FCSTD DOCUMENT  (FreeCAD 1.0R39109 (Git))
Label: internalDesign
License: All rights reserved
LicenseURL: http://en.wikipedia.org/wiki/All_rights_reserved
objects: Part::Feature×502, App::Part×92, Part::Cylinder×73, Part::Box×71, Part::MultiFuse×57, Part::Cut×51, Sketcher::SketchObject×38, Part::Extrusion×37, Part::Fillet×31, Part::Compound×8, Part::Sphere×4, Part::FeaturePython×2, Part::Torus×1
note: 913 computed .brp shape members not serialized (recipe doc carries the construction recipe); baked Part::Feature solids carry a one-line shape summary decoded from their .brp

FEATURE [Part::Feature] Part__Feature016  label="Z_-16147B_ZH-16147B-01"
  shape: bbox 438.9 x 219.4 x 405.1 mm, 3210 faces (baked)
FEATURE [Part::Feature] Part__Feature017  label="INSERTS-4"
  Placement = pos=(-180.975,-168.256,-155.575) rot=(0,0,1;0rad)
  shape: bbox 7.519 x 8.463 x 7.519 mm, 71 faces (baked)
FEATURE [Part::Feature] Part__Feature018  label="INSERTS-005"
  Placement = pos=(-170.872,-174.835,-145.472) rot=(0,0,1;3.14159rad)
  shape: bbox 7.519 x 8.463 x 7.519 mm, 71 faces (baked)
FEATURE [Part::Feature] Part__Feature019  label="INSERTS-006"
  Placement = pos=(-205.994,-3.7592,-180.594) rot=(0,0,1;3.14159rad)
  shape: bbox 7.519 x 8.463 x 7.519 mm, 71 faces (baked)
FEATURE [Part::Feature] Part__Feature020  label="INSERTS-007"
  Placement = pos=(-180.975,-168.083,155.575) rot=(1,0,0;3.14159rad)
  shape: bbox 7.519 x 8.463 x 7.519 mm, 71 faces (baked)
FEATURE [Part::Feature] Part__Feature021  label="INSERTS-008"
  Placement = pos=(-170.872,-175.008,145.472) rot=(0,1,0;3.14159rad)
  shape: bbox 7.519 x 8.463 x 7.519 mm, 71 faces (baked)
FEATURE [Part::Feature] Part__Feature022  label="INSERTS-009"
  Placement = pos=(-205.994,-3.93217,180.594) rot=(0,1,0;3.14159rad)
  shape: bbox 7.519 x 8.463 x 7.519 mm, 71 faces (baked)
FEATURE [Part::Feature] Part__Feature023  label="INSERTS-010"
  Placement = pos=(180.975,-168.083,-155.575) rot=(0,0,1;3.14159rad)
  shape: bbox 7.519 x 8.463 x 7.519 mm, 71 faces (baked)
FEATURE [Part::Feature] Part__Feature024  label="INSERTS-011"
  Placement = pos=(170.872,-175.008,-145.472) rot=(0,0,1;0rad)
  shape: bbox 7.519 x 8.463 x 7.519 mm, 71 faces (baked)
FEATURE [Part::Feature] Part__Feature025  label="INSERTS-012"
  Placement = pos=(205.994,-3.93217,-180.594) rot=(0,0,1;0rad)
  shape: bbox 7.519 x 8.463 x 7.519 mm, 71 faces (baked)
FEATURE [Part::Feature] Part__Feature026  label="INSERTS-013"
  Placement = pos=(180.975,-168.256,155.575) rot=(0,1,0;3.14159rad)
  shape: bbox 7.519 x 8.463 x 7.519 mm, 71 faces (baked)
FEATURE [Part::Feature] Part__Feature027  label="INSERTS-014"
  Placement = pos=(170.872,-174.835,145.472) rot=(1,0,0;3.14159rad)
  shape: bbox 7.519 x 8.463 x 7.519 mm, 71 faces (baked)
FEATURE [Part::Feature] Part__Feature028  label="INSERTS-015"
  Placement = pos=(205.994,-3.7592,180.594) rot=(1,0,0;3.14159rad)
  shape: bbox 7.519 x 8.463 x 7.519 mm, 71 faces (baked)
FEATURE [Part::Feature] Part__Feature029  label="LABEL-104"
  Placement = pos=(-1.221e-12,-20.3197,-180.67) rot=(1,0,0;1.56207rad)
  shape: bbox 63.5 x 38.1 x 0.3833 mm, 10 faces (baked)
FEATURE [Part::Feature] Part__Feature030  label="Z_-16141C_ZH-16141C-01"
  shape: bbox 448.9 x 49.63 x 409 mm, 1738 faces (baked)
FEATURE [Part::Feature] Part__Feature031  label="ZH-1614G"
  Placement = pos=(0,0.635,6.9e-15) rot=(0,0,1;0rad)
  shape: bbox 434.5 x 6.35 x 383.7 mm, 136 faces (baked)
FEATURE [Part::Feature] Part__Feature032  label="ZH-01F_ZH-01F-01"
  Placement = pos=(-158.172,-191.294,-145.472) rot=(0,0,1;0rad)
  shape: bbox 75.05 x 15.88 x 54.71 mm, 393 faces (baked)
FEATURE [Part::Feature] Part__Feature033  label="pan cross head_ai_SCREWS-046"
  Placement = pos=(-170.872,-191.294,-145.472) rot=(-0.002139,-0.002139,0.999995;1.5708rad)
  shape: bbox 10.25 x 22.43 x 10.25 mm, 92 faces (baked)
FEATURE [Part::Feature] Part__Feature034  label="pan cross head_ai_SCREWS-047"
  Placement = pos=(-170.872,-191.294,145.472) rot=(0.002139,0.002139,0.999995;1.5708rad)
  shape: bbox 10.25 x 22.43 x 10.25 mm, 92 faces (baked)
FEATURE [Part::Feature] Part__Feature035  label="ZH-01F_ZH-01F-002"
  Placement = pos=(-158.172,-191.294,145.472) rot=(0,0,1;0rad)
  shape: bbox 75.05 x 15.88 x 54.71 mm, 393 faces (baked)
FEATURE [Part::Feature] Part__Feature036  label="pan cross head_ai_SCREWS-048"
  Placement = pos=(170.872,-191.294,-145.472) rot=(0.707106,0.707106,-0.001512;3.14462rad)
  shape: bbox 10.25 x 22.43 x 10.25 mm, 92 faces (baked)
FEATURE [Part::Feature] Part__Feature037  label="pan cross head_ai_SCREWS-049"
  Placement = pos=(170.872,-191.294,145.472) rot=(0.707106,0.707106,0.001512;3.13857rad)
  shape: bbox 10.25 x 22.43 x 10.25 mm, 92 faces (baked)
FEATURE [Part::Feature] Part__Feature038  label="ZH-01F_ZH-01F-003"
  Placement = pos=(158.172,-191.294,-145.472) rot=(0,1,0;3.14159rad)
  shape: bbox 75.05 x 15.88 x 54.71 mm, 393 faces (baked)
FEATURE [Part::Feature] Part__Feature039  label="ZH-01F_ZH-01F-004"
  Placement = pos=(158.172,-191.294,145.472) rot=(0,1,0;3.14159rad)
  shape: bbox 75.05 x 15.88 x 54.71 mm, 393 faces (baked)
FEATURE [Part::Feature] Part__Feature040  label="SCREWS-047_default"
  Placement = pos=(-205.994,12.0142,-180.594) rot=(-1,0,0;1.5708rad)
  shape: bbox 9.234 x 22.51 x 9.177 mm, 32 faces (baked)
FEATURE [Part::Feature] Part__Feature041  label="SCREWS-047_default001"
  Placement = pos=(205.994,12.0142,-180.594) rot=(-1,0,0;1.5708rad)
  shape: bbox 9.234 x 22.51 x 9.177 mm, 32 faces (baked)
FEATURE [Part::Feature] Part__Feature042  label="SCREWS-047_default002"
  Placement = pos=(-205.994,12.0142,180.594) rot=(-1,0,0;1.5708rad)
  shape: bbox 9.234 x 22.51 x 9.177 mm, 32 faces (baked)
FEATURE [Part::Feature] Part__Feature043  label="SCREWS-047_default003"
  Placement = pos=(205.994,12.0142,180.594) rot=(-1,0,0;1.5708rad)
  shape: bbox 9.234 x 22.51 x 9.177 mm, 32 faces (baked)
FEATURE [App::Part] Z__16141CG_ZH_16141CG_01  label="Z_-16141CG_ZH-16141CG-01"
  Group = -> [Part__Feature030,Part__Feature031]
  Origin = -> Origin005
FEATURE [App::Part] Z__16147BI_ZH_16147BI_01  label="Z_-16147BI_ZH-16147BI-01"
  Group = -> [Part__Feature016,Part__Feature017,Part__Feature018,Part__Feature019,Part__Feature020,Part__Feature021,Part__Feature022,Part__Feature023,Part__Feature024,Part__Feature025,Part__Feature026,Part__Feature027,Part__Feature028,Part__Feature029]
  Origin = -> Origin004
FEATURE [App::Part] ZH_161407_33  label="ZH-161407-33"
  Group = -> [Z__16147BI_ZH_16147BI_01,Z__16141CG_ZH_16141CG_01,Part__Feature032,Part__Feature033,Part__Feature034,Part__Feature035,Part__Feature036,Part__Feature037,Part__Feature038,Part__Feature039,Part__Feature040,Part__Feature041,Part__Feature042,Part__Feature043]
  Origin = -> Origin006
  Placement = pos=(0,0,0) rot=(0.707107,0,0.707107;3.14159rad)
FEATURE [Sketcher::SketchObject] Sketch
  ArcFitTolerance = 0
  FullyConstrained = true
  MakeInternals = false
  Placement = pos=(0,164,0) rot=(1,0,0;1.5708rad)
  sketch-geometry (12):
    g0: ArcOfCircle CenterX=-140.58 CenterY=-165.98 CenterZ=0 NormalX=0 NormalY=0 NormalZ=1 AngleXU=0 Radius=30 StartAngle=3.14159 EndAngle=4.71239
    g1: ArcOfCircle CenterX=-140.58 CenterY=165.98 CenterZ=0 NormalX=0 NormalY=0 NormalZ=1 AngleXU=0 Radius=30 StartAngle=1.5708 EndAngle=3.14159
    g2: ArcOfCircle CenterX=140.58 CenterY=165.98 CenterZ=0 NormalX=0 NormalY=0 NormalZ=1 AngleXU=0 Radius=30 StartAngle=0 EndAngle=1.5708
    g3: ArcOfCircle CenterX=140.58 CenterY=-165.98 CenterZ=0 NormalX=0 NormalY=0 NormalZ=1 AngleXU=0 Radius=30 StartAngle=4.71239 EndAngle=6.28319
    g4: LineSegment StartX=-140.58 StartY=195.98 StartZ=0 EndX=140.58 EndY=195.98 EndZ=0
    g5: LineSegment StartX=-170.58 StartY=165.98 StartZ=0 EndX=-170.58 EndY=-165.98 EndZ=0
    g6: LineSegment StartX=-140.58 StartY=-195.98 StartZ=0 EndX=140.58 EndY=-195.98 EndZ=0
    g7: LineSegment StartX=170.58 StartY=-165.98 StartZ=0 EndX=170.58 EndY=165.98 EndZ=0
    g8: Circle CenterX=-155.58 CenterY=180.98 CenterZ=0 NormalX=0 NormalY=0 NormalZ=1 AngleXU=0 Radius=2.5
    g9: Circle CenterX=-155.58 CenterY=-180.98 CenterZ=0 NormalX=0 NormalY=0 NormalZ=1 AngleXU=0 Radius=2.5
    g10: Circle CenterX=155.58 CenterY=180.98 CenterZ=0 NormalX=0 NormalY=0 NormalZ=1 AngleXU=0 Radius=2.5
    g11: Circle CenterX=155.58 CenterY=-180.98 CenterZ=0 NormalX=0 NormalY=0 NormalZ=1 AngleXU=0 Radius=2.5
  constraints (40):
    c: Coincident(g4,g1)
    c: Coincident(g4,g2)
    c: Horizontal(g4)
    c: Coincident(g5,g1)
    c: Coincident(g5,g0)
    c: Vertical(g5)
    c: Coincident(g6,g0)
    c: Coincident(g6,g3)
    c: Horizontal(g6)
    c: Coincident(g7,g3)
    c: Coincident(g7,g2)
    c: Vertical(g7)
    c: Horizontal(g2,g2)
    c: Vertical(g2,g2)
    c: Vertical(g1,g1)
    c: Vertical(g0,g0)
    c: Vertical(g3,g3)
    c: Horizontal(g3,g3)
    c: DistanceX(g2,g2) = 30
    c: Horizontal(g3,g0)
    c: Vertical(g0,g1)
    c: DistanceX(g1,g8) = 15
    c: DistanceY(g8,g1) = 15
    c: DistanceX(g8) = -155.58
    c: DistanceX(g9) = -155.58
    c: DistanceY(g9) = -180.98
    c: DistanceY(g8) = 180.98
    c: DistanceY(g0,g9) = 15
    c: Horizontal(g1,g1)
    c: DistanceX(g1,g1) = 30
    c: Horizontal(g10,g8)
    c: DistanceX(g10,g2) = 15
    c: DistanceX(g10) = 155.58
    c: Horizontal(g11,g9)
    c: Vertical(g11,g10)
    c: DistanceY(g9,g0) = 15
    c: Equal(g8,g10)
    c: Equal(g8,g11)
    c: Equal(g8,g9)
    c: Diameter(g8) = 5
FEATURE [Part::Extrusion] Extrude  label="base"
  Base = -> Sketch
  Dir = (0,-1,2e-16)
  DirMode = 2
  FaceMakerClass = Part::FaceMakerBullseye
  FaceMakerMode = 3
  LengthFwd = 6
  LengthRev = 0
  Solid = true
  Symmetric = false
FEATURE [Part::Box] Box  label="Base_Board"
  AttacherType = Attacher::AttachEngine3D
  Height = 2
  Length = 208
  Width = 89.3
FEATURE [Part::Box] Box001  label="Ozone_monitor"
  AttacherType = Attacher::AttachEngine3D
  Height = 70
  Length = 189.5
  Placement = pos=(9.5,62.5,2) rot=(0,0,1;0rad)
  Width = 26.75
FEATURE [Part::Cylinder] Cylinder
  Angle = 360
  AttacherType = Attacher::AttachEngine3D
  FirstAngle = 0
  Height = 10
  Placement = pos=(5.4,6.4,0) rot=(0,0,1;0rad)
  Radius = 1.75
  SecondAngle = 0
FEATURE [Part::Cylinder] Cylinder001
  Angle = 360
  AttacherType = Attacher::AttachEngine3D
  FirstAngle = 0
  Height = 10
  Placement = pos=(5.4,82.6,0) rot=(0,0,1;0rad)
  Radius = 1.75
  SecondAngle = 0
FEATURE [Part::Cylinder] Cylinder002
  Angle = 360
  AttacherType = Attacher::AttachEngine3D
  FirstAngle = 0
  Height = 10
  Placement = pos=(203,82.6,0) rot=(0,0,1;0rad)
  Radius = 1.75
  SecondAngle = 0
FEATURE [Part::Cylinder] Cylinder003
  Angle = 360
  AttacherType = Attacher::AttachEngine3D
  FirstAngle = 0
  Height = 10
  Placement = pos=(203,6.4,0) rot=(0,0,1;0rad)
  Radius = 1.75
  SecondAngle = 0
FEATURE [Part::Fillet] Fillet  label="Base"
  Base = -> Box
  EdgeLinks = -> Box [Edge1,Edge3,Edge5,Edge7]
  Edges = 4 edges r=2.5: [Edge1,Edge3,Edge5,Edge7]
FEATURE [Part::MultiFuse] Fusion  label="Base_hole"
  Placement = pos=(0,0,-4) rot=(0,0,1;0rad)
  Shapes = -> [Cylinder,Cylinder001,Cylinder002,Cylinder003]
FEATURE [Part::MultiFuse] Fusion001  label="Ozone"
  Shapes = -> [Fillet,Box001]
FEATURE [Part::Cut] Cut  label="Ozone Module"
  Base = -> Fusion001
  Placement = pos=(-135,157,89.2) rot=(1,0,0;1.5708rad)
  Tool = -> Fusion
FEATURE [Part::Feature] Part__Feature165  label="CUI_VGS-35C-052"
  shape: bbox 82 x 30 x 99 mm, 244 faces (baked)
FEATURE [Part::Feature] Part__Feature166  label="CUI_VGS-35C-053"
  shape: bbox 49.5 x 17 x 16 mm, 923 faces (baked)
FEATURE [Part::Feature] Part__Feature167  label="CUI_VGS-35C-054"
  shape: bbox 4.624 x 1.433 x 4.618 mm, 8 faces (baked)
FEATURE [Part::Feature] Part__Feature168  label="CUI_VGS-35C-055"
  shape: bbox 5.413 x 8.147 x 5.413 mm, 53 faces (baked)
FEATURE [Part::Feature] Part__Feature169  label="CUI_VGS-35C-056"
  shape: bbox 5.8 x 4.834 x 5.8 mm, 40 faces (baked)
FEATURE [Part::Feature] Part__Feature170  label="CUI_VGS-35C-057"
  shape: bbox 3 x 7.6 x 3.04 mm, 12 faces (baked)
FEATURE [Part::Feature] Part__Feature171  label="CUI_VGS-35C-058"
  shape: bbox 81 x 29 x 76 mm, 406 faces (baked)
FEATURE [Part::Feature] Part__Feature172  label="CUI_VGS-35C-059"
  shape: bbox 7 x 0.55 x 7 mm, 6 faces (baked)
FEATURE [Part::Feature] Part__Feature173  label="CUI_VGS-35C-060"
  shape: bbox 6.811 x 11.02 x 8.111 mm, 138 faces (baked)
FEATURE [Part::Feature] Part__Feature174  label="CUI_VGS-35C-061"
  shape: bbox 78.62 x 1.622 x 92.02 mm, 385 faces (baked)
FEATURE [App::Part] CUI_VGS_35C_016  label="CUI_VGS-35C-022:12V-01"
  Group = -> [Part__Feature165,Part__Feature166,Part__Feature167,Part__Feature168,Part__Feature169,Part__Feature170,Part__Feature171,Part__Feature172,Part__Feature173,Part__Feature174]
  Origin = -> Origin017
  Placement = pos=(-130,141,-106.5) rot=(1,0,0;3.14159rad)
FEATURE [Part::Feature] Part__Feature175  label="CUI_VGS-35C-062"
  shape: bbox 82 x 30 x 99 mm, 244 faces (baked)
FEATURE [Part::Feature] Part__Feature176  label="CUI_VGS-35C-063"
  shape: bbox 49.5 x 17 x 16 mm, 923 faces (baked)
FEATURE [Part::Feature] Part__Feature177  label="CUI_VGS-35C-064"
  shape: bbox 4.624 x 1.433 x 4.618 mm, 8 faces (baked)
FEATURE [Part::Feature] Part__Feature178  label="CUI_VGS-35C-065"
  shape: bbox 5.413 x 8.147 x 5.413 mm, 53 faces (baked)
FEATURE [Part::Feature] Part__Feature179  label="CUI_VGS-35C-066"
  shape: bbox 5.8 x 4.834 x 5.8 mm, 40 faces (baked)
FEATURE [Part::Feature] Part__Feature180  label="CUI_VGS-35C-067"
  shape: bbox 3 x 7.6 x 3.04 mm, 12 faces (baked)
FEATURE [Part::Feature] Part__Feature181  label="CUI_VGS-35C-068"
  shape: bbox 81 x 29 x 76 mm, 406 faces (baked)
FEATURE [Part::Feature] Part__Feature182  label="CUI_VGS-35C-069"
  shape: bbox 7 x 0.55 x 7 mm, 6 faces (baked)
FEATURE [Part::Feature] Part__Feature183  label="CUI_VGS-35C-070"
  shape: bbox 6.811 x 11.02 x 8.111 mm, 138 faces (baked)
FEATURE [Part::Feature] Part__Feature184  label="CUI_VGS-35C-071"
  shape: bbox 78.62 x 1.622 x 92.02 mm, 385 faces (baked)
FEATURE [App::Part] CUI_VGS_35C_017  label="CUI_VGS-35C-022:12V-02"
  Group = -> [Part__Feature175,Part__Feature176,Part__Feature177,Part__Feature178,Part__Feature179,Part__Feature180,Part__Feature181,Part__Feature182,Part__Feature183,Part__Feature184]
  Origin = -> Origin018
  Placement = pos=(-45,141,-106.5) rot=(1,0,0;3.14159rad)
FEATURE [Part::Feature] Part__Feature185  label="CUI_VGS-35C-072"
  shape: bbox 82 x 30 x 99 mm, 244 faces (baked)
FEATURE [Part::Feature] Part__Feature186  label="CUI_VGS-35C-073"
  shape: bbox 49.5 x 17 x 16 mm, 923 faces (baked)
FEATURE [Part::Feature] Part__Feature187  label="CUI_VGS-35C-074"
  shape: bbox 4.624 x 1.433 x 4.618 mm, 8 faces (baked)
FEATURE [Part::Feature] Part__Feature188  label="CUI_VGS-35C-075"
  shape: bbox 5.413 x 8.147 x 5.413 mm, 53 faces (baked)
FEATURE [Part::Feature] Part__Feature189  label="CUI_VGS-35C-076"
  shape: bbox 5.8 x 4.834 x 5.8 mm, 40 faces (baked)
FEATURE [Part::Feature] Part__Feature190  label="CUI_VGS-35C-077"
  shape: bbox 3 x 7.6 x 3.04 mm, 12 faces (baked)
FEATURE [Part::Feature] Part__Feature191  label="CUI_VGS-35C-078"
  shape: bbox 81 x 29 x 76 mm, 406 faces (baked)
FEATURE [Part::Feature] Part__Feature192  label="CUI_VGS-35C-079"
  shape: bbox 7 x 0.55 x 7 mm, 6 faces (baked)
FEATURE [Part::Feature] Part__Feature193  label="CUI_VGS-35C-080"
  shape: bbox 6.811 x 11.02 x 8.111 mm, 138 faces (baked)
FEATURE [Part::Feature] Part__Feature194  label="CUI_VGS-35C-081"
  shape: bbox 78.62 x 1.622 x 92.02 mm, 385 faces (baked)
FEATURE [App::Part] CUI_VGS_35C_018  label="CUI_VGS-35C-022:12V-03"
  Group = -> [Part__Feature185,Part__Feature186,Part__Feature187,Part__Feature188,Part__Feature189,Part__Feature190,Part__Feature191,Part__Feature192,Part__Feature193,Part__Feature194]
  Origin = -> Origin019
  Placement = pos=(40,141,-106.5) rot=(1,0,0;3.14159rad)
FEATURE [Part::Box] Box003  label="Cube003"
  AttacherType = Attacher::AttachEngine3D
  Height = 57
  Length = 14.7
  Placement = pos=(-29,-7,-28) rot=(0,0,1;0rad)
  Width = 38
FEATURE [Part::Box] Box004  label="Cube004"
  AttacherType = Attacher::AttachEngine3D
  Height = 57
  Length = 14.7
  Placement = pos=(14.3,-7,-31) rot=(0,0,1;0rad)
  Width = 38
FEATURE [Part::Box] Box005  label="Cube009"
  AttacherType = Attacher::AttachEngine3D
  Height = 25
  Length = 31
  Placement = pos=(37.5,83.5,6) rot=(0,0,1;0rad)
  Width = 27
FEATURE [Part::Box] Box006  label="lan_cube"
  AttacherType = Attacher::AttachEngine3D
  Height = 13.25
  Length = 16.5
  Placement = pos=(11.25,101,14.8) rot=(0,0,1;0rad)
  Width = 10
FEATURE [Part::Box] Box007  label="Cube010"
  AttacherType = Attacher::AttachEngine3D
  Height = 10
  Length = 21
  Placement = pos=(5.5,15,0) rot=(0,0,1;0rad)
  Width = 13.5
FEATURE [Part::Box] Box013  label="Cube"
  AttacherType = Attacher::AttachEngine3D
  Height = 37
  Length = 78.5
  Width = 108.5
FEATURE [Part::Box] Box014  label="Cube001"
  AttacherType = Attacher::AttachEngine3D
  Height = 27.5
  Length = 27
  Placement = pos=(26.5,0,4.75) rot=(0,0,1;0rad)
  Width = 20
FEATURE [Part::Box] Box015  label="Cube002"
  AttacherType = Attacher::AttachEngine3D
  Height = 57
  Length = 62
  Placement = pos=(-29,-44,-31) rot=(0,0,1;0rad)
  Width = 38
FEATURE [Part::Box] Box016  label="Cube011"
  AttacherType = Attacher::AttachEngine3D
  Height = 10
  Length = 20.8
  Placement = pos=(5.6,15.1,0) rot=(0,0,1;0rad)
  Width = 13.3
FEATURE [Part::Box] Box017  label="Cube012"
  AttacherType = Attacher::AttachEngine3D
  Height = 5
  Length = 21
  Placement = pos=(5.5,13.5,0) rot=(0,0,1;0rad)
  Width = 13.5
FEATURE [Part::Box] Box018  label="Cube013"
  AttacherType = Attacher::AttachEngine3D
  Height = 5
  Length = 20.8
  Placement = pos=(5.5,13.5,0) rot=(0,0,1;0rad)
  Width = 13.3
FEATURE [Part::Box] Box019  label="Cube014"
  AttacherType = Attacher::AttachEngine3D
  Height = 29.5
  Length = 120
  Width = 120
FEATURE [Part::Box] Box020  label="Cube015"
  AttacherType = Attacher::AttachEngine3D
  Height = 3.17
  Length = 9
  Placement = pos=(21.5,-6,5.92) rot=(0,0,1;0rad)
  Width = 10
FEATURE [Part::Box] Box021  label="Cube016"
  AttacherType = Attacher::AttachEngine3D
  Height = 13.25
  Length = 16.5
  Placement = pos=(40.25,0,6) rot=(0,0,1;0rad)
  Width = 10
FEATURE [Part::Box] Box022  label="Cube017"
  AttacherType = Attacher::AttachEngine3D
  Height = 6.5
  Length = 14.5
  Width = 10
FEATURE [Part::Box] Box023  label="Cube018"
  AttacherType = Attacher::AttachEngine3D
  Height = 1.75
  Length = 10
  Placement = pos=(110,76.5,5.5) rot=(0,0,1;0rad)
  Width = 17
FEATURE [Part::Box] Box024  label="Bottom_left"
  AttacherType = Attacher::AttachEngine3D
  Height = 27
  Length = 10
  Placement = pos=(-65,148,-38.5) rot=(0,0,1;0rad)
  Width = 10
FEATURE [Part::Box] Box025  label="Bottom_right"
  AttacherType = Attacher::AttachEngine3D
  Height = 27
  Length = 10
  Placement = pos=(55,148,-38.5) rot=(0,0,1;0rad)
  Width = 10
FEATURE [Part::Box] Box026  label="Top_left"
  AttacherType = Attacher::AttachEngine3D
  Height = 36.5
  Length = 10
  Placement = pos=(-45.68,71,-48) rot=(0,0,1;0rad)
  Width = 7
FEATURE [Part::Box] Box027  label="Top_right"
  AttacherType = Attacher::AttachEngine3D
  Height = 36.5
  Length = 10
  Placement = pos=(35.68,71,-48) rot=(0,0,1;0rad)
  Width = 7
FEATURE [Part::Box] Box028  label="Top_middle"
  AttacherType = Attacher::AttachEngine3D
  Height = 36.5
  Length = 16
  Placement = pos=(-8,71,-48) rot=(0,0,1;0rad)
  Width = 7
FEATURE [Part::Box] Box029  label="Bottom_left001"
  AttacherType = Attacher::AttachEngine3D
  Height = 27
  Length = 10
  Placement = pos=(-70.5,140,-38.5) rot=(0,0,1;0rad)
  Width = 18
FEATURE [Part::Box] Box030  label="Bottom_right001"
  AttacherType = Attacher::AttachEngine3D
  Height = 27
  Length = 10
  Placement = pos=(60.5,140,-38.5) rot=(0,0,1;0rad)
  Width = 18
FEATURE [Part::Box] Box031  label="Top_left001"
  AttacherType = Attacher::AttachEngine3D
  Height = 36.5
  Length = 15
  Placement = pos=(-50,28,-48) rot=(0,0,1;0rad)
  Width = 7
FEATURE [Part::Box] Box032  label="Top_right001"
  AttacherType = Attacher::AttachEngine3D
  Height = 36.5
  Length = 15
  Placement = pos=(35,28,-48) rot=(0,0,1;0rad)
  Width = 7
FEATURE [Part::Box] Box033  label="Top_middle001"
  AttacherType = Attacher::AttachEngine3D
  Height = 36.5
  Length = 16
  Placement = pos=(-8,28,-48) rot=(0,0,1;0rad)
  Width = 7
FEATURE [Part::Cut] Cut001  label="Power_out_cut"
  Base = -> Box013
  Tool = -> Box014
FEATURE [Part::Cylinder] Cylinder004
  Angle = 360
  AttacherType = Attacher::AttachEngine3D
  FirstAngle = 0
  Height = 10
  Placement = pos=(61,31,27) rot=(0,0,1;0rad)
  Radius = 6.5
  SecondAngle = 0
FEATURE [Part::Cut] Cut002  label="Power_button_cut"
  Base = -> Cut001
  Tool = -> Cylinder004
FEATURE [Part::Cut] Cut006  label="Power_in_cut"
  Base = -> Cut002
  Tool = -> Box005
FEATURE [Part::Cut] Cut007  label="LAN_cut"
  Base = -> Cut006
  Tool = -> Box006
FEATURE [Part::Cylinder] Cylinder005  label="power_butt"
  Angle = 360
  AttacherType = Attacher::AttachEngine3D
  FirstAngle = 0
  Height = 10
  Placement = pos=(61,31,27) rot=(0,0,1;0rad)
  Radius = 6.25
  SecondAngle = 0
FEATURE [Part::Cylinder] Cylinder006
  Angle = 360
  AttacherType = Attacher::AttachEngine3D
  FirstAngle = 0
  Height = 3.25
  Placement = pos=(61,31.5,37) rot=(-1,0,0;1.5708rad)
  Radius = 0.25
  SecondAngle = 0
FEATURE [Part::Cylinder] Cylinder007
  Angle = 360
  AttacherType = Attacher::AttachEngine3D
  FirstAngle = 0
  Height = 10
  Placement = pos=(27,112,14.75) rot=(-1,0,0;1.5708rad)
  Radius = 6.35
  SecondAngle = 0
FEATURE [Part::Cylinder] Cylinder008
  Angle = 360
  AttacherType = Attacher::AttachEngine3D
  FirstAngle = 0
  Height = 10
  Placement = pos=(93,112,14.75) rot=(-1,0,0;1.5708rad)
  Radius = 6.35
  SecondAngle = 0
FEATURE [Part::Cylinder] Cylinder009
  Angle = 360
  AttacherType = Attacher::AttachEngine3D
  FirstAngle = 0
  Height = 3
  Placement = pos=(93,119,14.75) rot=(-1,0,0;1.5708rad)
  Radius = 5.85
  SecondAngle = 0
FEATURE [Part::Cut] Cut011  label="4g"
  Base = -> Cylinder008
  Tool = -> Cylinder009
FEATURE [Part::Cylinder] Cylinder010
  Angle = 360
  AttacherType = Attacher::AttachEngine3D
  FirstAngle = 0
  Height = 10
  Placement = pos=(92,10,10) rot=(1,0,0;1.5708rad)
  Radius = 1
  SecondAngle = 0
FEATURE [Part::Cylinder] Cylinder011
  Angle = 360
  AttacherType = Attacher::AttachEngine3D
  FirstAngle = 0
  Height = 10
  Placement = pos=(14.5,14.5,-2) rot=(0,0,1;0rad)
  Radius = 5.5
  SecondAngle = 0
FEATURE [Part::Cylinder] Cylinder012
  Angle = 360
  AttacherType = Attacher::AttachEngine3D
  FirstAngle = 0
  Height = 10
  Placement = pos=(14.5,14.5,-2.5) rot=(0,0,1;0rad)
  Radius = 4.5
  SecondAngle = 0
FEATURE [Part::Cylinder] Cylinder013
  Angle = 360
  AttacherType = Attacher::AttachEngine3D
  FirstAngle = 0
  Height = 10
  Placement = pos=(14.5,14.5,-2) rot=(0,0,1;0rad)
  Radius = 5.5
  SecondAngle = 0
FEATURE [Part::Cylinder] Cylinder014
  Angle = 360
  AttacherType = Attacher::AttachEngine3D
  FirstAngle = 0
  Height = 10
  Placement = pos=(14.5,14.5,-2.5) rot=(0,0,1;0rad)
  Radius = 4.5
  SecondAngle = 0
FEATURE [Part::Cylinder] Cylinder015
  Angle = 360
  AttacherType = Attacher::AttachEngine3D
  FirstAngle = 0
  Height = 10
  Placement = pos=(14.5,14.5,-2) rot=(0,0,1;0rad)
  Radius = 5.5
  SecondAngle = 0
FEATURE [Part::Cylinder] Cylinder016
  Angle = 360
  AttacherType = Attacher::AttachEngine3D
  FirstAngle = 0
  Height = 10
  Placement = pos=(14.5,14.5,-2.5) rot=(0,0,1;0rad)
  Radius = 4.5
  SecondAngle = 0
FEATURE [Part::Cylinder] Cylinder017
  Angle = 360
  AttacherType = Attacher::AttachEngine3D
  FirstAngle = 0
  Height = 10
  Placement = pos=(14.5,14.5,-2) rot=(0,0,1;0rad)
  Radius = 5.5
  SecondAngle = 0
FEATURE [Part::Cylinder] Cylinder018
  Angle = 360
  AttacherType = Attacher::AttachEngine3D
  FirstAngle = 0
  Height = 10
  Placement = pos=(14.5,14.5,-2.5) rot=(0,0,1;0rad)
  Radius = 4.5
  SecondAngle = 0
FEATURE [Part::Cylinder] Cylinder019  label="m3_l"
  Angle = 360
  AttacherType = Attacher::AttachEngine3D
  FirstAngle = 0
  Height = 15
  Placement = pos=(-59,160,-7) rot=(1,0,0;1.5708rad)
  Radius = 1.6
  SecondAngle = 0
FEATURE [Part::Cylinder] Cylinder020  label="m3_r"
  Angle = 360
  AttacherType = Attacher::AttachEngine3D
  FirstAngle = 0
  Height = 15
  Placement = pos=(59,160,-7) rot=(1,0,0;1.5708rad)
  Radius = 1.6
  SecondAngle = 0
FEATURE [Part::Cylinder] Cylinder021  label="m3_lm"
  Angle = 360
  AttacherType = Attacher::AttachEngine3D
  FirstAngle = 0
  Height = 15
  Placement = pos=(-22,160,-7) rot=(1,0,0;1.5708rad)
  Radius = 1.6
  SecondAngle = 0
FEATURE [Part::Cylinder] Cylinder022  label="m3_rm"
  Angle = 360
  AttacherType = Attacher::AttachEngine3D
  FirstAngle = 0
  Height = 15
  Placement = pos=(22,160,-7) rot=(1,0,0;1.5708rad)
  Radius = 1.6
  SecondAngle = 0
FEATURE [Part::Cylinder] Cylinder023  label="m3_l001"
  Angle = 360
  AttacherType = Attacher::AttachEngine3D
  FirstAngle = 0
  Height = 15
  Placement = pos=(-59,160,-7) rot=(1,0,0;1.5708rad)
  Radius = 1.6
  SecondAngle = 0
FEATURE [Part::Cylinder] Cylinder024  label="m3_r001"
  Angle = 360
  AttacherType = Attacher::AttachEngine3D
  FirstAngle = 0
  Height = 15
  Placement = pos=(59,160,-7) rot=(1,0,0;1.5708rad)
  Radius = 1.6
  SecondAngle = 0
FEATURE [Part::Cylinder] Cylinder025  label="m3_lm001"
  Angle = 360
  AttacherType = Attacher::AttachEngine3D
  FirstAngle = 0
  Height = 15
  Placement = pos=(-22,160,-7) rot=(1,0,0;1.5708rad)
  Radius = 1.6
  SecondAngle = 0
FEATURE [Part::Cylinder] Cylinder026  label="m3_rm001"
  Angle = 360
  AttacherType = Attacher::AttachEngine3D
  FirstAngle = 0
  Height = 15
  Placement = pos=(22,160,-7) rot=(1,0,0;1.5708rad)
  Radius = 1.6
  SecondAngle = 0
FEATURE [Part::Fillet] Fillet003  label="main_box"
  Base = -> Cut007
  EdgeLinks = -> Cut007 [Edge1,Edge2,Edge3,Edge4,Edge5,Edge6,Edge7,Edge12,Edge13,Edge15,Edge16,Edge25]
  Edges = 12 edges r=3: [Edge1,Edge2,Edge3,Edge4,Edge5,Edge6,Edge7,Edge12,Edge13,Edge15,Edge16,Edge25]
FEATURE [Part::Fillet] Fillet004  label="Key_hole"
  Base = -> Box007
  EdgeLinks = -> Box007 [Edge1,Edge3,Edge5,Edge7]
  Edges = 4 edges r=1: [Edge1,Edge3,Edge5,Edge7]
FEATURE [Part::Cut] Cut008  label="first_hole"
  Base = -> Fillet003
  Tool = -> Fillet004
FEATURE [Part::Fillet] Fillet005  label="Key_hole_mount"
  Base = -> Box016
  EdgeLinks = -> Box016 [Edge1,Edge3,Edge5,Edge7]
  Edges = 4 edges r=1: [Edge1,Edge3,Edge5,Edge7]
FEATURE [Part::Fillet] Fillet006  label="Key_hole001"
  Base = -> Box017
  EdgeLinks = -> Box017 [Edge1,Edge3,Edge5,Edge7]
  Edges = 4 edges r=1: [Edge1,Edge3,Edge5,Edge7]
  Placement = pos=(45,57.75,0) rot=(0,0,1;0rad)
FEATURE [Part::Cut] Cut009  label="Hole2"
  Base = -> Cut008
  Tool = -> Fillet006
FEATURE [Part::Fillet] Fillet007  label="Key_hole002"
  Base = -> Box018
  EdgeLinks = -> Box018 [Edge1,Edge3,Edge5,Edge7]
  Edges = 4 edges r=1: [Edge1,Edge3,Edge5,Edge7]
  Placement = pos=(45.1,57.85,0) rot=(0,0,1;0rad)
FEATURE [Part::Fillet] Fillet008
  Base = -> Box020
  EdgeLinks = -> Box020 [Edge2,Edge4,Edge6,Edge8]
  Edges = 4 edges r=1.2: [Edge2,Edge4,Edge6,Edge8]
  Placement = pos=(0,6,0) rot=(0,0,1;0rad)
FEATURE [Part::Cut] Cut012  label="USB-C_cut"
  Base = -> Box019
  Tool = -> Fillet008
FEATURE [Part::Cut] Cut013  label="RJ45_Cut"
  Base = -> Cut012
  Tool = -> Box021
FEATURE [Part::Fillet] Fillet009  label="USB_Hole"
  Base = -> Box022
  EdgeLinks = -> Box022 [Edge2,Edge4,Edge6,Edge8]
  Edges = 4 edges r=0.5: [Edge2,Edge4,Edge6,Edge8]
  Placement = pos=(64.5,0,6.5) rot=(0,0,1;0rad)
FEATURE [Part::Cut] Cut014  label="USB_Hole_Cut"
  Base = -> Cut013
  Tool = -> Fillet009
FEATURE [Part::Cut] Cut015  label="LED_Cut"
  Base = -> Cut014
  Tool = -> Cylinder010
FEATURE [Part::Cut] Cut016  label="sim_cut"
  Base = -> Cut015
  Tool = -> Box023
FEATURE [Part::Fillet] Fillet010  label="Box"
  Base = -> Cut016
  EdgeLinks = -> Cut016 [Edge1,Edge3,Edge6,Edge32]
  Edges = 4 edges r=9: [Edge1,Edge3,Edge6,Edge32]
FEATURE [Part::MultiFuse] Fusion002  label="base_pad003"
  Placement = pos=(89.5,0,0) rot=(0,0,1;0rad)
  Shapes = -> [Cylinder015,Cylinder016]
FEATURE [Part::MultiFuse] Fusion007
  Shapes = -> [Fillet005,Cut009,Fillet007]
FEATURE [Part::MultiFuse] Fusion008  label="base_pad001"
  Shapes = -> [Cylinder011,Cylinder012]
FEATURE [Part::MultiFuse] Fusion009  label="base_pad002"
  Placement = pos=(0,89.5,0) rot=(0,0,1;0rad)
  Shapes = -> [Cylinder013,Cylinder014]
FEATURE [Part::MultiFuse] Fusion010  label="base_pad004"
  Placement = pos=(89.5,89.5,0) rot=(0,0,1;0rad)
  Shapes = -> [Cylinder017,Cylinder018]
FEATURE [Part::MultiFuse] Fusion004  label="Gateway_box"
  Shapes = -> [Fillet010,Fusion008,Fusion009,Fusion002,Fusion010]
FEATURE [Part::Fillet] Fillet011  label="GateWay_Box"
  Base = -> Fusion004
  EdgeLinks = -> Fusion004 [Edge1,Edge3,Edge5,Edge6,Edge7,Edge8,Edge9,Edge10,Edge11,Edge12,Edge14,Edge15,Edge16,Edge17,Edge18,Edge19]
  Edges = 16 edges r=1: [Edge1,Edge3,Edge5,Edge6,Edge7,Edge8,Edge9,Edge10,Edge11,Edge12,Edge14,Edge15,Edge16,Edge17,Edge18,Edge19]
FEATURE [Part::MultiFuse] Fusion012  label="m3"
  Shapes = -> [Cylinder019,Cylinder020,Cylinder021,Cylinder022]
FEATURE [Part::MultiFuse] Fusion014  label="m3_screws"
  Shapes = -> [Cylinder023,Cylinder024,Cylinder025,Cylinder026]
FEATURE [Part::Feature] Part__Feature  label="Body"
  shape: bbox 30 x 26.75 x 29.35 mm, 109 faces (baked)
FEATURE [Part::Feature] Part__Feature001  label="Body001"
  Placement = pos=(9e-16,-2.285,-17.7) rot=(0,0,1;0rad)
  shape: bbox 9 x 0.5 x 14.6 mm, 20 faces (baked)
FEATURE [Part::Feature] Part__Feature002  label="Body002"
  Placement = pos=(4.25,5.59,0) rot=(0,0,1;1.5708rad)
  shape: bbox 0.5 x 9 x 14.6 mm, 20 faces (baked)
FEATURE [Part::Feature] Part__Feature003  label="Body003"
  Placement = pos=(-4.25,5.59,0) rot=(0,0,1;1.5708rad)
  shape: bbox 0.5 x 9 x 14.6 mm, 20 faces (baked)
FEATURE [Part::Feature] Part__Feature004  label="Solid1"
  shape: bbox 48.94 x 58.74 x 22.24 mm, 535 faces (baked)
FEATURE [Part::Cut] Cut003
  Base = -> Part__Feature004
  Tool = -> Box015
FEATURE [Part::Cut] Cut004
  Base = -> Cut003
  Tool = -> Box003
FEATURE [Part::Cut] Cut005
  Base = -> Cut004
  Tool = -> Box004
FEATURE [Part::Feature] Part__Feature005  label="Solid3"
  shape: bbox 2 x 4 x 20.28 mm, 13 faces (baked)
FEATURE [Part::Feature] Part__Feature006  label="Solid004"
  shape: bbox 2 x 4 x 17.28 mm, 13 faces (baked)
FEATURE [Part::Feature] Part__Feature007  label="Solid005"
  shape: bbox 2 x 4 x 17.28 mm, 13 faces (baked)
FEATURE [Part::Feature] Part__Feature008  label="Solid4"
  shape: bbox 5.5 x 5.5 x 8.5 mm, 23 faces (baked)
FEATURE [Part::Feature] Part__Feature009  label="Solid007"
  shape: bbox 5.5 x 5.5 x 8.5 mm, 23 faces (baked)
FEATURE [Part::Feature] Part__Feature010  label="Solid008"
  shape: bbox 5.5 x 5.5 x 8.5 mm, 23 faces (baked)
FEATURE [Part::Feature] Part__Feature011  label="Solid009"
  shape: bbox 5.769 x 18 x 0.5 mm, 12 faces (baked)
FEATURE [Part::Feature] Part__Feature012  label="FUSE"
  Placement = pos=(2.76516,20.0677,-12.471) rot=(1,0,0;1.5708rad)
  shape: bbox 5 x 7 x 11.27 mm, 51 faces (baked)
FEATURE [Part::Feature] Part__Feature013  label="FUSE001"
  Placement = pos=(2.76516,20.0677,-12.471) rot=(1,0,0;1.5708rad)
  shape: bbox 2 x 2 x 2.691 mm, 4 faces (baked)
FEATURE [Part::Feature] Part__Feature014  label="FUSE002"
  Placement = pos=(2.76516,20.0677,-12.471) rot=(1,0,0;1.5708rad)
  shape: bbox 5 x 7 x 13.96 mm, 54 faces (baked)
FEATURE [App::Part] FUSE  label="FUSE003"
  Group = -> [Part__Feature012,Part__Feature013,Part__Feature014]
  Origin = -> Origin024
FEATURE [Part::Feature] Part__Feature015  label="COMPOUND011"
  Placement = pos=(0,-0.0056,0.0002) rot=(0,0,1;0rad)
  shape: bbox 0.4 x 11.61 x 3.651 mm, 6 faces (baked)
FEATURE [Part::Feature] Part__Feature247  label="COMPOUND012"
  Placement = pos=(0,-0.0056,0.0002) rot=(0,0,1;0rad)
  shape: bbox 0.4 x 11.61 x 3.651 mm, 6 faces (baked)
FEATURE [Part::Feature] Part__Feature248  label="COMPOUND013"
  Placement = pos=(0,-0.0056,0.0002) rot=(0,0,1;0rad)
  shape: bbox 0.4 x 11.61 x 3.651 mm, 6 faces (baked)
FEATURE [Part::Feature] Part__Feature249  label="COMPOUND014"
  Placement = pos=(0,-0.0056,0.0002) rot=(0,0,1;0rad)
  shape: bbox 0.4 x 11.61 x 3.651 mm, 6 faces (baked)
FEATURE [Part::Feature] Part__Feature250  label="COMPOUND015"
  Placement = pos=(0,-0.0056,0.0002) rot=(0,0,1;0rad)
  shape: bbox 0.4 x 11.61 x 3.651 mm, 6 faces (baked)
FEATURE [Part::Feature] Part__Feature251  label="COMPOUND016"
  Placement = pos=(0,-0.0056,0.0002) rot=(0,0,1;0rad)
  shape: bbox 0.4 x 11.61 x 3.651 mm, 6 faces (baked)
FEATURE [Part::Feature] Part__Feature252  label="COMPOUND017"
  Placement = pos=(0,-0.0056,0.0002) rot=(0,0,1;0rad)
  shape: bbox 0.4 x 11.61 x 3.651 mm, 6 faces (baked)
FEATURE [Part::Feature] Part__Feature253  label="Solid2"
  shape: bbox 23.81 x 12.73 x 19.05 mm, 337 faces (baked)
FEATURE [Part::Feature] Part__Feature254  label="FUSE (1)"
  Placement = pos=(2.90467,-3.14305,-31.7578) rot=(0,0,1;0rad)
  shape: bbox 5 x 5.737 x 5.737 mm, 4 faces (baked)
FEATURE [Part::Feature] Part__Feature255  label="FUSE (1)001"
  Placement = pos=(2.90467,-3.14305,-31.7578) rot=(0,0,1;0rad)
  shape: bbox 5 x 5.737 x 5.737 mm, 4 faces (baked)
FEATURE [Part::Feature] Part__Feature256  label="FUSE (1)002"
  Placement = pos=(2.90467,-3.14305,-31.7578) rot=(0,0,1;0rad)
  shape: bbox 10 x 4.6 x 4.6 mm, 3 faces (baked)
FEATURE [Part::Feature] Part__Feature257  label="FUSE (1)003"
  Placement = pos=(2.90467,-3.14305,-31.7578) rot=(0,0,1;0rad)
  shape: bbox 10 x 0.5 x 0.5 mm, 3 faces (baked)
FEATURE [App::Part] FUSE__1_  label="FUSE (1)004"
  Group = -> [Part__Feature254,Part__Feature255,Part__Feature256,Part__Feature257]
  Origin = -> Origin025
FEATURE [Part::Feature] Part__Feature258  label="COMPOUND003"
  Placement = pos=(0,-0.0056,0.0002) rot=(0,0,1;0rad)
  shape: bbox 0.4 x 3.65 x 1.05 mm, 24 faces (baked)
FEATURE [Part::Feature] Part__Feature259  label="COMPOUND"
  Placement = pos=(0,-0.0056,0.0002) rot=(0,0,1;0rad)
  shape: bbox 18.9 x 15.9 x 13.25 mm, 232 faces (baked)
FEATURE [Part::Feature] Part__Feature260  label="COMPOUND001"
  Placement = pos=(0,-0.0056,0.0002) rot=(0,0,1;0rad)
  shape: bbox 0.4 x 3.65 x 1.05 mm, 24 faces (baked)
FEATURE [Part::Feature] Part__Feature261  label="COMPOUND002"
  Placement = pos=(0,-0.0056,0.0002) rot=(0,0,1;0rad)
  shape: bbox 0.4 x 3.65 x 1.05 mm, 24 faces (baked)
FEATURE [Part::Feature] Part__Feature262  label="COMPOUND004"
  Placement = pos=(0,-0.0056,0.0002) rot=(0,0,1;0rad)
  shape: bbox 0.4 x 3.65 x 1.05 mm, 24 faces (baked)
FEATURE [Part::Feature] Part__Feature263  label="COMPOUND005"
  Placement = pos=(0,-0.0056,0.0002) rot=(0,0,1;0rad)
  shape: bbox 0.4 x 3.65 x 1.05 mm, 24 faces (baked)
FEATURE [Part::Feature] Part__Feature264  label="COMPOUND006"
  Placement = pos=(0,-0.0056,0.0002) rot=(0,0,1;0rad)
  shape: bbox 0.4 x 3.65 x 1.05 mm, 24 faces (baked)
FEATURE [Part::Feature] Part__Feature265  label="COMPOUND007"
  Placement = pos=(0,-0.0056,0.0002) rot=(0,0,1;0rad)
  shape: bbox 0.4 x 3.65 x 1.05 mm, 24 faces (baked)
FEATURE [Part::Feature] Part__Feature266  label="COMPOUND008"
  Placement = pos=(0,-0.0056,0.0002) rot=(0,0,1;0rad)
  shape: bbox 0.4 x 3.65 x 1.05 mm, 24 faces (baked)
FEATURE [Part::Feature] Part__Feature267  label="COMPOUND009"
  Placement = pos=(0,-0.0056,0.0002) rot=(0,0,1;0rad)
  shape: bbox 15.81 x 15.25 x 13.95 mm, 39 faces (baked)
FEATURE [Part::Feature] Part__Feature268  label="COMPOUND010"
  Placement = pos=(0,-0.0056,0.0002) rot=(0,0,1;0rad)
  shape: bbox 0.4 x 11.61 x 3.651 mm, 6 faces (baked)
FEATURE [App::Part] COMPOUND  label="LAN"
  Group = -> [Part__Feature259,Part__Feature260,Part__Feature261,Part__Feature258,Part__Feature262,Part__Feature263,Part__Feature264,Part__Feature265,Part__Feature266,Part__Feature267,Part__Feature268,Part__Feature015,Part__Feature247,Part__Feature248,Part__Feature249,Part__Feature250,Part__Feature251,Part__Feature252]
  Origin = -> Origin008
  Placement = pos=(19.5,104.5,14.75) rot=(0,0,1;3.14159rad)
FEATURE [Part::Feature] Part__Feature269  label="USB3.1 TYPE-C 24PF-009 v6"
  shape: bbox 9.146 x 4.6 x 10.65 mm, 537 faces (baked)
FEATURE [Part::Feature] Part__Feature270  label="USB3.1 TYPE-C 24PF-009 v007"
  shape: bbox 8.34 x 3.8 x 10 mm, 300 faces (baked)
FEATURE [Part::Feature] Part__Feature271  label="USB3.1 TYPE-C 24PF-009 v008"
  shape: bbox 5.75 x 2.5 x 8.484 mm, 354 faces (baked)
FEATURE [Part::Feature] Part__Feature272  label="COMPOUND019"
  Placement = pos=(0,-0.0056,0.0002) rot=(0,0,1;0rad)
  shape: bbox 0.4 x 3.65 x 1.05 mm, 24 faces (baked)
FEATURE [Part::Feature] Part__Feature273  label="Antenna Mount"
  Placement = pos=(15,63,10.75) rot=(0,0,1;0rad)
  shape: bbox 9.247 x 12.26 x 8.009 mm, 76 faces (baked)
FEATURE [Part::Feature] Part__Feature274  label="COMPOUND020"
  Placement = pos=(0,-0.0056,0.0002) rot=(0,0,1;0rad)
  shape: bbox 18.9 x 15.9 x 13.25 mm, 232 faces (baked)
FEATURE [Part::Feature] Part__Feature275  label="COMPOUND021"
  Placement = pos=(0,-0.0056,0.0002) rot=(0,0,1;0rad)
  shape: bbox 0.4 x 3.65 x 1.05 mm, 24 faces (baked)
FEATURE [Part::Feature] Part__Feature276  label="COMPOUND022"
  Placement = pos=(0,-0.0056,0.0002) rot=(0,0,1;0rad)
  shape: bbox 0.4 x 3.65 x 1.05 mm, 24 faces (baked)
FEATURE [Part::Feature] Part__Feature277  label="COMPOUND023"
  Placement = pos=(0,-0.0056,0.0002) rot=(0,0,1;0rad)
  shape: bbox 0.4 x 3.65 x 1.05 mm, 24 faces (baked)
FEATURE [Part::Feature] Part__Feature278  label="COMPOUND024"
  Placement = pos=(0,-0.0056,0.0002) rot=(0,0,1;0rad)
  shape: bbox 0.4 x 3.65 x 1.05 mm, 24 faces (baked)
FEATURE [Part::Feature] Part__Feature279  label="COMPOUND025"
  Placement = pos=(0,-0.0056,0.0002) rot=(0,0,1;0rad)
  shape: bbox 0.4 x 3.65 x 1.05 mm, 24 faces (baked)
FEATURE [Part::Feature] Part__Feature280  label="COMPOUND026"
  Placement = pos=(0,-0.0056,0.0002) rot=(0,0,1;0rad)
  shape: bbox 0.4 x 3.65 x 1.05 mm, 24 faces (baked)
FEATURE [Part::Feature] Part__Feature281  label="COMPOUND027"
  Placement = pos=(0,-0.0056,0.0002) rot=(0,0,1;0rad)
  shape: bbox 0.4 x 3.65 x 1.05 mm, 24 faces (baked)
FEATURE [Part::Feature] Part__Feature282  label="COMPOUND028"
  Placement = pos=(0,-0.0056,0.0002) rot=(0,0,1;0rad)
  shape: bbox 15.81 x 15.25 x 13.95 mm, 39 faces (baked)
FEATURE [Part::Feature] Part__Feature283  label="COMPOUND029"
  Placement = pos=(0,-0.0056,0.0002) rot=(0,0,1;0rad)
  shape: bbox 0.4 x 11.61 x 3.651 mm, 6 faces (baked)
FEATURE [Part::Feature] Part__Feature284  label="COMPOUND030"
  Placement = pos=(0,-0.0056,0.0002) rot=(0,0,1;0rad)
  shape: bbox 0.4 x 11.61 x 3.651 mm, 6 faces (baked)
FEATURE [Part::Feature] Part__Feature285  label="COMPOUND031"
  Placement = pos=(0,-0.0056,0.0002) rot=(0,0,1;0rad)
  shape: bbox 0.4 x 11.61 x 3.651 mm, 6 faces (baked)
FEATURE [Part::Feature] Part__Feature286  label="COMPOUND032"
  Placement = pos=(0,-0.0056,0.0002) rot=(0,0,1;0rad)
  shape: bbox 0.4 x 11.61 x 3.651 mm, 6 faces (baked)
FEATURE [Part::Feature] Part__Feature287  label="COMPOUND033"
  Placement = pos=(0,-0.0056,0.0002) rot=(0,0,1;0rad)
  shape: bbox 0.4 x 11.61 x 3.651 mm, 6 faces (baked)
FEATURE [Part::Feature] Part__Feature288  label="COMPOUND034"
  Placement = pos=(0,-0.0056,0.0002) rot=(0,0,1;0rad)
  shape: bbox 0.4 x 11.61 x 3.651 mm, 6 faces (baked)
FEATURE [Part::Feature] Part__Feature289  label="COMPOUND035"
  Placement = pos=(0,-0.0056,0.0002) rot=(0,0,1;0rad)
  shape: bbox 0.4 x 11.61 x 3.651 mm, 6 faces (baked)
FEATURE [Part::Feature] Part__Feature290  label="COMPOUND036"
  Placement = pos=(0,-0.0056,0.0002) rot=(0,0,1;0rad)
  shape: bbox 0.4 x 11.61 x 3.651 mm, 6 faces (baked)
FEATURE [App::Part] COMPOUND001  label="COMPOUND018"
  Group = -> [Part__Feature274,Part__Feature275,Part__Feature276,Part__Feature272,Part__Feature277,Part__Feature278,Part__Feature279,Part__Feature280,Part__Feature281,Part__Feature282,Part__Feature283,Part__Feature284,Part__Feature285,Part__Feature286,Part__Feature287,Part__Feature288,Part__Feature289,Part__Feature290]
  Origin = -> Origin029
  Placement = pos=(48.5,5.5,19.25) rot=(0,1,0;3.14159rad)
FEATURE [Part::Feature] Part__Feature291  label="USB-type-A(USBR-A-S-F-O-VU)"
  Placement = pos=(71.75,7.25,6.75) rot=(1,0,0;1.5708rad)
  shape: bbox 18.32 x 19.2 x 7.2 mm, 244 faces (baked)
FEATURE [Sketcher::SketchObject] Sketch001
  ArcFitTolerance = 0
  FullyConstrained = true
  MakeInternals = false
  Placement = pos=(0,0,0) rot=(1,0,0;3.14159rad)
  sketch-geometry (18):
    g0: ArcOfCircle CenterX=10.5 CenterY=-21.5 CenterZ=0 NormalX=0 NormalY=0 NormalZ=1 AngleXU=0 Radius=1.875 StartAngle=1.5708 EndAngle=4.71239
    g1: LineSegment StartX=10.5 StartY=-23.375 StartZ=0 EndX=13.04 EndY=-23.375 EndZ=0
    g2: LineSegment StartX=13.0446 StartY=-19.625 StartZ=0 EndX=10.5 EndY=-19.625 EndZ=0
    g3: ArcOfCircle CenterX=21.5 CenterY=-21.5 CenterZ=0 NormalX=0 NormalY=0 NormalZ=1 AngleXU=0 Radius=1.875 StartAngle=4.71239 EndAngle=7.85398
    g4: LineSegment StartX=18.9564 StartY=-23.375 StartZ=0 EndX=21.5 EndY=-23.375 EndZ=0
    g5: LineSegment StartX=21.5 StartY=-19.625 StartZ=0 EndX=18.9554 EndY=-19.625 EndZ=0
    g6: ArcOfCircle CenterX=55.25 CenterY=-77.5 CenterZ=0 NormalX=0 NormalY=0 NormalZ=1 AngleXU=0 Radius=1.875 StartAngle=1.5708 EndAngle=4.71239
    g7: LineSegment StartX=55.25 StartY=-79.375 StartZ=0 EndX=57.7946 EndY=-79.375 EndZ=0
    g8: LineSegment StartX=57.7946 StartY=-75.625 StartZ=0 EndX=55.25 EndY=-75.625 EndZ=0
    g9: ArcOfCircle CenterX=66.25 CenterY=-77.5 CenterZ=0 NormalX=0 NormalY=0 NormalZ=1 AngleXU=0 Radius=1.875 StartAngle=4.71239 EndAngle=7.85398
    g10: LineSegment StartX=63.71 StartY=-79.375 StartZ=0 EndX=66.25 EndY=-79.375 EndZ=0
    g11: LineSegment StartX=66.25 StartY=-75.625 StartZ=0 EndX=63.7054 EndY=-75.625 EndZ=0
    g12: ArcOfCircle CenterX=60.75 CenterY=-77.5 CenterZ=0 NormalX=0 NormalY=0 NormalZ=1 AngleXU=0 Radius=3.5 StartAngle=0.565353 EndAngle=2.57624
    g13: ArcOfCircle CenterX=60.7523 CenterY=-77.5036 CenterZ=0 NormalX=0 NormalY=0 NormalZ=1 AngleXU=0 Radius=3.5 StartAngle=3.70572 EndAngle=5.71906
    g14: ArcOfCircle CenterX=16 CenterY=-21.5 CenterZ=0 NormalX=0 NormalY=0 NormalZ=1 AngleXU=0 Radius=3.5 StartAngle=0.565353 EndAngle=2.57624
    g15: ArcOfCircle CenterX=15.9982 CenterY=-21.5044 CenterZ=0 NormalX=0 NormalY=0 NormalZ=1 AngleXU=0 Radius=3.5 StartAngle=3.70545 EndAngle=5.71932
    g16: Circle CenterX=16 CenterY=-21.5 CenterZ=0 NormalX=0 NormalY=0 NormalZ=1 AngleXU=0 Radius=0.05
    g17: Circle CenterX=60.75 CenterY=-77.5 CenterZ=0 NormalX=0 NormalY=0 NormalZ=1 AngleXU=0 Radius=0.05
  constraints (52):
    c: Tangent(g0,g1) = -1.5708
    c: Tangent(g2,g0) = -1.5708
    c: Horizontal(g1)
    c: DistanceY(g0,g0) = 3.75
    c: Distance(g0,g-1) = 21.5
    c: Horizontal(g2)
    c: Tangent(g4,g3) = -1.5708
    c: Tangent(g3,g5) = -1.5708
    c: Horizontal(g4)
    c: Distance(g3,g3) = 3.75
    c: Distance(g3,g-1) = 21.5
    c: Horizontal(g5)
    c: Tangent(g6,g7) = -1.5708
    c: Tangent(g8,g6) = -1.5708
    c: Horizontal(g7)
    c: Tangent(g10,g9) = -1.5708
    c: Tangent(g9,g11) = -1.5708
    c: Horizontal(g10)
    c: Distance(g6,g-1) = 77.5
    c: Distance(g9,g-1) = 77.5
    c: Horizontal(g11)
    c: Distance(g9,g9) = 3.75
    c: Distance(g6,g6) = 3.75
    c: Horizontal(g8)
    c: Coincident(g12,g8)
    c: Coincident(g12,g11)
    c: Diameter(g12) = 7
    c: Coincident(g13,g7)
    c: Coincident(g13,g10)
    c: Diameter(g13) = 7
    c: Distance(g12,g-1) = 77.5
    c: Distance(g12,g-2) = 60.75
    c: Distance(g7,g8) = 3.75
    c: Distance(g9,g-2) = 66.25
    c: Distance(g6,g-2) = 55.25
    c: Distance(g10,g-2) = 63.71
    c: Coincident(g14,g2)
    c: Coincident(g14,g5)
    c: Coincident(g15,g1)
    c: Coincident(g15,g4)
    c: Diameter(g14) = 7
    c: Diameter(g15) = 7
    c: Distance(g14,g-1) = 21.5
    c: Distance(g14,g-2) = 16
    c: Distance(g1,g-2) = 13.04
    c: Distance(g0,g-2) = 10.5
    c: Distance(g3,g-2) = 21.5
    c: Distance(g4,g3) = 3.16
    c: Coincident(g16,g14)
    c: Diameter(g16) = 0.1
    c: Coincident(g17,g12)
    c: Diameter(g17) = 0.1
FEATURE [Part::Extrusion] Extrude001
  Base = -> Sketch001
  Dir = (0,0,-1)
  DirMode = 2
  FaceMakerClass = Part::FaceMakerBullseye
  FaceMakerMode = 3
  LengthFwd = 2
  LengthRev = 0
  Placement = pos=(0,0,2) rot=(0,0,1;0rad)
  Solid = true
  Symmetric = false
FEATURE [Part::Cut] Cut010
  Base = -> Fusion007
  Tool = -> Extrude001
FEATURE [Sketcher::SketchObject] Sketch002
  ArcFitTolerance = 0
  FullyConstrained = true
  MakeInternals = false
  sketch-geometry (16):
    g0: LineSegment StartX=-65 StartY=157.37 StartZ=0 EndX=65 EndY=157.37 EndZ=0
    g1: LineSegment StartX=-65 StartY=157.37 StartZ=0 EndX=-65 EndY=147.37 EndZ=0
    g2: LineSegment StartX=-65 StartY=147.37 StartZ=0 EndX=-45.68 EndY=147.37 EndZ=0
    g3: LineSegment StartX=-45.68 StartY=147.37 StartZ=0 EndX=-45.68 EndY=70.37 EndZ=0
    g4: LineSegment StartX=-45.68 StartY=70.37 StartZ=0 EndX=-35.68 EndY=70.37 EndZ=0
    g5: LineSegment StartX=-35.68 StartY=70.37 StartZ=0 EndX=-35.68 EndY=147.37 EndZ=0
    g6: LineSegment StartX=-35.68 StartY=147.37 StartZ=0 EndX=-8 EndY=147.37 EndZ=0
    g7: LineSegment StartX=-8 StartY=147.37 StartZ=0 EndX=-8 EndY=70.37 EndZ=0
    g8: LineSegment StartX=-8 StartY=70.37 StartZ=0 EndX=8 EndY=70.37 EndZ=0
    g9: LineSegment StartX=8 StartY=70.37 StartZ=0 EndX=8 EndY=147.37 EndZ=0
    g10: LineSegment StartX=8 StartY=147.37 StartZ=0 EndX=35.68 EndY=147.37 EndZ=0
    g11: LineSegment StartX=35.68 StartY=147.37 StartZ=0 EndX=35.68 EndY=70.37 EndZ=0
    g12: LineSegment StartX=35.68 StartY=70.37 StartZ=0 EndX=45.68 EndY=70.37 EndZ=0
    g13: LineSegment StartX=45.68 StartY=70.37 StartZ=0 EndX=45.68 EndY=147.37 EndZ=0
    g14: LineSegment StartX=45.68 StartY=147.37 StartZ=0 EndX=65 EndY=147.37 EndZ=0
    g15: LineSegment StartX=65 StartY=147.37 StartZ=0 EndX=65 EndY=157.37 EndZ=0
  constraints (44):
    c: Symmetric(g0,g0,g-2)
    c: Distance(g0) = 130
    c: Coincident(g1,g0)
    c: Vertical(g1)
    c: Coincident(g2,g1)
    c: Horizontal(g2)
    c: Vertical(g3)
    c: Coincident(g4,g3)
    c: Horizontal(g4)
    c: Coincident(g5,g4)
    c: Vertical(g5)
    c: Coincident(g6,g5)
    c: Horizontal(g6)
    c: Coincident(g7,g6)
    c: Vertical(g7)
    c: Coincident(g8,g7)
    c: Horizontal(g8)
    c: Coincident(g9,g8)
    c: Vertical(g9)
    c: Coincident(g10,g9)
    c: Coincident(g11,g10)
    c: Vertical(g11)
    c: Coincident(g12,g11)
    c: Horizontal(g12)
    c: Coincident(g13,g12)
    c: Vertical(g13)
    c: Coincident(g14,g13)
    c: Horizontal(g14)
    c: Coincident(g15,g14)
    c: Coincident(g15,g0)
    c: Vertical(g15)
    c: Symmetric(g6,g9,g-2)
    c: Symmetric(g5,g10,g-2)
    c: Symmetric(g2,g13,g-2)
    c: Coincident(g2,g3)
    c: Distance(g2,g0) = 10
    c: Distance(g5,g0) = 10
    c: Distance(g3) = 77
    c: Distance(g4) = 10
    c: Distance(g8) = 16
    c: Distance(g9) = 77
    c: Distance(g13) = 77
    c: Distance(g1,g-1) = 147.37
    c: Distance(g3,g-2) = 45.68
FEATURE [Part::Extrusion] Extrude002  label="Side__hold"
  Base = -> Sketch002
  Dir = (0,0,1)
  DirMode = 2
  FaceMakerClass = Part::FaceMakerBullseye
  FaceMakerMode = 3
  LengthFwd = 10
  LengthRev = 0
  Placement = pos=(0,0.63,-1.5) rot=(0,0,1;0rad)
  Reversed = true
  Solid = true
  Symmetric = false
FEATURE [Part::MultiFuse] Fusion011  label="Holder"
  Shapes = -> [Extrude002,Box024,Box025,Box026,Box027,Box028]
FEATURE [Part::Fillet] Fillet012  label="Holder_fillet"
  Base = -> Fusion011
  EdgeLinks = -> Fusion011 [Edge1,Edge2,Edge3,Edge7,Edge8,Edge10,Edge11,Edge13,Edge14,Edge15,Edge16,Edge17,Edge18,Edge19,Edge20,Edge21,Edge22,Edge23,Edge24,Edge25,Edge26,Edge28,Edge29,Edge32,Edge36,Edge40,Edge43,Edge44,Edge45,Edge47,Edge49,Edge50,Edge51,Edge53,Edge54,Edge59,Edge61,Edge66,Edge68,Edge74,+15 more]
  Edges = 55 edges: [Edge1 r=1,Edge2 r=1,Edge3 r=1,Edge7 r=1,Edge8 r=4,Edge10 r=1,Edge11 r=4,Edge13 r=1,Edge14 r=1,Edge15 r=4,Edge16 r=1,Edge17 r=1,Edge18 r=1,Edge19 r=4,Edge20 r=1,Edge21 r=1,Edge22 r=1,Edge23 r=4,Edge24 r=1,Edge25 r=1,Edge26 r=1,Edge28 r=1,Edge29 r=4,Edge32 r=3,Edge36 r=3,Edge40 r=3,Edge43 r=4,Edge44 r=1,Edge45 r=1,Edge47 r=4,Edge49 r=1,Edge50 r=1,Edge51 r=4,Edge53 r=1,Edge54 r=1,Edge59 r=4,Edge61 r=4,Edge66 r=4,Edge68 r=4,Edge74 r=1,Edge75 r=1,Edge78 r=1,Edge79 r=1,Edge82 r=1,Edge85 r=1,Edge88 r=1,Edge90 r=1,Edge91 r=1,Edge93 r=1,Edge95 r=1,Edge96 r=1,Edge98 r=1,Edge100 r=1,Edge101 r=1,+1 more]
FEATURE [Part::Cut] Cut017  label="eZ_Holder"
  Base = -> Fillet012
  Tool = -> Fusion012
FEATURE [App::Part] Part006  label="ezOutlet_holder"
  Group = -> [Box026,Fillet012,Fusion011,Cylinder020,Cylinder019,Cylinder021,Cylinder022,Extrude002,Box028,Fusion012,Box024,Box027,Box025,Sketch002,Cut017]
  Origin = -> Origin030
  Placement = pos=(0,0,-157) rot=(0,0,1;0rad)
FEATURE [Sketcher::SketchObject] Sketch003
  ArcFitTolerance = 0
  FullyConstrained = true
  MakeInternals = false
  sketch-geometry (16):
    g0: LineSegment StartX=-70.5 StartY=157.37 StartZ=0 EndX=70.5 EndY=157.37 EndZ=0
    g1: LineSegment StartX=-70.5 StartY=157.37 StartZ=0 EndX=-70.5 EndY=147.37 EndZ=0
    g2: LineSegment StartX=-70.5 StartY=147.37 StartZ=0 EndX=-50 EndY=147.37 EndZ=0
    g3: LineSegment StartX=-50 StartY=147.37 StartZ=0 EndX=-50 EndY=27.37 EndZ=0
    g4: LineSegment StartX=-50 StartY=27.37 StartZ=0 EndX=-35 EndY=27.37 EndZ=0
    g5: LineSegment StartX=-35 StartY=27.37 StartZ=0 EndX=-35 EndY=147.37 EndZ=0
    g6: LineSegment StartX=-35 StartY=147.37 StartZ=0 EndX=-8 EndY=147.37 EndZ=0
    g7: LineSegment StartX=-8 StartY=147.37 StartZ=0 EndX=-8 EndY=27.37 EndZ=0
    g8: LineSegment StartX=-8 StartY=27.37 StartZ=0 EndX=8 EndY=27.37 EndZ=0
    g9: LineSegment StartX=8 StartY=27.37 StartZ=0 EndX=8 EndY=147.37 EndZ=0
    g10: LineSegment StartX=8 StartY=147.37 StartZ=0 EndX=35 EndY=147.37 EndZ=0
    g11: LineSegment StartX=35 StartY=147.37 StartZ=0 EndX=35 EndY=27.37 EndZ=0
    g12: LineSegment StartX=35 StartY=27.37 StartZ=0 EndX=50 EndY=27.37 EndZ=0
    g13: LineSegment StartX=50 StartY=27.37 StartZ=0 EndX=50 EndY=147.37 EndZ=0
    g14: LineSegment StartX=50 StartY=147.37 StartZ=0 EndX=70.5 EndY=147.37 EndZ=0
    g15: LineSegment StartX=70.5 StartY=147.37 StartZ=0 EndX=70.5 EndY=157.37 EndZ=0
  constraints (44):
    c: Symmetric(g0,g0,g-2)
    c: Distance(g0) = 141
    c: Coincident(g1,g0)
    c: Vertical(g1)
    c: Coincident(g2,g1)
    c: Horizontal(g2)
    c: Vertical(g3)
    c: Coincident(g4,g3)
    c: Horizontal(g4)
    c: Coincident(g5,g4)
    c: Vertical(g5)
    c: Coincident(g6,g5)
    c: Horizontal(g6)
    c: Coincident(g7,g6)
    c: Vertical(g7)
    c: Coincident(g8,g7)
    c: Horizontal(g8)
    c: Coincident(g9,g8)
    c: Vertical(g9)
    c: Coincident(g10,g9)
    c: Coincident(g11,g10)
    c: Vertical(g11)
    c: Coincident(g12,g11)
    c: Horizontal(g12)
    c: Coincident(g13,g12)
    c: Vertical(g13)
    c: Coincident(g14,g13)
    c: Horizontal(g14)
    c: Coincident(g15,g14)
    c: Coincident(g15,g0)
    c: Vertical(g15)
    c: Symmetric(g6,g9,g-2)
    c: Symmetric(g5,g10,g-2)
    c: Symmetric(g2,g13,g-2)
    c: Coincident(g2,g3)
    c: Distance(g2,g0) = 10
    c: Distance(g5,g0) = 10
    c: Distance(g3) = 120
    c: Distance(g4) = 15
    c: Distance(g8) = 16
    c: Distance(g9) = 120
    c: Distance(g13) = 120
    c: Distance(g1,g-1) = 147.37
    c: Distance(g3,g-2) = 50
FEATURE [Part::Extrusion] Extrude003  label="Side__hold001"
  Base = -> Sketch003
  Dir = (0,0,1)
  DirMode = 2
  FaceMakerClass = Part::FaceMakerBullseye
  FaceMakerMode = 3
  LengthFwd = 10
  LengthRev = 0
  Placement = pos=(0,0.63,-1.5) rot=(0,0,1;0rad)
  Reversed = true
  Solid = true
  Symmetric = false
FEATURE [Part::MultiFuse] Fusion013  label="Holder_gateway"
  Shapes = -> [Extrude003,Box029,Box030,Box031,Box032,Box033]
FEATURE [Part::Cut] Cut018  label="Holder_m3_cut"
  Base = -> Fusion013
  Tool = -> Fusion014
FEATURE [Part::Fillet] Fillet013  label="GateWay_Holder"
  Base = -> Cut018
  EdgeLinks = -> Cut018 [Edge1,Edge2,Edge4,Edge12,Edge14,Edge15,Edge16,Edge17,Edge18,Edge19,Edge20,Edge21,Edge22,Edge23,Edge24,Edge25,Edge26,Edge27,Edge28,Edge30,Edge48,Edge49,Edge60,Edge61,Edge63,Edge64,Edge70,Edge72,Edge77,Edge79,Edge85,Edge86,Edge89,Edge91,Edge94,Edge95,Edge98,Edge101,Edge104,Edge105,+10 more]
  Edges = 50 edges: [Edge1 r=1,Edge2 r=1,Edge4 r=1,Edge12 r=4,Edge14 r=4,Edge15 r=1,Edge16 r=1,Edge17 r=4,Edge18 r=1,Edge19 r=1,Edge20 r=1,Edge21 r=4,Edge22 r=1,Edge23 r=1,Edge24 r=1,Edge25 r=4,Edge26 r=1,Edge27 r=1,Edge28 r=1,Edge30 r=1,Edge48 r=1,Edge49 r=1,Edge60 r=4,Edge61 r=1,Edge63 r=1,Edge64 r=4,Edge70 r=4,Edge72 r=4,Edge77 r=4,Edge79 r=4,Edge85 r=1,Edge86 r=1,Edge89 r=1,Edge91 r=1,Edge94 r=1,Edge95 r=1,Edge98 r=1,Edge101 r=1,Edge104 r=1,Edge105 r=4,Edge106 r=4,Edge108 r=1,Edge109 r=1,Edge111 r=1,Edge113 r=1,Edge114 r=1,Edge116 r=1,Edge118 r=1,Edge119 r=1,Edge121 r=1]
FEATURE [App::Part] Part007  label="LoRa_Gateway_holder"
  Group = -> [Cylinder024,Cylinder026,Cylinder023,Cylinder025,Extrude003,Fusion013,Fusion014,Sketch003,Box030,Box029,Box031,Box033,Box032,Cut018,Fillet013]
  Origin = -> Origin031
  Placement = pos=(132.3,0,-10) rot=(0,1,0;4.71239rad)
FEATURE [App::Part] Solid3  label="Solid006"
  Group = -> [Part__Feature005,Part__Feature006,Part__Feature007]
  Origin = -> Origin002
FEATURE [App::Part] Solid4  label="Solid010"
  Group = -> [Part__Feature008,Part__Feature009,Part__Feature010,Part__Feature011]
  Origin = -> Origin023
FEATURE [Part::Torus] Torus
  Angle1 = -180
  Angle2 = 180
  Angle3 = 290
  AttacherType = Attacher::AttachEngine3D
  Placement = pos=(61,31,37) rot=(0,0,1;2.18166rad)
  Radius1 = 3
  Radius2 = 0.25
FEATURE [Part::MultiFuse] Fusion006  label="Power_button"
  Shapes = -> [Torus,Cylinder005]
FEATURE [App::Part] USB3_1_TYPE_C_24PF_009_v6  label="USB3.1 TYPE-C 24PF-009 v009"
  Group = -> [Part__Feature269,Part__Feature270,Part__Feature271]
  Origin = -> Origin028
  Placement = pos=(26,9.3,7.5) rot=(1,0,0;1.5708rad)
FEATURE [App::Part] Part005  label="LoRa_Gateway"
  Group = -> [Cylinder007,Part__Feature273,Cylinder009,Cylinder008,Cut011,USB3_1_TYPE_C_24PF_009_v6,COMPOUND001,Part__Feature291,Box021,Box019,Cut015,Cut012,Cut016,Box020,Cylinder010,Cylinder012,Cylinder011,Cylinder017,Cylinder013,Cylinder014,Cylinder015,Cylinder016,Cylinder018,Box023,Fusion010,Box022,Fillet010,Fillet009,Cut013,Fusion002,Cut014,Fusion008,Fusion009,Fillet008,Fusion004,Fillet011]
  Origin = -> Origin027
  Placement = pos=(174,156,-70) rot=(0.57735,-0.57735,-0.57735;2.0944rad)
FEATURE [App::Part] Unnamed1  label="Power_out"
  Group = -> [Part__Feature,Part__Feature001,Part__Feature002,Part__Feature003]
  Origin = -> Origin022
  Placement = pos=(39.25,1.75,18.5) rot=(-0.57735,-0.57735,0.57735;4.18879rad)
FEATURE [App::Part] power_input_swuitch  label="power input swuitch"
  Group = -> [Solid3,Solid4,FUSE,Part__Feature253,FUSE__1_,Cut004,Cut003,Box015,Part__Feature004,Box004,Box003,Cut005]
  Origin = -> Origin026
  Placement = pos=(39.25,109,18.5) rot=(-0.57735,-0.57735,-0.57735;2.0944rad)
FEATURE [App::Part] Part004  label="eZOutlet5"
  Group = -> [Unnamed1,Cylinder006,Torus,Cylinder005,Fusion006,power_input_swuitch,COMPOUND,Cut006,Fillet003,Fillet005,Fillet006,Fillet007,Sketch001,Box006,Box007,Box018,Box016,Box017,Extrude001,Fillet004,Cut008,Cut009,Cut007,Box014,Box005,Box013,Cut001,Cut002,Fusion007,Cylinder004,Cut010]
  Origin = -> Origin
  Placement = pos=(54.5,79,-206) rot=(0,0,1;1.5708rad)
FEATURE [Part::Feature] Part__Feature195  label="CUI_VGS-25W-060"
  shape: bbox 6 x 13.55 x 11.3 mm, 86 faces (baked)
FEATURE [Part::Feature] Part__Feature196  label="CUI_VGS-25W-061"
  shape: bbox 55.03 x 25.15 x 80 mm, 254 faces (baked)
FEATURE [Part::Feature] Part__Feature197  label="CUI_VGS-25W-062"
  shape: bbox 7.911 x 7.911 x 1.162 mm, 68 faces (baked)
FEATURE [Part::Feature] Part__Feature198  label="CUI_VGS-25W-063"
  shape: bbox 5.629 x 5.629 x 8.001 mm, 43 faces (baked)
FEATURE [Part::Feature] Part__Feature199  label="CUI_VGS-25W-064"
  shape: bbox 4.944 x 5.8 x 5.8 mm, 37 faces (baked)
FEATURE [Part::Feature] Part__Feature200  label="CUI_VGS-25W-065"
  shape: bbox 6 x 13.55 x 11.3 mm, 86 faces (baked)
FEATURE [Part::Feature] Part__Feature201  label="CUI_VGS-25W-066"
  shape: bbox 5.629 x 5.629 x 8.001 mm, 43 faces (baked)
FEATURE [Part::Feature] Part__Feature202  label="CUI_VGS-25W-067"
  shape: bbox 39.6 x 12 x 16 mm, 290 faces (baked)
FEATURE [Part::Feature] Part__Feature203  label="CUI_VGS-25W-068"
  shape: bbox 5.443 x 12.7 x 3.793 mm, 44 faces (baked)
FEATURE [Part::Feature] Part__Feature204  label="CUI_VGS-25W-069"
  shape: bbox 54.37 x 24.2 x 80.19 mm, 487 faces (baked)
FEATURE [Part::Feature] Part__Feature205  label="CUI_VGS-25W-070"
  shape: bbox 6 x 13.55 x 11.3 mm, 86 faces (baked)
FEATURE [Part::Feature] Part__Feature206  label="CUI_VGS-25W-071"
  shape: bbox 5.413 x 8.147 x 5.557 mm, 54 faces (baked)
FEATURE [Part::Feature] Part__Feature207  label="CUI_VGS-25W-072"
  shape: bbox 6 x 13.55 x 11.3 mm, 86 faces (baked)
FEATURE [Part::Feature] Part__Feature208  label="CUI_VGS-25W-073"
  shape: bbox 9.096 x 12.71 x 7.718 mm, 112 faces (baked)
FEATURE [Part::Feature] Part__Feature209  label="CUI_VGS-25W-074"
  shape: bbox 6 x 13.55 x 11.3 mm, 86 faces (baked)
FEATURE [Part::Feature] Part__Feature210  label="CUI_VGS-25W-075"
  shape: bbox 5.629 x 5.629 x 8.001 mm, 43 faces (baked)
FEATURE [Part::Feature] Part__Feature211  label="CUI_VGS-25W-076"
  shape: bbox 5.629 x 5.629 x 8.001 mm, 43 faces (baked)
FEATURE [Part::Feature] Part__Feature212  label="CUI_VGS-25W-077"
  shape: bbox 7.911 x 7.911 x 1.162 mm, 68 faces (baked)
FEATURE [Part::Feature] Part__Feature213  label="CUI_VGS-25W-078"
  shape: bbox 7.911 x 7.911 x 1.162 mm, 68 faces (baked)
FEATURE [Part::Feature] Part__Feature214  label="CUI_VGS-25W-079"
  shape: bbox 7 x 0.55 x 7 mm, 6 faces (baked)
FEATURE [Part::Feature] Part__Feature215  label="CUI_VGS-25W-080"
  shape: bbox 53.1 x 22.4 x 79.2 mm, 72 faces (baked)
FEATURE [Part::Feature] Part__Feature216  label="CUI_VGS-25W-081"
  shape: bbox 4.624 x 1.433 x 4.618 mm, 8 faces (baked)
FEATURE [Part::Feature] Part__Feature217  label="CUI_VGS-25W-082"
  shape: bbox 7.911 x 7.911 x 1.162 mm, 68 faces (baked)
FEATURE [Part::Feature] Part__Feature218  label="CUI_VGS-25W-083"
  shape: bbox 5.629 x 5.629 x 8.001 mm, 43 faces (baked)
FEATURE [Part::Feature] Part__Feature219  label="CUI_VGS-25W-084"
  shape: bbox 52.65 x 1.621 x 78.18 mm, 385 faces (baked)
FEATURE [Part::Feature] Part__Feature220  label="CUI_VGS-25W-085"
  shape: bbox 7.911 x 7.911 x 1.162 mm, 68 faces (baked)
FEATURE [App::Part] CUI_VGS_25W_007  label="CUI_VGS-25W-01"
  Group = -> [Part__Feature201,Part__Feature202,Part__Feature203,Part__Feature204,Part__Feature205,Part__Feature206,Part__Feature207,Part__Feature208,Part__Feature209,Part__Feature210,Part__Feature195,Part__Feature196,Part__Feature197,Part__Feature198,Part__Feature199,Part__Feature200,Part__Feature211,Part__Feature212,Part__Feature213,Part__Feature214,Part__Feature217,Part__Feature215,Part__Feature216,+3 more]
  Origin = -> Origin020
  Placement = pos=(22.5,-50.5,0.25) rot=(1,0,0;1.5708rad)
FEATURE [Sketcher::SketchObject] Sketch004
  ArcFitTolerance = 1e-06
  FullyConstrained = true
  MakeInternals = false
  Placement = pos=(0,0,0) rot=(1,0,0;1.5708rad)
  sketch-geometry (6):
    g0: LineSegment StartX=25 StartY=0 StartZ=0 EndX=25 EndY=-4 EndZ=0
    g1: LineSegment StartX=25 StartY=-4 StartZ=0 EndX=59.5 EndY=-4 EndZ=0
    g2: LineSegment StartX=59.5 StartY=-4 StartZ=0 EndX=59.5 EndY=21 EndZ=0
    g3: LineSegment StartX=59.5 StartY=21 StartZ=0 EndX=55.5 EndY=21 EndZ=0
    g4: LineSegment StartX=55.5 StartY=21 StartZ=0 EndX=55.5 EndY=0 EndZ=0
    g5: LineSegment StartX=55.5 StartY=0 StartZ=0 EndX=25 EndY=0 EndZ=0
  constraints (18):
    c: Coincident(g1,g0)
    c: Horizontal(g1)
    c: Vertical(g2)
    c: Coincident(g3,g2)
    c: Horizontal(g3)
    c: PointOnObject(g4,g-1)
    c: Vertical(g4)
    c: Coincident(g5,g4)
    c: Coincident(g5,g0)
    c: Horizontal(g5)
    c: Vertical(g0)
    c: Coincident(g1,g2)
    c: DistanceX(g0) = 25
    c: DistanceX(g5,g5) = 30.5
    c: DistanceX(g3,g3) = 4
    c: Coincident(g3,g4)
    c: DistanceY(g0,g0) = 4
    c: DistanceY(g2,g2) = 25
FEATURE [Part::Extrusion] Extrude004
  Base = -> Sketch004
  Dir = (0,-1,2e-16)
  DirMode = 2
  FaceMakerClass = Part::FaceMakerBullseye
  FaceMakerMode = 3
  LengthFwd = 20
  LengthRev = 0
  Solid = true
  Symmetric = false
FEATURE [Sketcher::SketchObject] Sketch005
  ArcFitTolerance = 1e-06
  FullyConstrained = true
  MakeInternals = false
  Placement = pos=(0,0,0) rot=(1,0,0;1.5708rad)
  sketch-geometry (6):
    g0: LineSegment StartX=73 StartY=21 StartZ=0 EndX=25 EndY=21 EndZ=0
    g1: LineSegment StartX=25 StartY=21 StartZ=0 EndX=25 EndY=-4 EndZ=0
    g2: LineSegment StartX=25 StartY=-4 StartZ=0 EndX=73 EndY=-4 EndZ=0
    g3: LineSegment StartX=73 StartY=-4 StartZ=0 EndX=73 EndY=21 EndZ=0
    g4: Circle CenterX=67 CenterY=15 CenterZ=0 NormalX=0 NormalY=0 NormalZ=1 AngleXU=0 Radius=1.625
    g5: Circle CenterX=67 CenterY=2 CenterZ=0 NormalX=0 NormalY=0 NormalZ=1 AngleXU=0 Radius=1.625
  constraints (18):
    c: Horizontal(g0)
    c: Vertical(g1)
    c: DistanceX(g0,g0) = 48
    c: DistanceX(g1) = 25
    c: Coincident(g2,g1)
    c: Coincident(g3,g2)
    c: Coincident(g3,g0)
    c: Vertical(g3)
    c: DistanceY(g1,g1) = 25
    c: Horizontal(g2)
    c: DistanceY(g1) = -4
    c: Coincident(g0,g1)
    c: Equal(g4,g5)
    c: Diameter(g4) = 3.25
    c: Vertical(g5,g4)
    c: DistanceY(g1,g5) = 6
    c: DistanceY(g5,g4) = 13
    c: DistanceX(g1,g5) = 42
FEATURE [Part::Extrusion] Extrude005
  Base = -> Sketch005
  Dir = (0,-1,2e-16)
  DirMode = 2
  FaceMakerClass = Part::FaceMakerBullseye
  FaceMakerMode = 3
  LengthFwd = 5
  LengthRev = 0
  Solid = true
  Symmetric = false
FEATURE [Part::MultiFuse] Fusion015
  Shapes = -> [Extrude005,Extrude004]
FEATURE [Sketcher::SketchObject] Sketch006
  ArcFitTolerance = 1e-06
  FullyConstrained = true
  MakeInternals = false
  sketch-geometry (1):
    g0: Circle CenterX=29.75 CenterY=-15.85 CenterZ=0 NormalX=0 NormalY=0 NormalZ=1 AngleXU=0 Radius=1.625
  constraints (3):
    c: DistanceX(g0) = 29.75
    c: DistanceY(g0) = -15.85
    c: Diameter(g0) = 3.25
FEATURE [Part::Extrusion] Extrude006
  Base = -> Sketch006
  Dir = (0,0,1)
  DirMode = 2
  FaceMakerClass = Part::FaceMakerBullseye
  FaceMakerMode = 3
  LengthFwd = 10
  LengthRev = 0
  Reversed = true
  Solid = true
  Symmetric = false
FEATURE [Sketcher::SketchObject] Sketch007
  ArcFitTolerance = 1e-06
  FullyConstrained = true
  MakeInternals = false
  Placement = pos=(0,0,0) rot=(0.57735,0.57735,0.57735;2.0944rad)
  sketch-geometry (1):
    g0: Circle CenterX=-8.1 CenterY=14.25 CenterZ=0 NormalX=0 NormalY=0 NormalZ=1 AngleXU=0 Radius=1.625
  constraints (3):
    c: DistanceX(g0) = -8.1
    c: DistanceY(g0) = 14.25
    c: Diameter(g0) = 3.25
FEATURE [Part::Extrusion] Extrude007
  Base = -> Sketch007
  Dir = (1,0,0)
  DirMode = 2
  FaceMakerClass = Part::FaceMakerBullseye
  FaceMakerMode = 3
  LengthFwd = 75
  LengthRev = 0
  Solid = true
  Symmetric = false
FEATURE [Part::MultiFuse] Fusion016  label="cuts"
  Shapes = -> [Extrude006,Extrude007]
FEATURE [Part::Cut] Cut019
  Base = -> Fusion015
  Tool = -> Fusion016
FEATURE [Part::Fillet] Fillet014
  Base = -> Cut019
  EdgeLinks = -> Cut019 [Edge30,Edge33,Edge44,Edge46,Edge47,Edge48]
  Edges = 6 edges r=1: [Edge30,Edge33,Edge44,Edge46,Edge47,Edge48]
FEATURE [Part::Fillet] Fillet001
  Base = -> Fillet014
  EdgeLinks = -> Fillet014 [Edge41,Edge47,Edge48]
  Edges = 3 edges r=1: [Edge41,Edge47,Edge48]
FEATURE [Part::Fillet] Fillet002
  Base = -> Fillet001
  EdgeLinks = -> Fillet001 [Edge15,Edge38,Edge46,Edge47]
  Edges = 4 edges r=0.25: [Edge15,Edge38,Edge46,Edge47]
FEATURE [Part::Compound] Compound  label="5vHolder"
  Links = -> [CUI_VGS_25W_007,Fillet002]
  Placement = pos=(130,158,-24.5) rot=(0,1,0;1.5708rad)
FEATURE [Part::Feature] Part__Feature292  label="CUI_VGS-25W-087"
  shape: bbox 6 x 13.55 x 11.3 mm, 86 faces (baked)
FEATURE [Part::Feature] Part__Feature293  label="CUI_VGS-25W-088"
  shape: bbox 55.03 x 25.15 x 80 mm, 254 faces (baked)
FEATURE [Part::Feature] Part__Feature294  label="CUI_VGS-25W-089"
  shape: bbox 7.911 x 7.911 x 1.162 mm, 68 faces (baked)
FEATURE [Part::Feature] Part__Feature295  label="CUI_VGS-25W-090"
  shape: bbox 5.629 x 5.629 x 8.001 mm, 43 faces (baked)
FEATURE [Part::Feature] Part__Feature296  label="CUI_VGS-25W-091"
  shape: bbox 4.944 x 5.8 x 5.8 mm, 37 faces (baked)
FEATURE [Part::Feature] Part__Feature297  label="CUI_VGS-25W-092"
  shape: bbox 6 x 13.55 x 11.3 mm, 86 faces (baked)
FEATURE [Part::Feature] Part__Feature298  label="CUI_VGS-25W-093"
  shape: bbox 5.629 x 5.629 x 8.001 mm, 43 faces (baked)
FEATURE [Part::Feature] Part__Feature299  label="CUI_VGS-25W-094"
  shape: bbox 39.6 x 12 x 16 mm, 290 faces (baked)
FEATURE [Part::Feature] Part__Feature300  label="CUI_VGS-25W-095"
  shape: bbox 5.443 x 12.7 x 3.793 mm, 44 faces (baked)
FEATURE [Part::Feature] Part__Feature301  label="CUI_VGS-25W-096"
  shape: bbox 54.37 x 24.2 x 80.19 mm, 487 faces (baked)
FEATURE [Part::Feature] Part__Feature302  label="CUI_VGS-25W-097"
  shape: bbox 6 x 13.55 x 11.3 mm, 86 faces (baked)
FEATURE [Part::Feature] Part__Feature303  label="CUI_VGS-25W-098"
  shape: bbox 5.413 x 8.147 x 5.557 mm, 54 faces (baked)
FEATURE [Part::Feature] Part__Feature304  label="CUI_VGS-25W-099"
  shape: bbox 6 x 13.55 x 11.3 mm, 86 faces (baked)
FEATURE [Part::Feature] Part__Feature305  label="CUI_VGS-25W-100"
  shape: bbox 9.096 x 12.71 x 7.718 mm, 112 faces (baked)
FEATURE [Part::Feature] Part__Feature306  label="CUI_VGS-25W-101"
  shape: bbox 6 x 13.55 x 11.3 mm, 86 faces (baked)
FEATURE [Part::Feature] Part__Feature307  label="CUI_VGS-25W-102"
  shape: bbox 5.629 x 5.629 x 8.001 mm, 43 faces (baked)
FEATURE [Part::Feature] Part__Feature308  label="CUI_VGS-25W-103"
  shape: bbox 5.629 x 5.629 x 8.001 mm, 43 faces (baked)
FEATURE [Part::Feature] Part__Feature309  label="CUI_VGS-25W-104"
  shape: bbox 7.911 x 7.911 x 1.162 mm, 68 faces (baked)
FEATURE [Part::Feature] Part__Feature310  label="CUI_VGS-25W-105"
  shape: bbox 7.911 x 7.911 x 1.162 mm, 68 faces (baked)
FEATURE [Part::Feature] Part__Feature311  label="CUI_VGS-25W-106"
  shape: bbox 7 x 0.55 x 7 mm, 6 faces (baked)
FEATURE [Part::Feature] Part__Feature312  label="CUI_VGS-25W-107"
  shape: bbox 53.1 x 22.4 x 79.2 mm, 72 faces (baked)
FEATURE [Part::Feature] Part__Feature313  label="CUI_VGS-25W-108"
  shape: bbox 4.624 x 1.433 x 4.618 mm, 8 faces (baked)
FEATURE [Part::Feature] Part__Feature314  label="CUI_VGS-25W-109"
  shape: bbox 7.911 x 7.911 x 1.162 mm, 68 faces (baked)
FEATURE [Part::Feature] Part__Feature315  label="CUI_VGS-25W-110"
  shape: bbox 5.629 x 5.629 x 8.001 mm, 43 faces (baked)
FEATURE [Part::Feature] Part__Feature316  label="CUI_VGS-25W-111"
  shape: bbox 52.65 x 1.621 x 78.18 mm, 385 faces (baked)
FEATURE [Part::Feature] Part__Feature317  label="CUI_VGS-25W-112"
  shape: bbox 7.911 x 7.911 x 1.162 mm, 68 faces (baked)
FEATURE [App::Part] CUI_VGS_25W_008  label="CUI_VGS-25W-086"
  Group = -> [Part__Feature298,Part__Feature299,Part__Feature300,Part__Feature301,Part__Feature302,Part__Feature303,Part__Feature304,Part__Feature305,Part__Feature306,Part__Feature307,Part__Feature292,Part__Feature293,Part__Feature294,Part__Feature295,Part__Feature296,Part__Feature297,Part__Feature308,Part__Feature309,Part__Feature310,Part__Feature311,Part__Feature314,Part__Feature312,Part__Feature313,+3 more]
  Origin = -> Origin032
  Placement = pos=(22.5,-50.5,0.25) rot=(1,0,0;1.5708rad)
FEATURE [Sketcher::SketchObject] Sketch008
  ArcFitTolerance = 1e-06
  FullyConstrained = true
  MakeInternals = false
  Placement = pos=(0,0,0) rot=(1,0,0;1.5708rad)
  sketch-geometry (6):
    g0: LineSegment StartX=25 StartY=0 StartZ=0 EndX=25 EndY=-4 EndZ=0
    g1: LineSegment StartX=25 StartY=-4 StartZ=0 EndX=59.5 EndY=-4 EndZ=0
    g2: LineSegment StartX=59.5 StartY=-4 StartZ=0 EndX=59.5 EndY=21 EndZ=0
    g3: LineSegment StartX=59.5 StartY=21 StartZ=0 EndX=55.5 EndY=21 EndZ=0
    g4: LineSegment StartX=55.5 StartY=21 StartZ=0 EndX=55.5 EndY=0 EndZ=0
    g5: LineSegment StartX=55.5 StartY=0 StartZ=0 EndX=25 EndY=0 EndZ=0
  constraints (18):
    c: Coincident(g1,g0)
    c: Horizontal(g1)
    c: Vertical(g2)
    c: Coincident(g3,g2)
    c: Horizontal(g3)
    c: PointOnObject(g4,g-1)
    c: Vertical(g4)
    c: Coincident(g5,g4)
    c: Coincident(g5,g0)
    c: Horizontal(g5)
    c: Vertical(g0)
    c: Coincident(g1,g2)
    c: DistanceX(g0) = 25
    c: DistanceX(g5,g5) = 30.5
    c: DistanceX(g3,g3) = 4
    c: Coincident(g3,g4)
    c: DistanceY(g0,g0) = 4
    c: DistanceY(g2,g2) = 25
FEATURE [Part::Extrusion] Extrude008
  Base = -> Sketch008
  Dir = (0,-1,2e-16)
  DirMode = 2
  FaceMakerClass = Part::FaceMakerBullseye
  FaceMakerMode = 3
  LengthFwd = 20
  LengthRev = 0
  Solid = true
  Symmetric = false
FEATURE [Sketcher::SketchObject] Sketch009
  ArcFitTolerance = 1e-06
  FullyConstrained = true
  MakeInternals = false
  Placement = pos=(0,0,0) rot=(1,0,0;1.5708rad)
  sketch-geometry (6):
    g0: LineSegment StartX=73 StartY=21 StartZ=0 EndX=25 EndY=21 EndZ=0
    g1: LineSegment StartX=25 StartY=21 StartZ=0 EndX=25 EndY=-4 EndZ=0
    g2: LineSegment StartX=25 StartY=-4 StartZ=0 EndX=73 EndY=-4 EndZ=0
    g3: LineSegment StartX=73 StartY=-4 StartZ=0 EndX=73 EndY=21 EndZ=0
    g4: Circle CenterX=67 CenterY=15 CenterZ=0 NormalX=0 NormalY=0 NormalZ=1 AngleXU=0 Radius=1.625
    g5: Circle CenterX=67 CenterY=2 CenterZ=0 NormalX=0 NormalY=0 NormalZ=1 AngleXU=0 Radius=1.625
  constraints (18):
    c: Horizontal(g0)
    c: Vertical(g1)
    c: DistanceX(g0,g0) = 48
    c: DistanceX(g1) = 25
    c: Coincident(g2,g1)
    c: Coincident(g3,g2)
    c: Coincident(g3,g0)
    c: Vertical(g3)
    c: DistanceY(g1,g1) = 25
    c: Horizontal(g2)
    c: DistanceY(g1) = -4
    c: Coincident(g0,g1)
    c: Equal(g4,g5)
    c: Diameter(g4) = 3.25
    c: Vertical(g5,g4)
    c: DistanceY(g1,g5) = 6
    c: DistanceY(g5,g4) = 13
    c: DistanceX(g1,g5) = 42
FEATURE [Part::Extrusion] Extrude009
  Base = -> Sketch009
  Dir = (0,-1,2e-16)
  DirMode = 2
  FaceMakerClass = Part::FaceMakerBullseye
  FaceMakerMode = 3
  LengthFwd = 5
  LengthRev = 0
  Solid = true
  Symmetric = false
FEATURE [Part::MultiFuse] Fusion017
  Shapes = -> [Extrude009,Extrude008]
FEATURE [Sketcher::SketchObject] Sketch010
  ArcFitTolerance = 1e-06
  FullyConstrained = true
  MakeInternals = false
  sketch-geometry (1):
    g0: Circle CenterX=29.75 CenterY=-15.85 CenterZ=0 NormalX=0 NormalY=0 NormalZ=1 AngleXU=0 Radius=1.625
  constraints (3):
    c: DistanceX(g0) = 29.75
    c: DistanceY(g0) = -15.85
    c: Diameter(g0) = 3.25
FEATURE [Part::Extrusion] Extrude010
  Base = -> Sketch010
  Dir = (0,0,1)
  DirMode = 2
  FaceMakerClass = Part::FaceMakerBullseye
  FaceMakerMode = 3
  LengthFwd = 10
  LengthRev = 0
  Reversed = true
  Solid = true
  Symmetric = false
FEATURE [Sketcher::SketchObject] Sketch011
  ArcFitTolerance = 1e-06
  FullyConstrained = true
  MakeInternals = false
  Placement = pos=(0,0,0) rot=(0.57735,0.57735,0.57735;2.0944rad)
  sketch-geometry (1):
    g0: Circle CenterX=-8.1 CenterY=14.25 CenterZ=0 NormalX=0 NormalY=0 NormalZ=1 AngleXU=0 Radius=1.625
  constraints (3):
    c: DistanceX(g0) = -8.1
    c: DistanceY(g0) = 14.25
    c: Diameter(g0) = 3.25
FEATURE [Part::Extrusion] Extrude011
  Base = -> Sketch011
  Dir = (1,0,0)
  DirMode = 2
  FaceMakerClass = Part::FaceMakerBullseye
  FaceMakerMode = 3
  LengthFwd = 75
  LengthRev = 0
  Solid = true
  Symmetric = false
FEATURE [Part::MultiFuse] Fusion018  label="cuts001"
  Shapes = -> [Extrude010,Extrude011]
FEATURE [Part::Cut] Cut020
  Base = -> Fusion017
  Tool = -> Fusion018
FEATURE [Part::Fillet] Fillet017
  Base = -> Cut020
  EdgeLinks = -> Cut020 [Edge30,Edge33,Edge44,Edge46,Edge47,Edge48]
  Edges = 6 edges r=1: [Edge30,Edge33,Edge44,Edge46,Edge47,Edge48]
FEATURE [Part::Fillet] Fillet015
  Base = -> Fillet017
  EdgeLinks = -> Fillet017 [Edge41,Edge47,Edge48]
  Edges = 3 edges r=1: [Edge41,Edge47,Edge48]
FEATURE [Part::Fillet] Fillet016
  Base = -> Fillet015
  EdgeLinks = -> Fillet015 [Edge15,Edge38,Edge46,Edge47]
  Edges = 4 edges r=0.25: [Edge15,Edge38,Edge46,Edge47]
FEATURE [Part::Compound] Compound001  label="5vHolder001"
  Links = -> [CUI_VGS_25W_008,Fillet016]
  Placement = pos=(145.5,158,-99.25) rot=(0,1,0;1.5708rad)
FEATURE [Part::Feature] Part__Feature318  label="Heat Sink002"
  shape: bbox 100 x 91 x 19 mm, 161 faces (baked)
FEATURE [Part::Feature] Part__Feature319  label="Component011"
  Placement = pos=(-40,-40,21) rot=(0,1,0;3.14159rad)
  shape: bbox 83.92 x 84.69 x 8.441 mm, 27 faces (baked)
FEATURE [Part::Feature] Part__Feature320  label="80mmFanSlim003"
  shape: bbox 82.8 x 82.8 x 10.8 mm, 179 faces (baked)
FEATURE [App::Part] Part008  label="80mm_Fan002"
  Group = -> [Part__Feature319,Part__Feature320]
  Origin = -> Origin033
  Placement = pos=(0,0,0) rot=(1,0,0;3.14159rad)
FEATURE [Part::Feature] Part__Feature321  label="Battery Holder002"
  shape: bbox 28.5 x 16 x 6 mm, 91 faces (baked)
FEATURE [Part::Feature] Part__Feature322  label="DC Jack002"
  shape: bbox 7.6 x 11.5 x 9.75 mm, 10 faces (baked)
FEATURE [Part::Feature] Part__Feature323  label="PCB002"
  shape: bbox 90 x 90 x 3.3 mm, 59 faces (baked)
FEATURE [Part::Feature] Part__Feature324  label="HDMI002"
  shape: bbox 14.51 x 11.61 x 5.506 mm, 31 faces (baked)
FEATURE [Part::Feature] Part__Feature325  label="Ethernet002"
  shape: bbox 15.9 x 21.4 x 13.5 mm, 25 faces (baked)
FEATURE [Part::Feature] Part__Feature326  label="USB 3.0 B002"
  shape: bbox 14.55 x 17.5 x 16.15 mm, 36 faces (baked)
FEATURE [Part::Feature] Part__Feature327  label="USB 3.0 A002"
  shape: bbox 14.55 x 17.5 x 16.15 mm, 36 faces (baked)
FEATURE [Part::Feature] Part__Feature328  label="Audio Jack002"
  shape: bbox 6.5 x 14 x 4 mm, 10 faces (baked)
FEATURE [Part::Feature] Part__Feature329  label="Fan Plug002"
  shape: bbox 3.75 x 7.5 x 4.75 mm, 32 faces (baked)
FEATURE [Part::Feature] Part__Feature330  label="REMOCON002"
  shape: bbox 7.006 x 5.006 x 12.01 mm, 30 faces (baked)
FEATURE [Part::Feature] Part__Feature331  label="eMMC002"
  shape: bbox 13.5 x 18.5 x 2.8 mm, 33 faces (baked)
FEATURE [Part::Feature] Part__Feature332  label="MicroUSB002"
  shape: bbox 7.012 x 4.616 x 3.511 mm, 31 faces (baked)
FEATURE [Part::Feature] Part__Feature333  label="Switch002"
  shape: bbox 9 x 5.74 x 3.5 mm, 11 faces (baked)
FEATURE [Part::Feature] Part__Feature334  label="MicroSD Card Socket002"
  shape: bbox 11.5 x 5.5 x 3.5 mm, 11 faces (baked)
FEATURE [Part::Feature] Part__Feature335  label="7 Pin Header002"
  shape: bbox 17.5 x 2.5 x 8 mm, 41 faces (baked)
FEATURE [Part::Feature] Part__Feature336  label="UART002"
  shape: bbox 5 x 12.5 x 6 mm, 43 faces (baked)
FEATURE [Part::Feature] Part__Feature337  label="40 Pin Header002"
  shape: bbox 5 x 50 x 8 mm, 206 faces (baked)
FEATURE [App::Part] Odroid_N2__v006  label="Odroid-N2+ v006"
  Group = -> [Part__Feature318,Part__Feature321,Part__Feature322,Part__Feature323,Part__Feature324,Part__Feature325,Part__Feature326,Part__Feature327,Part__Feature328,Part__Feature329,Part__Feature330,Part__Feature331,Part__Feature332,Part__Feature333,Part__Feature334,Part__Feature335,Part__Feature336,Part__Feature337]
  Origin = -> Origin034
  Placement = pos=(-59,-819.5,-41.5) rot=(0,0,1;0rad)
FEATURE [App::Part] Part009  label="N2+002"
  Group = -> [Part008,Odroid_N2__v006]
  Origin = -> Origin035
  Placement = pos=(100,20,25) rot=(-1,0,0;0rad)
FEATURE [Sketcher::SketchObject] Sketch012
  ArcFitTolerance = 1e-06
  FullyConstrained = true
  MakeInternals = false
  sketch-geometry (22):
    g0: LineSegment StartX=18 StartY=115 StartZ=0 EndX=18 EndY=5 EndZ=0
    g1: LineSegment StartX=18 StartY=5 StartZ=0 EndX=102 EndY=5 EndZ=0
    g2: LineSegment StartX=102 StartY=5 StartZ=0 EndX=102 EndY=115 EndZ=0
    g3: LineSegment StartX=102 StartY=115 StartZ=0 EndX=18 EndY=115 EndZ=0
    g4: LineSegment StartX=30 StartY=105 StartZ=0 EndX=30 EndY=15 EndZ=0
    g5: LineSegment StartX=30 StartY=15 StartZ=0 EndX=90 EndY=15 EndZ=0
    g6: LineSegment StartX=90 StartY=15 StartZ=0 EndX=90 EndY=105 EndZ=0
    g7: LineSegment StartX=90 StartY=105 StartZ=0 EndX=30 EndY=105 EndZ=0
    g8: Circle CenterX=24.3 CenterY=95.75 CenterZ=0 NormalX=0 NormalY=0 NormalZ=1 AngleXU=0 Radius=1.625
    g9: Circle CenterX=95.8 CenterY=95.75 CenterZ=0 NormalX=0 NormalY=0 NormalZ=1 AngleXU=0 Radius=1.625
    g10: Circle CenterX=95.8 CenterY=24.25 CenterZ=0 NormalX=0 NormalY=0 NormalZ=1 AngleXU=0 Radius=1.625
    g11: Circle CenterX=24.3 CenterY=24.25 CenterZ=0 NormalX=0 NormalY=0 NormalZ=1 AngleXU=0 Radius=1.625
    g12: Circle CenterX=28 CenterY=10 CenterZ=0 NormalX=0 NormalY=0 NormalZ=1 AngleXU=0 Radius=1.625
    g13: Circle CenterX=43 CenterY=10 CenterZ=0 NormalX=0 NormalY=0 NormalZ=1 AngleXU=0 Radius=1.625
    g14: Circle CenterX=58 CenterY=10 CenterZ=0 NormalX=0 NormalY=0 NormalZ=1 AngleXU=0 Radius=1.625
    g15: Circle CenterX=73 CenterY=10 CenterZ=0 NormalX=0 NormalY=0 NormalZ=1 AngleXU=0 Radius=1.625
    g16: Circle CenterX=88 CenterY=10 CenterZ=0 NormalX=0 NormalY=0 NormalZ=1 AngleXU=0 Radius=1.625
    g17: Circle CenterX=28 CenterY=110 CenterZ=0 NormalX=0 NormalY=0 NormalZ=1 AngleXU=0 Radius=1.625
    g18: Circle CenterX=43 CenterY=110 CenterZ=0 NormalX=0 NormalY=0 NormalZ=1 AngleXU=0 Radius=1.625
    g19: Circle CenterX=58 CenterY=110 CenterZ=0 NormalX=0 NormalY=0 NormalZ=1 AngleXU=0 Radius=1.625
    g20: Circle CenterX=73 CenterY=110 CenterZ=0 NormalX=0 NormalY=0 NormalZ=1 AngleXU=0 Radius=1.625
    g21: Circle CenterX=88 CenterY=110 CenterZ=0 NormalX=0 NormalY=0 NormalZ=1 AngleXU=0 Radius=1.625
  constraints (59):
    c: Vertical(g0)
    c: Coincident(g1,g0)
    c: Horizontal(g1)
    c: Vertical(g2)
    c: Coincident(g3,g2)
    c: Coincident(g3,g0)
    c: Horizontal(g3)
    c: Coincident(g4,g5)
    c: Coincident(g5,g6)
    c: Coincident(g6,g7)
    c: Coincident(g7,g4)
    c: Vertical(g4)
    c: Vertical(g6)
    c: Horizontal(g5)
    c: Horizontal(g7)
    c: DistanceY(g0) = 5
    c: DistanceX(g0) = 18
    c: DistanceX(g0,g4) = 12
    c: DistanceX(g5,g5) = 60
    c: Coincident(g1,g2)
    c: DistanceX(g5,g1) = 12
    c: DistanceY(g0,g4) = 10
    c: DistanceY(g4,g4) = 90
    c: DistanceY(g4,g0) = 10
    c: Equal(g12, g13-g16) x4
    c: Equal(g12,g10)
    c: Equal(g12,g9)
    c: Equal(g12,g8)
    c: Equal(g12,g11)
    c: Equal(g12, g17-g21) x5
    c: Diameter(g12) = 3.25
    c: Horizontal(g12,g13)
    c: Horizontal(g13,g14)
    c: Horizontal(g14,g15)
    c: Horizontal(g15,g16)
    c: Horizontal(g17,g18)
    c: Horizontal(g18,g19)
    c: Horizontal(g19,g20)
    c: Horizontal(g20,g21)
    c: Horizontal(g8,g9)
    c: Horizontal(g11,g10)
    c: Vertical(g11,g8)
    c: DistanceX(g12,g13) = 15
    c: DistanceX(g13,g14) = 15
    c: Distance(g14,g15) = 15
    c: Distance(g15,g16) = 15
    c: DistanceX(g0,g12) = 10
    c: DistanceY(g0,g12) = 5
    c: DistanceY(g17,g0) = 5
    c: Vertical(g17,g12)
    c: Vertical(g18,g13)
    c: Vertical(g19,g14)
    c: Vertical(g15,g20)
    c: Vertical(g16,g21)
    c: Vertical(g10,g9)
    c: DistanceX(g11) = 24.3
    c: DistanceY(g11) = 24.25
    c: DistanceX(g11,g10) = 71.5
    c: DistanceY(g11,g8) = 71.5
FEATURE [Part::Extrusion] Extrude012
  Base = -> Sketch012
  Dir = (0,0,1)
  DirMode = 2
  FaceMakerClass = Part::FaceMakerBullseye
  FaceMakerMode = 3
  LengthFwd = 8
  LengthRev = 0
  Solid = true
  Symmetric = false
FEATURE [Part::Fillet] Fillet018
  Base = -> Extrude012
  EdgeLinks = -> Extrude012 [Edge1,Edge2,Edge4,Edge5,Edge7,Edge8,Edge10,Edge12,Edge16,Edge19,Edge22,Edge24]
  Edges = 12 edges r=3: [Edge1,Edge2,Edge4,Edge5,Edge7,Edge8,Edge10,Edge12,Edge16,Edge19,Edge22,Edge24]
FEATURE [Part::Fillet] Fillet019
  Base = -> Fillet018
  EdgeLinks = -> Fillet018 [Edge55,Edge57,Edge59,Edge61,Edge63,Edge65,Edge67,Edge69,Edge71,Edge73,Edge75,Edge77,Edge81]
  Edges = 13 edges r=0.25: [Edge55,Edge57,Edge59,Edge61,Edge63,Edge65,Edge67,Edge69,Edge71,Edge73,Edge75,Edge77,Edge81]
FEATURE [Sketcher::SketchObject] Sketch013
  ArcFitTolerance = 1e-06
  FullyConstrained = true
  MakeInternals = false
  sketch-geometry (4):
    g0: Circle CenterX=24.3 CenterY=95.75 CenterZ=0 NormalX=0 NormalY=0 NormalZ=1 AngleXU=0 Radius=3
    g1: Circle CenterX=95.8 CenterY=95.75 CenterZ=0 NormalX=0 NormalY=0 NormalZ=1 AngleXU=0 Radius=3
    g2: Circle CenterX=95.8 CenterY=24.25 CenterZ=0 NormalX=0 NormalY=0 NormalZ=1 AngleXU=0 Radius=3
    g3: Circle CenterX=24.3 CenterY=24.25 CenterZ=0 NormalX=0 NormalY=0 NormalZ=1 AngleXU=0 Radius=3
  constraints (12):
    c: Horizontal(g0,g1)
    c: Horizontal(g3,g2)
    c: Vertical(g3,g0)
    c: Vertical(g2,g1)
    c: DistanceX(g3) = 24.3
    c: DistanceY(g3) = 24.25
    c: DistanceX(g3,g2) = 71.5
    c: DistanceY(g3,g0) = 71.5
    c: Equal(g3,g2)
    c: Equal(g3,g1)
    c: Equal(g3,g0)
    c: Diameter(g3) = 6
FEATURE [Part::Extrusion] Extrude013
  Base = -> Sketch013
  Dir = (0,0,1)
  DirMode = 2
  FaceMakerClass = Part::FaceMakerBullseye
  FaceMakerMode = 3
  LengthFwd = 3.5
  LengthRev = 0
  Solid = true
  Symmetric = false
FEATURE [Part::Cut] Cut021  label="n2Holder"
  Base = -> Fillet019
  Tool = -> Extrude013
FEATURE [Part::Compound] Compound002  label="n2WithTheHolder"
  Links = -> [Part009,Cut021]
  Placement = pos=(-150,158,-40) rot=(1,0,0;1.5708rad)
FEATURE [Part::Feature] Part__Feature338  label="Heat Sink003"
  shape: bbox 100 x 91 x 19 mm, 161 faces (baked)
FEATURE [Part::Feature] Part__Feature339  label="Component012"
  Placement = pos=(-40,-40,21) rot=(0,1,0;3.14159rad)
  shape: bbox 83.92 x 84.69 x 8.441 mm, 27 faces (baked)
FEATURE [Part::Feature] Part__Feature340  label="80mmFanSlim004"
  shape: bbox 82.8 x 82.8 x 10.8 mm, 179 faces (baked)
FEATURE [App::Part] Part010  label="80mm_Fan003"
  Group = -> [Part__Feature339,Part__Feature340]
  Origin = -> Origin036
  Placement = pos=(0,0,0) rot=(1,0,0;3.14159rad)
FEATURE [Part::Feature] Part__Feature341  label="Battery Holder003"
  shape: bbox 28.5 x 16 x 6 mm, 91 faces (baked)
FEATURE [Part::Feature] Part__Feature342  label="DC Jack003"
  shape: bbox 7.6 x 11.5 x 9.75 mm, 10 faces (baked)
FEATURE [Part::Feature] Part__Feature343  label="PCB003"
  shape: bbox 90 x 90 x 3.3 mm, 59 faces (baked)
FEATURE [Part::Feature] Part__Feature344  label="HDMI003"
  shape: bbox 14.51 x 11.61 x 5.506 mm, 31 faces (baked)
FEATURE [Part::Feature] Part__Feature345  label="Ethernet003"
  shape: bbox 15.9 x 21.4 x 13.5 mm, 25 faces (baked)
FEATURE [Part::Feature] Part__Feature346  label="USB 3.0 B003"
  shape: bbox 14.55 x 17.5 x 16.15 mm, 36 faces (baked)
FEATURE [Part::Feature] Part__Feature347  label="USB 3.0 A003"
  shape: bbox 14.55 x 17.5 x 16.15 mm, 36 faces (baked)
FEATURE [Part::Feature] Part__Feature348  label="Audio Jack003"
  shape: bbox 6.5 x 14 x 4 mm, 10 faces (baked)
FEATURE [Part::Feature] Part__Feature349  label="Fan Plug003"
  shape: bbox 3.75 x 7.5 x 4.75 mm, 32 faces (baked)
FEATURE [Part::Feature] Part__Feature350  label="REMOCON003"
  shape: bbox 7.006 x 5.006 x 12.01 mm, 30 faces (baked)
FEATURE [Part::Feature] Part__Feature351  label="eMMC003"
  shape: bbox 13.5 x 18.5 x 2.8 mm, 33 faces (baked)
FEATURE [Part::Feature] Part__Feature352  label="MicroUSB003"
  shape: bbox 7.012 x 4.616 x 3.511 mm, 31 faces (baked)
FEATURE [Part::Feature] Part__Feature353  label="Switch003"
  shape: bbox 9 x 5.74 x 3.5 mm, 11 faces (baked)
FEATURE [Part::Feature] Part__Feature354  label="MicroSD Card Socket003"
  shape: bbox 11.5 x 5.5 x 3.5 mm, 11 faces (baked)
FEATURE [Part::Feature] Part__Feature355  label="7 Pin Header003"
  shape: bbox 17.5 x 2.5 x 8 mm, 41 faces (baked)
FEATURE [Part::Feature] Part__Feature356  label="UART003"
  shape: bbox 5 x 12.5 x 6 mm, 43 faces (baked)
FEATURE [Part::Feature] Part__Feature357  label="40 Pin Header003"
  shape: bbox 5 x 50 x 8 mm, 206 faces (baked)
FEATURE [App::Part] Odroid_N2__v007  label="Odroid-N2+ v007"
  Group = -> [Part__Feature338,Part__Feature341,Part__Feature342,Part__Feature343,Part__Feature344,Part__Feature345,Part__Feature346,Part__Feature347,Part__Feature348,Part__Feature349,Part__Feature350,Part__Feature351,Part__Feature352,Part__Feature353,Part__Feature354,Part__Feature355,Part__Feature356,Part__Feature357]
  Origin = -> Origin037
  Placement = pos=(-59,-819.5,-41.5) rot=(0,0,1;0rad)
FEATURE [App::Part] Part011  label="N2+003"
  Group = -> [Part010,Odroid_N2__v007]
  Origin = -> Origin038
  Placement = pos=(100,20,25) rot=(-1,0,0;0rad)
FEATURE [Sketcher::SketchObject] Sketch014
  ArcFitTolerance = 1e-06
  FullyConstrained = true
  MakeInternals = false
  sketch-geometry (22):
    g0: LineSegment StartX=18 StartY=115 StartZ=0 EndX=18 EndY=5 EndZ=0
    g1: LineSegment StartX=18 StartY=5 StartZ=0 EndX=102 EndY=5 EndZ=0
    g2: LineSegment StartX=102 StartY=5 StartZ=0 EndX=102 EndY=115 EndZ=0
    g3: LineSegment StartX=102 StartY=115 StartZ=0 EndX=18 EndY=115 EndZ=0
    g4: LineSegment StartX=30 StartY=105 StartZ=0 EndX=30 EndY=15 EndZ=0
    g5: LineSegment StartX=30 StartY=15 StartZ=0 EndX=90 EndY=15 EndZ=0
    g6: LineSegment StartX=90 StartY=15 StartZ=0 EndX=90 EndY=105 EndZ=0
    g7: LineSegment StartX=90 StartY=105 StartZ=0 EndX=30 EndY=105 EndZ=0
    g8: Circle CenterX=24.3 CenterY=95.75 CenterZ=0 NormalX=0 NormalY=0 NormalZ=1 AngleXU=0 Radius=1.625
    g9: Circle CenterX=95.8 CenterY=95.75 CenterZ=0 NormalX=0 NormalY=0 NormalZ=1 AngleXU=0 Radius=1.625
    g10: Circle CenterX=95.8 CenterY=24.25 CenterZ=0 NormalX=0 NormalY=0 NormalZ=1 AngleXU=0 Radius=1.625
    g11: Circle CenterX=24.3 CenterY=24.25 CenterZ=0 NormalX=0 NormalY=0 NormalZ=1 AngleXU=0 Radius=1.625
    g12: Circle CenterX=28 CenterY=10 CenterZ=0 NormalX=0 NormalY=0 NormalZ=1 AngleXU=0 Radius=1.625
    g13: Circle CenterX=43 CenterY=10 CenterZ=0 NormalX=0 NormalY=0 NormalZ=1 AngleXU=0 Radius=1.625
    g14: Circle CenterX=58 CenterY=10 CenterZ=0 NormalX=0 NormalY=0 NormalZ=1 AngleXU=0 Radius=1.625
    g15: Circle CenterX=73 CenterY=10 CenterZ=0 NormalX=0 NormalY=0 NormalZ=1 AngleXU=0 Radius=1.625
    g16: Circle CenterX=88 CenterY=10 CenterZ=0 NormalX=0 NormalY=0 NormalZ=1 AngleXU=0 Radius=1.625
    g17: Circle CenterX=28 CenterY=110 CenterZ=0 NormalX=0 NormalY=0 NormalZ=1 AngleXU=0 Radius=1.625
    g18: Circle CenterX=43 CenterY=110 CenterZ=0 NormalX=0 NormalY=0 NormalZ=1 AngleXU=0 Radius=1.625
    g19: Circle CenterX=58 CenterY=110 CenterZ=0 NormalX=0 NormalY=0 NormalZ=1 AngleXU=0 Radius=1.625
    g20: Circle CenterX=73 CenterY=110 CenterZ=0 NormalX=0 NormalY=0 NormalZ=1 AngleXU=0 Radius=1.625
    g21: Circle CenterX=88 CenterY=110 CenterZ=0 NormalX=0 NormalY=0 NormalZ=1 AngleXU=0 Radius=1.625
  constraints (59):
    c: Vertical(g0)
    c: Coincident(g1,g0)
    c: Horizontal(g1)
    c: Vertical(g2)
    c: Coincident(g3,g2)
    c: Coincident(g3,g0)
    c: Horizontal(g3)
    c: Coincident(g4,g5)
    c: Coincident(g5,g6)
    c: Coincident(g6,g7)
    c: Coincident(g7,g4)
    c: Vertical(g4)
    c: Vertical(g6)
    c: Horizontal(g5)
    c: Horizontal(g7)
    c: DistanceY(g0) = 5
    c: DistanceX(g0) = 18
    c: DistanceX(g0,g4) = 12
    c: DistanceX(g5,g5) = 60
    c: Coincident(g1,g2)
    c: DistanceX(g5,g1) = 12
    c: DistanceY(g0,g4) = 10
    c: DistanceY(g4,g4) = 90
    c: DistanceY(g4,g0) = 10
    c: Equal(g12, g13-g16) x4
    c: Equal(g12,g10)
    c: Equal(g12,g9)
    c: Equal(g12,g8)
    c: Equal(g12,g11)
    c: Equal(g12, g17-g21) x5
    c: Diameter(g12) = 3.25
    c: Horizontal(g12,g13)
    c: Horizontal(g13,g14)
    c: Horizontal(g14,g15)
    c: Horizontal(g15,g16)
    c: Horizontal(g17,g18)
    c: Horizontal(g18,g19)
    c: Horizontal(g19,g20)
    c: Horizontal(g20,g21)
    c: Horizontal(g8,g9)
    c: Horizontal(g11,g10)
    c: Vertical(g11,g8)
    c: DistanceX(g12,g13) = 15
    c: DistanceX(g13,g14) = 15
    c: Distance(g14,g15) = 15
    c: Distance(g15,g16) = 15
    c: DistanceX(g0,g12) = 10
    c: DistanceY(g0,g12) = 5
    c: DistanceY(g17,g0) = 5
    c: Vertical(g17,g12)
    c: Vertical(g18,g13)
    c: Vertical(g19,g14)
    c: Vertical(g15,g20)
    c: Vertical(g16,g21)
    c: Vertical(g10,g9)
    c: DistanceX(g11) = 24.3
    c: DistanceY(g11) = 24.25
    c: DistanceX(g11,g10) = 71.5
    c: DistanceY(g11,g8) = 71.5
FEATURE [Part::Extrusion] Extrude014
  Base = -> Sketch014
  Dir = (0,0,1)
  DirMode = 2
  FaceMakerClass = Part::FaceMakerBullseye
  FaceMakerMode = 3
  LengthFwd = 8
  LengthRev = 0
  Solid = true
  Symmetric = false
FEATURE [Part::Fillet] Fillet020
  Base = -> Extrude014
  EdgeLinks = -> Extrude014 [Edge1,Edge2,Edge4,Edge5,Edge7,Edge8,Edge10,Edge12,Edge16,Edge19,Edge22,Edge24]
  Edges = 12 edges r=3: [Edge1,Edge2,Edge4,Edge5,Edge7,Edge8,Edge10,Edge12,Edge16,Edge19,Edge22,Edge24]
FEATURE [Part::Fillet] Fillet021
  Base = -> Fillet020
  EdgeLinks = -> Fillet020 [Edge55,Edge57,Edge59,Edge61,Edge63,Edge65,Edge67,Edge69,Edge71,Edge73,Edge75,Edge77,Edge81]
  Edges = 13 edges r=0.25: [Edge55,Edge57,Edge59,Edge61,Edge63,Edge65,Edge67,Edge69,Edge71,Edge73,Edge75,Edge77,Edge81]
FEATURE [Sketcher::SketchObject] Sketch015
  ArcFitTolerance = 1e-06
  FullyConstrained = true
  MakeInternals = false
  sketch-geometry (4):
    g0: Circle CenterX=24.3 CenterY=95.75 CenterZ=0 NormalX=0 NormalY=0 NormalZ=1 AngleXU=0 Radius=3
    g1: Circle CenterX=95.8 CenterY=95.75 CenterZ=0 NormalX=0 NormalY=0 NormalZ=1 AngleXU=0 Radius=3
    g2: Circle CenterX=95.8 CenterY=24.25 CenterZ=0 NormalX=0 NormalY=0 NormalZ=1 AngleXU=0 Radius=3
    g3: Circle CenterX=24.3 CenterY=24.25 CenterZ=0 NormalX=0 NormalY=0 NormalZ=1 AngleXU=0 Radius=3
  constraints (12):
    c: Horizontal(g0,g1)
    c: Horizontal(g3,g2)
    c: Vertical(g3,g0)
    c: Vertical(g2,g1)
    c: DistanceX(g3) = 24.3
    c: DistanceY(g3) = 24.25
    c: DistanceX(g3,g2) = 71.5
    c: DistanceY(g3,g0) = 71.5
    c: Equal(g3,g2)
    c: Equal(g3,g1)
    c: Equal(g3,g0)
    c: Diameter(g3) = 6
FEATURE [Part::Extrusion] Extrude015
  Base = -> Sketch015
  Dir = (0,0,1)
  DirMode = 2
  FaceMakerClass = Part::FaceMakerBullseye
  FaceMakerMode = 3
  LengthFwd = 3.5
  LengthRev = 0
  Solid = true
  Symmetric = false
FEATURE [Part::Cut] Cut022  label="n2Holder001"
  Base = -> Fillet021
  Tool = -> Extrude015
FEATURE [Part::Compound] Compound003  label="n2WithTheHolder001"
  Links = -> [Part011,Cut022]
  Placement = pos=(-45,158,-40) rot=(1,0,0;1.5708rad)
FEATURE [Part::Box] Box034  label="Main_box"
  AttacherType = Attacher::AttachEngine3D
  Height = 28
  Length = 89
  Width = 118
FEATURE [Part::Box] Box035  label="Cube019"
  AttacherType = Attacher::AttachEngine3D
  Height = 13.25
  Length = 17
  Placement = pos=(72,14.25,7) rot=(0,0,1;0rad)
  Width = 65
FEATURE [Part::Box] Box002  label="Cube020"
  AttacherType = Attacher::AttachEngine3D
  Height = 13.25
  Length = 17
  Placement = pos=(72,88.5,7) rot=(0,0,1;0rad)
  Width = 16.5
FEATURE [Part::Box] Box036  label="Power"
  AttacherType = Attacher::AttachEngine3D
  Height = 11
  Length = 30
  Placement = pos=(32,-9,11.75) rot=(0,0,1;0rad)
  Width = 9
FEATURE [Part::Box] Box037  label="mount1"
  AttacherType = Attacher::AttachEngine3D
  Height = 23.2
  Length = 1
  Placement = pos=(89,-15.5,2.25) rot=(0,0,1;0rad)
  Width = 25.5
FEATURE [Part::Box] Box038  label="mount2"
  AttacherType = Attacher::AttachEngine3D
  Height = 23.2
  Length = 1
  Placement = pos=(89,108,2.25) rot=(0,0,1;0rad)
  Width = 25.5
FEATURE [Part::Cut] Cut023  label="LAN_4_Cut"
  Base = -> Box034
  Tool = -> Box035
FEATURE [Part::Cut] Cut024  label="LAN_5_cut"
  Base = -> Cut023
  Tool = -> Box002
FEATURE [Part::Cylinder] Cylinder027
  Angle = 360
  AttacherType = Attacher::AttachEngine3D
  FirstAngle = 0
  Height = 10
  Placement = pos=(93,-3,4.5) rot=(0,1,0;4.71239rad)
  Radius = 3
  SecondAngle = 0
FEATURE [Part::Cylinder] Cylinder028
  Angle = 360
  AttacherType = Attacher::AttachEngine3D
  FirstAngle = 0
  Height = 10
  Placement = pos=(93,121,4.5) rot=(0,-1,0;1.5708rad)
  Radius = 3
  SecondAngle = 0
FEATURE [Part::Cylinder] Cylinder029
  Angle = 360
  AttacherType = Attacher::AttachEngine3D
  FirstAngle = 0
  Height = 10
  Placement = pos=(85,-9.5,6.25) rot=(0,1,0;1.5708rad)
  Radius = 1.5
  SecondAngle = 0
FEATURE [Part::Cylinder] Cylinder030
  Angle = 360
  AttacherType = Attacher::AttachEngine3D
  FirstAngle = 0
  Height = 10
  Placement = pos=(85,-9.5,20.25) rot=(0,1,0;1.5708rad)
  Radius = 1.5
  SecondAngle = 0
FEATURE [Part::Cylinder] Cylinder031
  Angle = 360
  AttacherType = Attacher::AttachEngine3D
  FirstAngle = 0
  Height = 10
  Placement = pos=(85,127.5,6.25) rot=(0,1,0;1.5708rad)
  Radius = 1.5
  SecondAngle = 0
FEATURE [Part::Cylinder] Cylinder032
  Angle = 360
  AttacherType = Attacher::AttachEngine3D
  FirstAngle = 0
  Height = 10
  Placement = pos=(85,127.5,20.25) rot=(0,1,0;1.5708rad)
  Radius = 1.5
  SecondAngle = 0
FEATURE [Part::MultiFuse] Fusion019  label="LAN_Power_Fused"
  Shapes = -> [Cut024,Box036,Box037,Box038]
FEATURE [Part::MultiFuse] Fusion020  label="mount_cyl"
  Placement = pos=(0,0,9.25) rot=(0,0,1;0rad)
  Shapes = -> [Cylinder027,Cylinder028]
FEATURE [Part::Cut] Cut025  label="Main_box001"
  Base = -> Fusion019
  Tool = -> Fusion020
FEATURE [Part::MultiFuse] Fusion021  label="mount_small_cyl"
  Refine = true
  Shapes = -> [Cylinder029,Cylinder030,Cylinder031,Cylinder032]
FEATURE [Part::Cut] Cut026  label="main_box001"
  Base = -> Cut025
  Refine = true
  Tool = -> Fusion021
FEATURE [Part::Fillet] Fillet022  label="Switch"
  Base = -> Cut026
  EdgeLinks = -> Cut026 [Edge10,Edge14,Edge21,Edge22,Edge23,Edge27,Edge41]
  Edges = 7 edges r=2: [Edge10,Edge14,Edge21,Edge22,Edge23,Edge27,Edge41]
  Placement = pos=(-144.75,67.25,81) rot=(0.57735,0.57735,-0.57735;4.18879rad)
FEATURE [Part::Box] Box039  label="Cube021"
  AttacherType = Attacher::AttachEngine3D
  Height = 2
  Length = 3
  Placement = pos=(-1.5,29,19.5) rot=(0,0,1;0rad)
  Width = 2
FEATURE [Part::Box] Box040  label="Cube022"
  AttacherType = Attacher::AttachEngine3D
  Height = 2
  Length = 3
  Placement = pos=(-1.5,29,19.5) rot=(0,0,1;0rad)
  Width = 2
FEATURE [Part::Box] Box041  label="Cube023"
  AttacherType = Attacher::AttachEngine3D
  Height = 5
  Length = 12
  Placement = pos=(15,12,-20) rot=(0,0,1;0rad)
  Width = 10
FEATURE [Part::Box] Box042  label="Cube024"
  AttacherType = Attacher::AttachEngine3D
  Height = 5
  Length = 12
  Placement = pos=(15,12,-20) rot=(0,0,1;0rad)
  Width = 10
FEATURE [Part::Box] Box043  label="Cube025"
  AttacherType = Attacher::AttachEngine3D
  Height = 13
  Length = 24
  Placement = pos=(-12,-2,12) rot=(0,0,1;0rad)
  Width = 42
FEATURE [Part::Box] Box044  label="Cube005"
  AttacherType = Attacher::AttachEngine3D
  Height = 13
  Length = 24
  Placement = pos=(-12,-2,12) rot=(0,0,1;0rad)
  Width = 42
FEATURE [Part::Cylinder] Cylinder033
  Angle = 360
  AttacherType = Attacher::AttachEngine3D
  FirstAngle = 0
  Height = 27
  Placement = pos=(0,-2,0) rot=(-1,0,0;1.5708rad)
  Radius = 5.9
  SecondAngle = 0
FEATURE [Part::Cylinder] Cylinder034
  Angle = 360
  AttacherType = Attacher::AttachEngine3D
  FirstAngle = 0
  Height = 5
  Placement = pos=(0,13,-15) rot=(0,0,1;0rad)
  Radius = 6.5
  SecondAngle = 0
FEATURE [Part::Cylinder] Cylinder035
  Angle = 360
  AttacherType = Attacher::AttachEngine3D
  FirstAngle = 0
  Height = 10
  Placement = pos=(10.87,21,-16.5) rot=(1,0,0;4.71239rad)
  Radius = 1.25
  SecondAngle = 0
FEATURE [Part::Cylinder] Cylinder036
  Angle = 360
  AttacherType = Attacher::AttachEngine3D
  FirstAngle = 0
  Height = 10
  Placement = pos=(-10.87,21,-16.5) rot=(-1,0,0;1.5708rad)
  Radius = 1.25
  SecondAngle = 0
FEATURE [Part::Cylinder] Cylinder037
  Angle = 360
  AttacherType = Attacher::AttachEngine3D
  FirstAngle = 0
  Height = 10
  Placement = pos=(22,17,-22) rot=(0,0,1;0rad)
  Radius = 1.6
  SecondAngle = 0
FEATURE [Part::Cut] Cut029
  Base = -> Box041
  Refine = true
  Tool = -> Cylinder037
FEATURE [Part::Cylinder] Cylinder038
  Angle = 360
  AttacherType = Attacher::AttachEngine3D
  FirstAngle = 0
  Height = 10
  Placement = pos=(22,17,-22) rot=(0,0,1;0rad)
  Radius = 1.6
  SecondAngle = 0
FEATURE [Part::Cut] Cut030
  Base = -> Box042
  Placement = pos=(0,34,0) rot=(0,0,1;3.14159rad)
  Refine = true
  Tool = -> Cylinder038
FEATURE [Part::MultiFuse] Fusion024  label="m2_cyl"
  Shapes = -> [Cylinder035,Cylinder036]
FEATURE [Part::Feature] Part__Feature358  label="SMA_f"
  Placement = pos=(0,33.5,0) rot=(1,0,0;4.71239rad)
  shape: bbox 7.333 x 19.05 x 7.333 mm, 216 faces (baked)
FEATURE [Part::Feature] Part__Feature359  label="SMA_m"
  Placement = pos=(0,-9,-2.2e-15) rot=(1,0,0;1.5708rad)
  shape: bbox 8.901 x 11.09 x 8.901 mm, 66 faces (baked)
FEATURE [Part::Feature] Part__Feature360  label="M3.5"
  Placement = pos=(0,7,9) rot=(0,0,1;0rad)
  shape: bbox 7.514 x 7.514 x 8.144 mm, 85 faces (baked)
FEATURE [Sketcher::SketchObject] Sketch019
  ArcFitTolerance = 0
  FullyConstrained = true
  MakeInternals = false
  Placement = pos=(0,0,0) rot=(1,0,0;1.5708rad)
  sketch-geometry (4):
    g0: LineSegment StartX=-5.75 StartY=-10 StartZ=0 EndX=5.75 EndY=-10 EndZ=0
    g1: LineSegment StartX=-5.75 StartY=10 StartZ=0 EndX=5.75 EndY=10 EndZ=0
    g2: ArcOfCircle CenterX=0 CenterY=-1e-16 CenterZ=0 NormalX=0 NormalY=0 NormalZ=1 AngleXU=0 Radius=11.5353 StartAngle=2.09263 EndAngle=4.19055
    g3: ArcOfCircle CenterX=0 CenterY=-1.2e-15 CenterZ=0 NormalX=0 NormalY=0 NormalZ=1 AngleXU=0 Radius=11.5353 StartAngle=5.23422 EndAngle=7.33215
  constraints (12):
    c: Symmetric(g1,g1,g-2)
    c: Symmetric(g0,g0,g-2)
    c: Distance(g1) = 11.5
    c: Distance(g0) = 11.5
    c: Distance(g1,g0) = 20
    c: Distance(g1,g-1) = 10
    c: Coincident(g2,g1)
    c: Coincident(g2,g0)
    c: Coincident(g3,g1)
    c: Coincident(g3,g0)
    c: PointOnObject(g2,g-2)
    c: PointOnObject(g3,g-2)
FEATURE [Part::Extrusion] Extrude019
  Base = -> Sketch019
  Dir = (0,-1,2e-16)
  DirMode = 2
  FaceMakerClass = Part::FaceMakerBullseye
  FaceMakerMode = 3
  LengthFwd = 23
  LengthRev = 0
  Reversed = true
  Solid = true
  Symmetric = false
FEATURE [Sketcher::SketchObject] Sketch020
  ArcFitTolerance = 0
  FullyConstrained = true
  MakeInternals = false
  Placement = pos=(0,0,0) rot=(1,0,0;1.5708rad)
  sketch-geometry (16):
    g0: LineSegment StartX=-7.5 StartY=-10 StartZ=0 EndX=-7.5 EndY=-16 EndZ=0
    g1: LineSegment StartX=-7.5 StartY=-16 StartZ=0 EndX=7.5 EndY=-16 EndZ=0
    g2: LineSegment StartX=7.5 StartY=-16 StartZ=0 EndX=7.5 EndY=-10 EndZ=0
    g3: ArcOfCircle CenterX=-2e-16 CenterY=11.88 CenterZ=0 NormalX=0 NormalY=0 NormalZ=1 AngleXU=0 Radius=6.64493 StartAngle=6.14733 EndAngle=9.56064
    g4: ArcOfCircle CenterX=0.265981 CenterY=0.194065 CenterZ=0 NormalX=0 NormalY=0 NormalZ=1 AngleXU=0 Radius=12.5 StartAngle=5.32955 EndAngle=7.32412
    g5: ArcOfCircle CenterX=-0.265981 CenterY=0.194065 CenterZ=0 NormalX=0 NormalY=0 NormalZ=1 AngleXU=0 Radius=12.5 StartAngle=2.10066 EndAngle=4.09523
    g6: ArcOfCircle CenterX=-1e-16 CenterY=12.4177 CenterZ=0 NormalX=0 NormalY=0 NormalZ=1 AngleXU=0 Radius=10.1 StartAngle=6.14235 EndAngle=9.56561
    g7: ArcOfCircle CenterX=-2.59139 CenterY=0.317652 CenterZ=0 NormalX=0 NormalY=0 NormalZ=1 AngleXU=0 Radius=13 StartAngle=2.17717 EndAngle=4.0584
    g8: ArcOfCircle CenterX=2.59139 CenterY=0.317652 CenterZ=0 NormalX=0 NormalY=0 NormalZ=1 AngleXU=0 Radius=13 StartAngle=5.36637 EndAngle=7.24761
    g9: LineSegment StartX=10.5 StartY=-10 StartZ=0 EndX=10.5 EndY=-13 EndZ=0
    g10: LineSegment StartX=10.5 StartY=-13 StartZ=0 EndX=15 EndY=-13 EndZ=0
    g11: LineSegment StartX=15 StartY=-13 StartZ=0 EndX=15 EndY=-20 EndZ=0
    g12: LineSegment StartX=-10.5 StartY=-10 StartZ=0 EndX=-10.5 EndY=-13 EndZ=0
    g13: LineSegment StartX=-10.5 StartY=-13 StartZ=0 EndX=-15 EndY=-13 EndZ=0
    g14: LineSegment StartX=-15 StartY=-13 StartZ=0 EndX=-15 EndY=-20 EndZ=0
    g15: LineSegment StartX=-15 StartY=-20 StartZ=0 EndX=15 EndY=-20 EndZ=0
  constraints (51):
    c: Vertical(g0)
    c: Coincident(g1,g0)
    c: Coincident(g2,g1)
    c: Vertical(g2)
    c: Coincident(g4,g3)
    c: Coincident(g4,g2)
    c: Coincident(g5,g3)
    c: Coincident(g5,g0)
    c: Distance(g0,g-1) = 16
    c: Distance(g0,g-2) = 7.5
    c: Symmetric(g0,g1,g-2)
    c: Distance(g0) = 6
    c: Distance(g2) = 6
    c: Diameter(g4) = 25
    c: Diameter(g5) = 25
    c: Symmetric(g3,g3,g-2)
    c: Distance(g3,g0) = 21
    c: Distance(g3,g-1) = 10.98
    c: Distance(g3,g-1) = 11.88
    c: Coincident(g7,g6)
    c: Coincident(g8,g6)
    c: Coincident(g9,g8)
    c: Vertical(g9)
    c: Coincident(g10,g9)
    c: Horizontal(g10)
    c: Coincident(g11,g10)
    c: Vertical(g11)
    c: Coincident(g12,g7)
    c: Vertical(g12)
    c: Coincident(g13,g12)
    c: Horizontal(g13)
    c: Coincident(g14,g13)
    c: Vertical(g14)
    c: Coincident(g15,g14)
    c: Coincident(g15,g11)
    c: Symmetric(g14,g11,g-2)
    c: Distance(g14,g-1) = 20
    c: Distance(g14) = 7
    c: Distance(g11) = 7
    c: Distance(g15) = 30
    c: Distance(g12,g0) = 3
    c: Distance(g9,g2) = 3
    c: Distance(g6,g-1) = 11
    c: Distance(g6,g-2) = 10
    c: Distance(g6,g-1) = 11
    c: Distance(g6,g-2) = 10
    c: Distance(g12) = 3
    c: Distance(g9) = 3
    c: Diameter(g8) = 26
    c: Diameter(g7) = 26
    c: Diameter(g6) = 20.2
FEATURE [Part::Extrusion] Extrude020  label="outer_case"
  Base = -> Sketch020
  Dir = (0,-1,2e-16)
  DirMode = 2
  FaceMakerClass = Part::FaceMakerBullseye
  FaceMakerMode = 3
  LengthFwd = 28
  LengthRev = 0
  Placement = pos=(0,3,0) rot=(0,0,1;0rad)
  Reversed = true
  Solid = true
  Symmetric = false
FEATURE [Part::Cut] Cut027  label="Outer_Case"
  Base = -> Extrude020
  Tool = -> Fusion024
FEATURE [Part::Cut] Cut028  label="Outer"
  Base = -> Cut027
  Tool = -> Box040
FEATURE [Sketcher::SketchObject] Sketch021
  ArcFitTolerance = 0
  FullyConstrained = true
  MakeInternals = false
  Placement = pos=(0,0,0) rot=(1,0,0;1.5708rad)
  sketch-geometry (11):
    g0: ArcOfCircle CenterX=-1e-16 CenterY=12.4177 CenterZ=0 NormalX=0 NormalY=0 NormalZ=1 AngleXU=0 Radius=10.1 StartAngle=6.14235 EndAngle=9.56561
    g1: ArcOfCircle CenterX=-2.59139 CenterY=0.317652 CenterZ=0 NormalX=0 NormalY=0 NormalZ=1 AngleXU=0 Radius=13 StartAngle=2.17717 EndAngle=4.0584
    g2: ArcOfCircle CenterX=2.59139 CenterY=0.317652 CenterZ=0 NormalX=0 NormalY=0 NormalZ=1 AngleXU=0 Radius=13 StartAngle=5.36637 EndAngle=7.24761
    g3: LineSegment StartX=10.5 StartY=-10 StartZ=0 EndX=10.5 EndY=-13 EndZ=0
    g4: LineSegment StartX=10.5 StartY=-13 StartZ=0 EndX=15 EndY=-13 EndZ=0
    g5: LineSegment StartX=15 StartY=-13 StartZ=0 EndX=15 EndY=-20 EndZ=0
    g6: LineSegment StartX=-10.5 StartY=-10 StartZ=0 EndX=-10.5 EndY=-13 EndZ=0
    g7: LineSegment StartX=-10.5 StartY=-13 StartZ=0 EndX=-15 EndY=-13 EndZ=0
    g8: LineSegment StartX=-15 StartY=-13 StartZ=0 EndX=-15 EndY=-20 EndZ=0
    g9: LineSegment StartX=-15 StartY=-20 StartZ=0 EndX=15 EndY=-20 EndZ=0
    g10: Circle CenterX=0 CenterY=0 CenterZ=0 NormalX=0 NormalY=0 NormalZ=1 AngleXU=0 Radius=5
  constraints (34):
    c: Coincident(g1,g0)
    c: Coincident(g2,g0)
    c: Coincident(g3,g2)
    c: Vertical(g3)
    c: Coincident(g4,g3)
    c: Horizontal(g4)
    c: Coincident(g5,g4)
    c: Vertical(g5)
    c: Coincident(g6,g1)
    c: Vertical(g6)
    c: Coincident(g7,g6)
    c: Horizontal(g7)
    c: Coincident(g8,g7)
    c: Vertical(g8)
    c: Coincident(g9,g8)
    c: Coincident(g9,g5)
    c: Symmetric(g8,g5,g-2)
    c: Distance(g8,g-1) = 20
    c: Distance(g8) = 7
    c: Distance(g5) = 7
    c: Distance(g9) = 30
    c: Distance(g0,g-1) = 11
    c: Distance(g0,g-2) = 10
    c: Distance(g0,g-1) = 11
    c: Distance(g0,g-2) = 10
    c: Distance(g6) = 3
    c: Distance(g3) = 3
    c: Diameter(g2) = 26
    c: Diameter(g1) = 26
    c: Diameter(g0) = 20.2
    c: Distance(g4) = 4.5
    c: Distance(g7) = 4.5
    c: Coincident(g-1,g10)
    c: Diameter(g10) = 10
FEATURE [Part::Extrusion] Extrude021  label="Front_cover"
  Base = -> Sketch021
  Dir = (0,-1,2e-16)
  DirMode = 2
  FaceMakerClass = Part::FaceMakerBullseye
  FaceMakerMode = 3
  LengthFwd = 3
  LengthRev = 0
  Reversed = true
  Solid = true
  Symmetric = false
FEATURE [Part::MultiFuse] Fusion026
  Refine = true
  Shapes = -> [Cut028,Extrude021,Cut030,Cut029]
FEATURE [Part::Cut] Cut031  label="OuterBox"
  Base = -> Fusion026
  Refine = true
  Tool = -> Box043
FEATURE [Sketcher::SketchObject] Sketch022
  ArcFitTolerance = 0
  FullyConstrained = true
  MakeInternals = false
  Placement = pos=(0,0,0) rot=(1,0,0;1.5708rad)
  sketch-geometry (14):
    g0: ArcOfCircle CenterX=0 CenterY=12.4177 CenterZ=0 NormalX=0 NormalY=0 NormalZ=1 AngleXU=0 Radius=10.1 StartAngle=6.14235 EndAngle=9.56561
    g1: ArcOfCircle CenterX=-2.59139 CenterY=0.317652 CenterZ=0 NormalX=0 NormalY=0 NormalZ=1 AngleXU=0 Radius=13 StartAngle=2.17717 EndAngle=4.0584
    g2: ArcOfCircle CenterX=2.59139 CenterY=0.317652 CenterZ=0 NormalX=0 NormalY=0 NormalZ=1 AngleXU=0 Radius=13 StartAngle=5.36637 EndAngle=7.24761
    g3: LineSegment StartX=10.5 StartY=-10 StartZ=0 EndX=10.5 EndY=-13 EndZ=0
    g4: LineSegment StartX=10.5 StartY=-13 StartZ=0 EndX=15 EndY=-13 EndZ=0
    g5: LineSegment StartX=15 StartY=-13 StartZ=0 EndX=15 EndY=-20 EndZ=0
    g6: LineSegment StartX=-10.5 StartY=-10 StartZ=0 EndX=-10.5 EndY=-13 EndZ=0
    g7: LineSegment StartX=-10.5 StartY=-13 StartZ=0 EndX=-15 EndY=-13 EndZ=0
    g8: LineSegment StartX=-15 StartY=-13 StartZ=0 EndX=-15 EndY=-20 EndZ=0
    g9: LineSegment StartX=-15 StartY=-20 StartZ=0 EndX=15 EndY=-20 EndZ=0
    g10: Circle CenterX=0 CenterY=0 CenterZ=0 NormalX=0 NormalY=0 NormalZ=1 AngleXU=0 Radius=5
    g11: Circle CenterX=0 CenterY=12.4177 CenterZ=0 NormalX=0 NormalY=0 NormalZ=1 AngleXU=0 Radius=4.5
    g12: Circle CenterX=-10.8747 CenterY=-16.5 CenterZ=0 NormalX=0 NormalY=0 NormalZ=1 AngleXU=0 Radius=1.25
    g13: Circle CenterX=10.8747 CenterY=-16.5 CenterZ=0 NormalX=0 NormalY=0 NormalZ=1 AngleXU=0 Radius=1.25
  constraints (41):
    c: Coincident(g1,g0)
    c: Coincident(g2,g0)
    c: Coincident(g3,g2)
    c: Vertical(g3)
    c: Coincident(g4,g3)
    c: Horizontal(g4)
    c: Coincident(g5,g4)
    c: Vertical(g5)
    c: Coincident(g6,g1)
    c: Vertical(g6)
    c: Coincident(g7,g6)
    c: Horizontal(g7)
    c: Coincident(g8,g7)
    c: Vertical(g8)
    c: Coincident(g9,g8)
    c: Coincident(g9,g5)
    c: Symmetric(g8,g5,g-2)
    c: Distance(g8,g-1) = 20
    c: Distance(g8) = 7
    c: Distance(g5) = 7
    c: Distance(g9) = 30
    c: Distance(g0,g-1) = 11
    c: Distance(g0,g-2) = 10
    c: Distance(g0,g-1) = 11
    c: Distance(g0,g-2) = 10
    c: Distance(g6) = 3
    c: Distance(g3) = 3
    c: Diameter(g2) = 26
    c: Diameter(g1) = 26
    c: Diameter(g0) = 20.2
    c: Distance(g4) = 4.5
    c: Distance(g7) = 4.5
    c: Coincident(g-1,g10)
    c: Diameter(g10) = 10
    c: Coincident(g11,g0)
    c: Diameter(g11) = 9
    c: Distance(g12,g-1) = 16.5
    c: Diameter(g13) = 2.5
    c: Diameter(g12) = 2.5
    c: Symmetric(g12,g13,g-2)
    c: Distance(g13,g3) = 3.52
FEATURE [Part::Extrusion] Extrude022  label="Back_cover"
  Base = -> Sketch022
  Dir = (0,-1,2e-16)
  DirMode = 2
  FaceMakerClass = Part::FaceMakerBullseye
  FaceMakerMode = 3
  LengthFwd = 3
  LengthRev = 0
  Placement = pos=(0,31,0) rot=(0,0,1;0rad)
  Reversed = true
  Solid = true
  Symmetric = false
FEATURE [Part::MultiFuse] Fusion025  label="bck"
  Shapes = -> [Box039,Extrude022]
FEATURE [Part::Cut] Cut032  label="cover"
  Base = -> Fusion025
  Refine = true
  Tool = -> Box044
FEATURE [App::Part] Part013  label="Case"
  Group = -> [Cylinder035,Cylinder036,Cylinder037,Sketch020,Sketch021,Extrude020,Extrude021,Cylinder038,Cut030,Cut029,Fusion024,Cut027,Cut028,Fusion026,Box040,Box042,Box043,Box041,Cut031,Box039,Sketch022,Extrude022,Fusion025,Box044,Cut032]
  Origin = -> Origin041
FEATURE [Part::FeaturePython] Tube  # WARN: FeaturePython — macro-defined, semantics opaque (R4)
  AttacherType = Attacher::AttachEngine3D
  Height = 16
  InnerRadius = 3.4
  OuterRadius = 3.5
  Placement = pos=(0,27,13.5) rot=(1,0,0;1.5708rad)
FEATURE [Part::MultiFuse] Fusion003
  Shapes = -> [Tube,Extrude019,Cylinder033,Part__Feature358,Part__Feature359,Cylinder034,Part__Feature360]
FEATURE [App::Part] Part012  label="Lightning_Arrestor"
  Group = -> [Cylinder033,Cylinder034,Sketch019,Part__Feature358,Part__Feature359,Tube,Part__Feature360,Extrude019,Fusion003]
  Origin = -> Origin040
  Placement = pos=(0,5.5,0) rot=(0,0,1;0rad)
FEATURE [Part::Compound] Compound004  label="lightningArrester"
  Links = -> [Part012,Part013]
  Placement = pos=(110,140,-87.25) rot=(0,-0.707107,0.707107;3.14159rad)
FEATURE [Part::Compound] Compound005  label="loraWan"
  Links = -> [Part005,Part007]
  Placement = pos=(0,0,57) rot=(0,0,1;0rad)
FEATURE [Part::Box] Box060  label="Cube035"
  AttacherType = Attacher::AttachEngine3D
  Height = 49
  Length = 38
  Placement = pos=(-0.34,0,0) rot=(0,0,1;0rad)
  Width = 17
FEATURE [Part::Box] Box061  label="Cube036"
  AttacherType = Attacher::AttachEngine3D
  Height = 59
  Length = 47.5
  Placement = pos=(-5,0,-5) rot=(0,0,1;0rad)
  Width = 22
FEATURE [Part::Box] Box009  label="stand1"
  AttacherType = Attacher::AttachEngine3D
  Height = 60
  Length = 15
  Placement = pos=(11.5,9,54) rot=(0,0,1;0rad)
  Width = 13
FEATURE [Part::Box] Box011  label="base001"
  AttacherType = Attacher::AttachEngine3D
  Height = 10
  Length = 115
  Placement = pos=(11.5,9,114) rot=(0,0,1;0rad)
  Width = 13
FEATURE [Part::Box] Box012  label="stand002"
  AttacherType = Attacher::AttachEngine3D
  Height = 60
  Length = 15
  Placement = pos=(111.5,9,54) rot=(0,0,1;0rad)
  Width = 13
FEATURE [Part::Box] Box062  label="Cube006"
  AttacherType = Attacher::AttachEngine3D
  Height = 49
  Length = 38
  Placement = pos=(-0.34,0,0) rot=(0,0,1;0rad)
  Width = 17
FEATURE [Part::Box] Box063  label="Cube007"
  AttacherType = Attacher::AttachEngine3D
  Height = 59
  Length = 47.5
  Placement = pos=(-5,0,-5) rot=(0,0,1;0rad)
  Width = 22
FEATURE [Part::Cut] Cut043  label="Hollow_CubeBase"
  Base = -> Box061
  Refine = true
  Tool = -> Box060
FEATURE [Part::Cut] Cut044  label="Hollow_CubeBase001"
  Base = -> Box063
  Placement = pos=(100,0,0) rot=(0,0,1;0rad)
  Refine = true
  Tool = -> Box062
FEATURE [Part::Cylinder] Cylinder055  label="m3_1"
  Angle = 360
  AttacherType = Attacher::AttachEngine3D
  FirstAngle = 0
  Height = 20
  Placement = pos=(57.5,15,109) rot=(0,0,1;0rad)
  Radius = 1.6
  SecondAngle = 0
FEATURE [Part::Cylinder] Cylinder056  label="m3_2"
  Angle = 360
  AttacherType = Attacher::AttachEngine3D
  FirstAngle = 0
  Height = 20
  Placement = pos=(80,15,109) rot=(0,0,1;0rad)
  Radius = 1.6
  SecondAngle = 0
FEATURE [Part::Cylinder] Cylinder057  label="m3_3"
  Angle = 360
  AttacherType = Attacher::AttachEngine3D
  FirstAngle = 0
  Height = 20
  Placement = pos=(57.5,32,109) rot=(0,0,1;0rad)
  Radius = 1.6
  SecondAngle = 0
FEATURE [Part::Cylinder] Cylinder058  label="m3_4"
  Angle = 360
  AttacherType = Attacher::AttachEngine3D
  FirstAngle = 0
  Height = 20
  Placement = pos=(80,32,109) rot=(0,0,1;0rad)
  Radius = 1.6
  SecondAngle = 0
FEATURE [Part::MultiFuse] Fusion042  label="m3_cyl"
  Refine = true
  Shapes = -> [Cylinder055,Cylinder056,Cylinder057,Cylinder058]
FEATURE [Part::MultiFuse] Fusion005  label="baseFusion"
  Refine = true
  Shapes = -> [Box009,Box011,Box012]
FEATURE [Part::MultiFuse] Fusion041  label="gpsHolder"
  Shapes = -> [Fusion005,Cut043,Cut044]
FEATURE [Part::Cut] Cut045  label="gpsHolder001"
  Base = -> Fusion041
  Tool = -> Fusion042
FEATURE [Sketcher::SketchObject] Sketch029
  ArcFitTolerance = 1e-06
  FullyConstrained = true
  MakeInternals = false
  MapMode = 5
  Placement = pos=(0,-48,0) rot=(1,0,0;1.5708rad)
  sketch-geometry (8):
    g0: LineSegment StartX=16.5 StartY=9 StartZ=0 EndX=16.5 EndY=-1 EndZ=0
    g1: LineSegment StartX=16.5 StartY=-1 StartZ=0 EndX=21.5 EndY=-1 EndZ=0
    g2: LineSegment StartX=21.5 StartY=-1 StartZ=0 EndX=21.5 EndY=9 EndZ=0
    g3: LineSegment StartX=21.5 StartY=9 StartZ=0 EndX=16.5 EndY=9 EndZ=0
    g4: LineSegment StartX=116.5 StartY=9 StartZ=0 EndX=116.5 EndY=0 EndZ=0
    g5: LineSegment StartX=116.5 StartY=0 StartZ=0 EndX=121.5 EndY=0 EndZ=0
    g6: LineSegment StartX=121.5 StartY=0 StartZ=0 EndX=121.5 EndY=9 EndZ=0
    g7: LineSegment StartX=121.5 StartY=9 StartZ=0 EndX=116.5 EndY=9 EndZ=0
  constraints (25):
    c: Coincident(g0,g1)
    c: Coincident(g1,g2)
    c: Coincident(g2,g3)
    c: Coincident(g3,g0)
    c: Vertical(g0)
    c: Vertical(g2)
    c: Horizontal(g1)
    c: Horizontal(g3)
    c: PointOnObject(g1,g-1)
    c: Coincident(g4,g5)
    c: Coincident(g5,g6)
    c: Coincident(g6,g7)
    c: Coincident(g7,g4)
    c: Vertical(g4)
    c: Vertical(g6)
    c: Horizontal(g5)
    c: Horizontal(g7)
    c: PointOnObject(g5,g-1)
    c: DistanceY(g0,g0) = 10
    c: DistanceX(g0) = 16.5
    c: DistanceX(g0,g1) = 5
    c: Horizontal(g4,g2)
    c: DistanceX(g4,g5) = 5
    c: DistanceX(g4) = 116.5
    c: DistanceY(g0) = 9
FEATURE [Part::Extrusion] Extrude028
  Base = -> Sketch029
  Dir = (0,-1,2e-16)
  DirMode = 2
  FaceMakerClass = Part::FaceMakerBullseye
  FaceMakerMode = 3
  LengthFwd = 10
  LengthRev = 0
  Placement = pos=(0,57,45) rot=(0,0,1;0rad)
  Solid = true
  Symmetric = false
FEATURE [Part::Cut] Cut046  label="gpsHolder004"
  Base = -> Cut045
  Tool = -> Extrude028
FEATURE [Part::Fillet] Fillet031
  Base = -> Cut046
  EdgeLinks = -> Cut046 [Edge1,Edge4,Edge9,Edge26,Edge34,Edge44,Edge45,Edge46,Edge47,Edge52,Edge56,Edge61,Edge74,Edge75,Edge76,Edge77,Edge81,Edge83,Edge93,Edge95,Edge98,Edge99,Edge103,Edge104]
  Edges = 24 edges r=4: [Edge1,Edge4,Edge9,Edge26,Edge34,Edge44,Edge45,Edge46,Edge47,Edge52,Edge56,Edge61,Edge74,Edge75,Edge76,Edge77,Edge81,Edge83,Edge93,Edge95,Edge98,Edge99,Edge103,Edge104]
FEATURE [Part::Fillet] Fillet032
  Base = -> Fillet031
  EdgeLinks = -> Fillet031 [Edge142,Edge157,Edge162,Edge164,Edge166,Edge167,Edge170,Edge172,Edge173,Edge175,Edge177,Edge179,Edge180,Edge183,Edge185,Edge186]
  Edges = 16 edges r=2: [Edge142,Edge157,Edge162,Edge164,Edge166,Edge167,Edge170,Edge172,Edge173,Edge175,Edge177,Edge179,Edge180,Edge183,Edge185,Edge186]
FEATURE [Part::Fillet] Fillet033  label="gpsHolder005"
  Base = -> Fillet032
  EdgeLinks = -> Fillet032 [Edge52,Edge54,Edge56,Edge57,Edge59,Edge64,Edge66,Edge68,Edge69,Edge103,Edge104,Edge105,Edge124,Edge135,Edge149,Edge150,Edge151,Edge154,Edge155,Edge156,Edge157,Edge158,Edge159,Edge160]
  Edges = 24 edges r=3: [Edge52,Edge54,Edge56,Edge57,Edge59,Edge64,Edge66,Edge68,Edge69,Edge103,Edge104,Edge105,Edge124,Edge135,Edge149,Edge150,Edge151,Edge154,Edge155,Edge156,Edge157,Edge158,Edge159,Edge160]
  Placement = pos=(-68.75,4.52e-14,205) rot=(1,0,0;4.71239rad)
FEATURE [Part::Box] Box008  label="Cube008"
  AttacherType = Attacher::AttachEngine3D
  Height = 51
  Length = 73
  Placement = pos=(-25,-23,-45) rot=(0,0,1;0rad)
  Width = 5
FEATURE [Part::Box] Box072  label="Cube045"
  AttacherType = Attacher::AttachEngine3D
  Height = 5
  Length = 10
  Placement = pos=(-35,-25.5,-45) rot=(0,0,1;0rad)
  Width = 10
FEATURE [Part::Box] Box073  label="Cube046"
  AttacherType = Attacher::AttachEngine3D
  Height = 5
  Length = 10
  Placement = pos=(48,-25.5,-45) rot=(0,0,1;0rad)
  Width = 10
FEATURE [Part::Cylinder] Cylinder059
  Angle = 360
  AttacherType = Attacher::AttachEngine3D
  FirstAngle = 0
  Height = 10
  Placement = pos=(53,-13.5,-53) rot=(0,0,1;0rad)
  Radius = 1.6
  SecondAngle = 0
FEATURE [Part::Cylinder] Cylinder060
  Angle = 360
  AttacherType = Attacher::AttachEngine3D
  FirstAngle = 0
  Height = 10
  Placement = pos=(-30,-13.5,-53) rot=(0,0,1;0rad)
  Radius = 1.6
  SecondAngle = 0
FEATURE [Part::Cylinder] Cylinder061
  Angle = 90
  AttacherType = Attacher::AttachEngine3D
  FirstAngle = 0
  Height = 5
  Placement = pos=(-25,-11,-51) rot=(0,0,1;0rad)
  Radius = 2.5
  SecondAngle = 0
FEATURE [Part::Cylinder] Cylinder062
  Angle = 90
  AttacherType = Attacher::AttachEngine3D
  FirstAngle = 0
  Height = 5
  Placement = pos=(-25,-16,-51) rot=(0,0,1;4.71239rad)
  Radius = 2.5
  SecondAngle = 0
FEATURE [Part::Cylinder] Cylinder063
  Angle = 90
  AttacherType = Attacher::AttachEngine3D
  FirstAngle = 0
  Height = 5
  Placement = pos=(48,-11,-51) rot=(0,0,1;1.5708rad)
  Radius = 2.5
  SecondAngle = 0
FEATURE [Part::Cylinder] Cylinder064
  Angle = 90
  AttacherType = Attacher::AttachEngine3D
  FirstAngle = 0
  Height = 5
  Placement = pos=(48,-16,-51) rot=(0,0,-1;3.14159rad)
  Radius = 2.5
  SecondAngle = 0
FEATURE [Part::Cylinder] Cylinder065
  Angle = 360
  AttacherType = Attacher::AttachEngine3D
  FirstAngle = 0
  Height = 10
  Placement = pos=(33,-17.5,-6) rot=(1,0,0;4.71239rad)
  Radius = 1
  SecondAngle = 0
FEATURE [Part::MultiFuse] Fusion049  label="m3Cyl001"
  Refine = true
  Shapes = -> [Cylinder059,Cylinder060]
FEATURE [Part::MultiFuse] Fusion050  label="Base_support"
  Refine = true
  Shapes = -> [Cylinder061,Cylinder062,Cylinder063,Cylinder064]
FEATURE [Sketcher::SketchObject] Sketch030
  ArcFitTolerance = 1e-06
  FullyConstrained = true
  MakeInternals = false
  sketch-geometry (8):
    g0: LineSegment StartX=-5 StartY=15 StartZ=0 EndX=-5 EndY=-12 EndZ=0
    g1: LineSegment StartX=-5 StartY=-12 StartZ=0 EndX=48 EndY=-12 EndZ=0
    g2: LineSegment StartX=48 StartY=-12 StartZ=0 EndX=48 EndY=15 EndZ=0
    g3: LineSegment StartX=48 StartY=15 StartZ=0 EndX=-5 EndY=15 EndZ=0
    g4: Circle CenterX=1.275 CenterY=8.5 CenterZ=0 NormalX=0 NormalY=0 NormalZ=1 AngleXU=0 Radius=1
    g5: Circle CenterX=1.275 CenterY=-6.725 CenterZ=0 NormalX=0 NormalY=0 NormalZ=1 AngleXU=0 Radius=1
    g6: Circle CenterX=41.91 CenterY=8.5 CenterZ=0 NormalX=0 NormalY=0 NormalZ=1 AngleXU=0 Radius=1
    g7: Circle CenterX=41.91 CenterY=-6.725 CenterZ=0 NormalX=0 NormalY=0 NormalZ=1 AngleXU=0 Radius=1
  constraints (24):
    c: Vertical(g0)
    c: Coincident(g1,g0)
    c: Horizontal(g1)
    c: Coincident(g2,g1)
    c: Vertical(g2)
    c: Coincident(g3,g2)
    c: Coincident(g3,g0)
    c: Horizontal(g3)
    c: Distance(g0,g-1) = 12
    c: Distance(g-1,g0) = 5
    c: Distance(g0,g-1) = 15
    c: Distance(g2,g-2) = 48
    c: Equal(g4,g5)
    c: Equal(g4,g6)
    c: Equal(g4,g7)
    c: Diameter(g4) = 2
    c: Distance(g4,g-1) = 8.5
    c: Distance(g4,g0) = 6.275
    c: Distance(g5,g0) = 6.275
    c: Distance(g7,g-2) = 41.91
    c: Distance(g6,g-2) = 41.91
    c: Distance(g6,g-1) = 8.5
    c: Distance(g5,g-1) = 6.725
    c: Distance(g7,g-1) = 6.725
FEATURE [Part::Extrusion] Extrude029  label="arduinoHold"
  Base = -> Sketch030
  Dir = (0,0,1)
  DirMode = 2
  FaceMakerClass = Part::FaceMakerBullseye
  FaceMakerMode = 3
  LengthFwd = 3
  LengthRev = 0
  Reversed = true
  Solid = true
  Symmetric = false
FEATURE [Sketcher::SketchObject] Sketch032
  ArcFitTolerance = 0
  FullyConstrained = true
  MakeInternals = false
  sketch-geometry (29):
    g0: LineSegment StartX=0 StartY=0 StartZ=0 EndX=8 EndY=2e-16 EndZ=0
    g1: LineSegment StartX=12 StartY=0 StartZ=0 EndX=28 EndY=2e-16 EndZ=0
    g2: LineSegment StartX=0 StartY=0 StartZ=0 EndX=-4e-16 EndY=8 EndZ=0
    g3: LineSegment StartX=1e-16 StartY=52 StartZ=0 EndX=0 EndY=60 EndZ=0
    g4: LineSegment StartX=0 StartY=60 StartZ=0 EndX=8 EndY=60 EndZ=0
    g5: LineSegment StartX=12 StartY=60 StartZ=0 EndX=28 EndY=60 EndZ=0
    g6: LineSegment StartX=32 StartY=60 StartZ=0 EndX=40 EndY=60 EndZ=0
    g7: LineSegment StartX=40 StartY=60 StartZ=0 EndX=40 EndY=52 EndZ=0
    g8: LineSegment StartX=40 StartY=48 StartZ=0 EndX=40 EndY=32 EndZ=0
    g9: LineSegment StartX=40 StartY=28 StartZ=0 EndX=40 EndY=12 EndZ=0
    g10: LineSegment StartX=40 StartY=8 StartZ=0 EndX=40 EndY=0 EndZ=0
    g11: LineSegment StartX=40 StartY=0 StartZ=0 EndX=32 EndY=-5e-16 EndZ=0
    g12: LineSegment StartX=-4e-16 StartY=48 StartZ=0 EndX=6e-16 EndY=32 EndZ=0
    g13: LineSegment StartX=-4e-16 StartY=28 StartZ=0 EndX=1e-16 EndY=12 EndZ=0
    g14: ArcOfCircle CenterX=10 CenterY=0 CenterZ=0 NormalX=0 NormalY=0 NormalZ=1 AngleXU=0 Radius=2 StartAngle=0 EndAngle=3.14159
    g15: ArcOfCircle CenterX=30 CenterY=0 CenterZ=0 NormalX=0 NormalY=0 NormalZ=1 AngleXU=0 Radius=2 StartAngle=3.14159 EndAngle=6.28319
    g16: ArcOfCircle CenterX=0 CenterY=10 CenterZ=0 NormalX=0 NormalY=0 NormalZ=1 AngleXU=0 Radius=2 StartAngle=1.5708 EndAngle=4.71239
    g17: ArcOfCircle CenterX=0 CenterY=30 CenterZ=0 NormalX=0 NormalY=0 NormalZ=1 AngleXU=0 Radius=2 StartAngle=4.71239 EndAngle=7.85398
    g18: ArcOfCircle CenterX=0 CenterY=50 CenterZ=0 NormalX=0 NormalY=0 NormalZ=1 AngleXU=0 Radius=2 StartAngle=1.5708 EndAngle=4.71239
    g19: ArcOfCircle CenterX=10 CenterY=60 CenterZ=0 NormalX=0 NormalY=0 NormalZ=1 AngleXU=0 Radius=2 StartAngle=3.14159 EndAngle=6.28319
    g20: ArcOfCircle CenterX=30 CenterY=60 CenterZ=0 NormalX=0 NormalY=0 NormalZ=1 AngleXU=0 Radius=2 StartAngle=4e-16 EndAngle=3.14159
    g21: ArcOfCircle CenterX=40 CenterY=50 CenterZ=0 NormalX=0 NormalY=0 NormalZ=1 AngleXU=0 Radius=2 StartAngle=1.5708 EndAngle=4.71239
    g22: ArcOfCircle CenterX=40 CenterY=30 CenterZ=0 NormalX=0 NormalY=0 NormalZ=1 AngleXU=0 Radius=2 StartAngle=4.71239 EndAngle=7.85398
    g23: ArcOfCircle CenterX=40 CenterY=10 CenterZ=0 NormalX=0 NormalY=0 NormalZ=1 AngleXU=0 Radius=2 StartAngle=1.5708 EndAngle=4.71239
    g24: Circle CenterX=30 CenterY=0 CenterZ=0 NormalX=0 NormalY=0 NormalZ=1 AngleXU=0 Radius=1
    g25: Circle CenterX=40 CenterY=30 CenterZ=0 NormalX=0 NormalY=0 NormalZ=1 AngleXU=0 Radius=1
    g26: Circle CenterX=30 CenterY=60 CenterZ=0 NormalX=0 NormalY=0 NormalZ=1 AngleXU=0 Radius=1
    g27: Circle CenterX=0 CenterY=50 CenterZ=0 NormalX=0 NormalY=0 NormalZ=1 AngleXU=0 Radius=1
    g28: Circle CenterX=0 CenterY=10 CenterZ=0 NormalX=0 NormalY=0 NormalZ=1 AngleXU=0 Radius=1
  constraints (88):
    c: Coincident(g0,g-1)
    c: PointOnObject(g0,g-1)
    c: PointOnObject(g1,g-1)
    c: PointOnObject(g1,g-1)
    c: Coincident(g2,g0)
    c: PointOnObject(g2,g-2)
    c: PointOnObject(g3,g-2)
    c: PointOnObject(g3,g-2)
    c: Coincident(g4,g3)
    c: Horizontal(g4)
    c: Horizontal(g5)
    c: Coincident(g7,g6)
    c: Vertical(g7)
    c: Vertical(g8)
    c: Vertical(g9)
    c: PointOnObject(g10,g-1)
    c: Coincident(g11,g10)
    c: PointOnObject(g11,g-1)
    c: PointOnObject(g12,g-2)
    c: PointOnObject(g12,g-2)
    c: PointOnObject(g13,g-2)
    c: PointOnObject(g13,g-2)
    c: Distance(g0) = 8
    c: Coincident(g14,g0)
    c: Coincident(g14,g1)
    c: Diameter(g14) = 4
    c: Distance(g1) = 16
    c: Coincident(g15,g1)
    c: Coincident(g15,g11)
    c: Diameter(g15) = 4
    c: PointOnObject(g15,g-1)
    c: Distance(g11) = 8
    c: Vertical(g10)
    c: Distance(g2) = 8
    c: Coincident(g16,g2)
    c: Coincident(g16,g13)
    c: PointOnObject(g16,g-2)
    c: Diameter(g16) = 4
    c: Distance(g13) = 16
    c: Distance(g12) = 16
    c: PointOnObject(g14,g-1)
    c: Coincident(g17,g13)
    c: Coincident(g17,g12)
    c: PointOnObject(g17,g-2)
    c: Diameter(g17) = 4
    c: Coincident(g18,g12)
    c: Coincident(g18,g3)
    c: PointOnObject(g18,g-2)
    c: Diameter(g18) = 4
    c: Distance(g3) = 8
    c: Distance(g4) = 8
    c: Coincident(g19,g4)
    c: Coincident(g19,g5)
    c: Distance(g19,g-1) = 60
    c: Diameter(g19) = 4
    c: Distance(g5) = 16
    c: Distance(g3,g5) = 12
    c: Coincident(g20,g5)
    c: Coincident(g20,g6)
    c: Distance(g20,g-1) = 60
    c: Diameter(g20) = 4
    c: Distance(g6,g-1) = 60
    c: Horizontal(g6)
    c: Distance(g6) = 8
    c: Distance(g7) = 8
    c: Coincident(g21,g7)
    c: Coincident(g21,g8)
    c: Distance(g18,g21) = 40
    c: Distance(g8) = 16
    c: Diameter(g21) = 4
    c: Distance(g8,g-2) = 40
    c: Distance(g9) = 16
    c: Distance(g9,g-2) = 40
    c: Coincident(g22,g8)
    c: Coincident(g22,g9)
    c: Diameter(g22) = 4
    c: Distance(g22,g17) = 40
    c: Coincident(g23,g9)
    c: Coincident(g23,g10)
    c: Diameter(g23) = 4
    c: Distance(g16,g23) = 40
    c: Coincident(g24,g15)
    c: Coincident(g25,g22)
    c: Coincident(g26,g20)
    c: Coincident(g27,g18)
    c: Coincident(g28,g16)
    c: Equal(g24, g25-g28) x4
    c: Diameter(g24) = 2
FEATURE [Part::Extrusion] Extrude031
  Base = -> Sketch032
  Dir = (0,0,1)
  DirMode = 2
  FaceMakerClass = Part::FaceMakerBullseye
  FaceMakerMode = 3
  LengthFwd = 5
  LengthRev = 0
  Placement = pos=(-17,-18,0) rot=(-0.57735,-0.57735,0.57735;4.18879rad)
  Solid = true
  Symmetric = false
FEATURE [Sketcher::SketchObject] Sketch033
  ArcFitTolerance = 0
  FullyConstrained = true
  MakeInternals = false
  sketch-geometry (29):
    g0: LineSegment StartX=0 StartY=0 StartZ=0 EndX=8 EndY=2e-16 EndZ=0
    g1: LineSegment StartX=12 StartY=0 StartZ=0 EndX=28 EndY=2e-16 EndZ=0
    g2: LineSegment StartX=0 StartY=0 StartZ=0 EndX=-4e-16 EndY=8 EndZ=0
    g3: LineSegment StartX=1e-16 StartY=52 StartZ=0 EndX=0 EndY=60 EndZ=0
    g4: LineSegment StartX=0 StartY=60 StartZ=0 EndX=8 EndY=60 EndZ=0
    g5: LineSegment StartX=12 StartY=60 StartZ=0 EndX=28 EndY=60 EndZ=0
    g6: LineSegment StartX=32 StartY=60 StartZ=0 EndX=40 EndY=60 EndZ=0
    g7: LineSegment StartX=40 StartY=60 StartZ=0 EndX=40 EndY=52 EndZ=0
    g8: LineSegment StartX=40 StartY=48 StartZ=0 EndX=40 EndY=32 EndZ=0
    g9: LineSegment StartX=40 StartY=28 StartZ=0 EndX=40 EndY=12 EndZ=0
    g10: LineSegment StartX=40 StartY=8 StartZ=0 EndX=40 EndY=0 EndZ=0
    g11: LineSegment StartX=40 StartY=0 StartZ=0 EndX=32 EndY=-5e-16 EndZ=0
    g12: LineSegment StartX=-4e-16 StartY=48 StartZ=0 EndX=6e-16 EndY=32 EndZ=0
    g13: LineSegment StartX=-4e-16 StartY=28 StartZ=0 EndX=1e-16 EndY=12 EndZ=0
    g14: ArcOfCircle CenterX=10 CenterY=0 CenterZ=0 NormalX=0 NormalY=0 NormalZ=1 AngleXU=0 Radius=2 StartAngle=0 EndAngle=3.14159
    g15: ArcOfCircle CenterX=30 CenterY=0 CenterZ=0 NormalX=0 NormalY=0 NormalZ=1 AngleXU=0 Radius=2 StartAngle=3.14159 EndAngle=6.28319
    g16: ArcOfCircle CenterX=0 CenterY=10 CenterZ=0 NormalX=0 NormalY=0 NormalZ=1 AngleXU=0 Radius=2 StartAngle=1.5708 EndAngle=4.71239
    g17: ArcOfCircle CenterX=0 CenterY=30 CenterZ=0 NormalX=0 NormalY=0 NormalZ=1 AngleXU=0 Radius=2 StartAngle=4.71239 EndAngle=7.85398
    g18: ArcOfCircle CenterX=0 CenterY=50 CenterZ=0 NormalX=0 NormalY=0 NormalZ=1 AngleXU=0 Radius=2 StartAngle=1.5708 EndAngle=4.71239
    g19: ArcOfCircle CenterX=10 CenterY=60 CenterZ=0 NormalX=0 NormalY=0 NormalZ=1 AngleXU=0 Radius=2 StartAngle=3.14159 EndAngle=6.28319
    g20: ArcOfCircle CenterX=30 CenterY=60 CenterZ=0 NormalX=0 NormalY=0 NormalZ=1 AngleXU=0 Radius=2 StartAngle=4e-16 EndAngle=3.14159
    g21: ArcOfCircle CenterX=40 CenterY=50 CenterZ=0 NormalX=0 NormalY=0 NormalZ=1 AngleXU=0 Radius=2 StartAngle=1.5708 EndAngle=4.71239
    g22: ArcOfCircle CenterX=40 CenterY=30 CenterZ=0 NormalX=0 NormalY=0 NormalZ=1 AngleXU=0 Radius=2 StartAngle=4.71239 EndAngle=7.85398
    g23: ArcOfCircle CenterX=40 CenterY=10 CenterZ=0 NormalX=0 NormalY=0 NormalZ=1 AngleXU=0 Radius=2 StartAngle=1.5708 EndAngle=4.71239
    g24: Circle CenterX=30 CenterY=0 CenterZ=0 NormalX=0 NormalY=0 NormalZ=1 AngleXU=0 Radius=1
    g25: Circle CenterX=40 CenterY=30 CenterZ=0 NormalX=0 NormalY=0 NormalZ=1 AngleXU=0 Radius=1
    g26: Circle CenterX=30 CenterY=60 CenterZ=0 NormalX=0 NormalY=0 NormalZ=1 AngleXU=0 Radius=1
    g27: Circle CenterX=0 CenterY=50 CenterZ=0 NormalX=0 NormalY=0 NormalZ=1 AngleXU=0 Radius=1
    g28: Circle CenterX=0 CenterY=10 CenterZ=0 NormalX=0 NormalY=0 NormalZ=1 AngleXU=0 Radius=1
  constraints (88):
    c: Coincident(g0,g-1)
    c: PointOnObject(g0,g-1)
    c: PointOnObject(g1,g-1)
    c: PointOnObject(g1,g-1)
    c: Coincident(g2,g0)
    c: PointOnObject(g2,g-2)
    c: PointOnObject(g3,g-2)
    c: PointOnObject(g3,g-2)
    c: Coincident(g4,g3)
    c: Horizontal(g4)
    c: Horizontal(g5)
    c: Coincident(g7,g6)
    c: Vertical(g7)
    c: Vertical(g8)
    c: Vertical(g9)
    c: PointOnObject(g10,g-1)
    c: Coincident(g11,g10)
    c: PointOnObject(g11,g-1)
    c: PointOnObject(g12,g-2)
    c: PointOnObject(g12,g-2)
    c: PointOnObject(g13,g-2)
    c: PointOnObject(g13,g-2)
    c: Distance(g0) = 8
    c: Coincident(g14,g0)
    c: Coincident(g14,g1)
    c: Diameter(g14) = 4
    c: Distance(g1) = 16
    c: Coincident(g15,g1)
    c: Coincident(g15,g11)
    c: Diameter(g15) = 4
    c: PointOnObject(g15,g-1)
    c: Distance(g11) = 8
    c: Vertical(g10)
    c: Distance(g2) = 8
    c: Coincident(g16,g2)
    c: Coincident(g16,g13)
    c: PointOnObject(g16,g-2)
    c: Diameter(g16) = 4
    c: Distance(g13) = 16
    c: Distance(g12) = 16
    c: PointOnObject(g14,g-1)
    c: Coincident(g17,g13)
    c: Coincident(g17,g12)
    c: PointOnObject(g17,g-2)
    c: Diameter(g17) = 4
    c: Coincident(g18,g12)
    c: Coincident(g18,g3)
    c: PointOnObject(g18,g-2)
    c: Diameter(g18) = 4
    c: Distance(g3) = 8
    c: Distance(g4) = 8
    c: Coincident(g19,g4)
    c: Coincident(g19,g5)
    c: Distance(g19,g-1) = 60
    c: Diameter(g19) = 4
    c: Distance(g5) = 16
    c: Distance(g3,g5) = 12
    c: Coincident(g20,g5)
    c: Coincident(g20,g6)
    c: Distance(g20,g-1) = 60
    c: Diameter(g20) = 4
    c: Distance(g6,g-1) = 60
    c: Horizontal(g6)
    c: Distance(g6) = 8
    c: Distance(g7) = 8
    c: Coincident(g21,g7)
    c: Coincident(g21,g8)
    c: Distance(g18,g21) = 40
    c: Distance(g8) = 16
    c: Diameter(g21) = 4
    c: Distance(g8,g-2) = 40
    c: Distance(g9) = 16
    c: Distance(g9,g-2) = 40
    c: Coincident(g22,g8)
    c: Coincident(g22,g9)
    c: Diameter(g22) = 4
    c: Distance(g22,g17) = 40
    c: Coincident(g23,g9)
    c: Coincident(g23,g10)
    c: Diameter(g23) = 4
    c: Distance(g16,g23) = 40
    c: Coincident(g24,g15)
    c: Coincident(g25,g22)
    c: Coincident(g26,g20)
    c: Coincident(g27,g18)
    c: Coincident(g28,g16)
    c: Equal(g24, g25-g28) x4
    c: Diameter(g24) = 2
FEATURE [Part::Extrusion] Extrude032
  Base = -> Sketch033
  Dir = (0,0,1)
  DirMode = 2
  FaceMakerClass = Part::FaceMakerBullseye
  FaceMakerMode = 3
  LengthFwd = 5
  LengthRev = 0
  Placement = pos=(-17,-18,0) rot=(-0.57735,-0.57735,0.57735;4.18879rad)
  Solid = true
  Symmetric = false
FEATURE [Part::Cut] Cut047  label="base_cut"
  Base = -> Box008
  Refine = true
  Tool = -> Extrude032
FEATURE [Part::MultiFuse] Fusion046
  Refine = true
  Shapes = -> [Cut047,Box072,Box073]
FEATURE [Part::MultiFuse] Fusion047  label="ssrHold"
  Placement = pos=(0,7,-6) rot=(0,0,1;0rad)
  Refine = true
  Shapes = -> [Extrude031,Fusion046]
FEATURE [Part::MultiFuse] Fusion048  label="fusedHold"
  Refine = true
  Shapes = -> [Extrude029,Fusion047]
FEATURE [Part::Cut] Cut048  label="ssr_nano_hold"
  Base = -> Fusion048
  Refine = true
  Tool = -> Fusion049
FEATURE [Part::MultiFuse] Fusion051  label="SSR_Nano"
  Refine = true
  Shapes = -> [Cut048,Fusion050]
FEATURE [Sketcher::SketchObject] Sketch034
  ArcFitTolerance = 0
  FullyConstrained = true
  MakeInternals = false
  sketch-geometry (24):
    g0: LineSegment StartX=0 StartY=0 StartZ=0 EndX=8 EndY=2e-16 EndZ=0
    g1: LineSegment StartX=12 StartY=0 StartZ=0 EndX=28 EndY=2e-16 EndZ=0
    g2: LineSegment StartX=0 StartY=0 StartZ=0 EndX=-4e-16 EndY=8 EndZ=0
    g3: LineSegment StartX=1e-16 StartY=52 StartZ=0 EndX=0 EndY=60 EndZ=0
    g4: LineSegment StartX=0 StartY=60 StartZ=0 EndX=8 EndY=60 EndZ=0
    g5: LineSegment StartX=12 StartY=60 StartZ=0 EndX=28 EndY=60 EndZ=0
    g6: LineSegment StartX=32 StartY=60 StartZ=0 EndX=40 EndY=60 EndZ=0
    g7: LineSegment StartX=40 StartY=60 StartZ=0 EndX=40 EndY=52 EndZ=0
    g8: LineSegment StartX=40 StartY=48 StartZ=0 EndX=40 EndY=32 EndZ=0
    g9: LineSegment StartX=40 StartY=28 StartZ=0 EndX=40 EndY=12 EndZ=0
    g10: LineSegment StartX=40 StartY=8 StartZ=0 EndX=40 EndY=0 EndZ=0
    g11: LineSegment StartX=40 StartY=0 StartZ=0 EndX=32 EndY=-5e-16 EndZ=0
    g12: LineSegment StartX=-4e-16 StartY=48 StartZ=0 EndX=6e-16 EndY=32 EndZ=0
    g13: LineSegment StartX=-4e-16 StartY=28 StartZ=0 EndX=1e-16 EndY=12 EndZ=0
    g14: ArcOfCircle CenterX=10 CenterY=0 CenterZ=0 NormalX=0 NormalY=0 NormalZ=1 AngleXU=0 Radius=2 StartAngle=0 EndAngle=3.14159
    g15: ArcOfCircle CenterX=30 CenterY=0 CenterZ=0 NormalX=0 NormalY=0 NormalZ=1 AngleXU=0 Radius=2 StartAngle=3.14159 EndAngle=6.28319
    g16: ArcOfCircle CenterX=0 CenterY=10 CenterZ=0 NormalX=0 NormalY=0 NormalZ=1 AngleXU=0 Radius=2 StartAngle=1.5708 EndAngle=4.71239
    g17: ArcOfCircle CenterX=0 CenterY=30 CenterZ=0 NormalX=0 NormalY=0 NormalZ=1 AngleXU=0 Radius=2 StartAngle=4.71239 EndAngle=7.85398
    g18: ArcOfCircle CenterX=0 CenterY=50 CenterZ=0 NormalX=0 NormalY=0 NormalZ=1 AngleXU=0 Radius=2 StartAngle=1.5708 EndAngle=4.71239
    g19: ArcOfCircle CenterX=10 CenterY=60 CenterZ=0 NormalX=0 NormalY=0 NormalZ=1 AngleXU=0 Radius=2 StartAngle=3.14159 EndAngle=6.28319
    g20: ArcOfCircle CenterX=30 CenterY=60 CenterZ=0 NormalX=0 NormalY=0 NormalZ=1 AngleXU=0 Radius=2 StartAngle=4e-16 EndAngle=3.14159
    g21: ArcOfCircle CenterX=40 CenterY=50 CenterZ=0 NormalX=0 NormalY=0 NormalZ=1 AngleXU=0 Radius=2 StartAngle=1.5708 EndAngle=4.71239
    g22: ArcOfCircle CenterX=40 CenterY=30 CenterZ=0 NormalX=0 NormalY=0 NormalZ=1 AngleXU=0 Radius=2 StartAngle=4.71239 EndAngle=7.85398
    g23: ArcOfCircle CenterX=40 CenterY=10 CenterZ=0 NormalX=0 NormalY=0 NormalZ=1 AngleXU=0 Radius=2 StartAngle=1.5708 EndAngle=4.71239
  constraints (81):
    c: Coincident(g0,g-1)
    c: PointOnObject(g0,g-1)
    c: PointOnObject(g1,g-1)
    c: PointOnObject(g1,g-1)
    c: Coincident(g2,g0)
    c: PointOnObject(g2,g-2)
    c: PointOnObject(g3,g-2)
    c: PointOnObject(g3,g-2)
    c: Coincident(g4,g3)
    c: Horizontal(g4)
    c: Horizontal(g5)
    c: Coincident(g7,g6)
    c: Vertical(g7)
    c: Vertical(g8)
    c: Vertical(g9)
    c: PointOnObject(g10,g-1)
    c: Coincident(g11,g10)
    c: PointOnObject(g11,g-1)
    c: PointOnObject(g12,g-2)
    c: PointOnObject(g12,g-2)
    c: PointOnObject(g13,g-2)
    c: PointOnObject(g13,g-2)
    c: Distance(g0) = 8
    c: Coincident(g14,g0)
    c: Coincident(g14,g1)
    c: Diameter(g14) = 4
    c: Distance(g1) = 16
    c: Coincident(g15,g1)
    c: Coincident(g15,g11)
    c: Diameter(g15) = 4
    c: PointOnObject(g15,g-1)
    c: Distance(g11) = 8
    c: Vertical(g10)
    c: Distance(g2) = 8
    c: Coincident(g16,g2)
    c: Coincident(g16,g13)
    c: PointOnObject(g16,g-2)
    c: Diameter(g16) = 4
    c: Distance(g13) = 16
    c: Distance(g12) = 16
    c: PointOnObject(g14,g-1)
    c: Coincident(g17,g13)
    c: Coincident(g17,g12)
    c: PointOnObject(g17,g-2)
    c: Diameter(g17) = 4
    c: Coincident(g18,g12)
    c: Coincident(g18,g3)
    c: PointOnObject(g18,g-2)
    c: Diameter(g18) = 4
    c: Distance(g3) = 8
    c: Distance(g4) = 8
    c: Coincident(g19,g4)
    c: Coincident(g19,g5)
    c: Distance(g19,g-1) = 60
    c: Diameter(g19) = 4
    c: Distance(g5) = 16
    c: Distance(g3,g5) = 12
    c: Coincident(g20,g5)
    c: Coincident(g20,g6)
    c: Distance(g20,g-1) = 60
    c: Diameter(g20) = 4
    c: Distance(g6,g-1) = 60
    c: Horizontal(g6)
    c: Distance(g6) = 8
    c: Distance(g7) = 8
    c: Coincident(g21,g7)
    c: Coincident(g21,g8)
    c: Distance(g18,g21) = 40
    c: Distance(g8) = 16
    c: Diameter(g21) = 4
    c: Distance(g8,g-2) = 40
    c: Distance(g9) = 16
    c: Distance(g9,g-2) = 40
    c: Coincident(g22,g8)
    c: Coincident(g22,g9)
    c: Diameter(g22) = 4
    c: Distance(g22,g17) = 40
    c: Coincident(g23,g9)
    c: Coincident(g23,g10)
    c: Diameter(g23) = 4
    c: Distance(g16,g23) = 40
FEATURE [Part::Cylinder] Cylinder070
  Angle = 360
  AttacherType = Attacher::AttachEngine3D
  FirstAngle = 0
  Height = 3.7
  Placement = pos=(176.78,-4,-14) rot=(0,0,1;0rad)
  Radius = 3
  SecondAngle = 0
FEATURE [Part::Cylinder] Cylinder071
  Angle = 360
  AttacherType = Attacher::AttachEngine3D
  FirstAngle = 0
  Height = 3.7
  Placement = pos=(195.78,-4,-14) rot=(0,0,1;0rad)
  Radius = 3
  SecondAngle = 0
FEATURE [Part::Cylinder] Cylinder072
  Angle = 360
  AttacherType = Attacher::AttachEngine3D
  FirstAngle = 0
  Height = 3.7
  Placement = pos=(195.78,-30,-14) rot=(0,0,1;0rad)
  Radius = 3
  SecondAngle = 0
FEATURE [Part::Cylinder] Cylinder073
  Angle = 360
  AttacherType = Attacher::AttachEngine3D
  FirstAngle = 0
  Height = 3.7
  Placement = pos=(176.78,-30,-14) rot=(0,0,1;0rad)
  Radius = 3
  SecondAngle = 0
FEATURE [Part::MultiFuse] Fusion054  label="m3_head001"
  Refine = true
  Shapes = -> [Cylinder070,Cylinder071,Cylinder072,Cylinder073]
FEATURE [Part::Feature] Part__Feature533  label="051659-8_05358-PUMPE-_SW0001"
  shape: bbox 32.37 x 50.78 x 84.45 mm, 991 faces (baked)
FEATURE [Part::Feature] Part__Feature534  label="051659-8_05358-PUMPE-_SW0002"
  shape: bbox 4 x 4 x 0.751 mm, 31 faces (baked)
FEATURE [Part::Feature] Part__Feature535  label="051659-8_05358-PUMPE-_SW0003"
  shape: bbox 4 x 4 x 0.751 mm, 31 faces (baked)
FEATURE [Part::Feature] Part__Feature536  label="051659-8_05358-PUMPE-_SW0004"
  shape: bbox 4 x 4 x 0.751 mm, 31 faces (baked)
FEATURE [Part::Feature] Part__Feature537  label="051659-8_05358-PUMPE-_SW0005"
  shape: bbox 4 x 4 x 0.751 mm, 31 faces (baked)
FEATURE [Sketcher::SketchObject] Sketch037
  ArcFitTolerance = 1e-06
  FullyConstrained = true
  MakeInternals = false
  sketch-geometry (12):
    g0: LineSegment StartX=170 StartY=6 StartZ=0 EndX=170 EndY=-40 EndZ=0
    g1: LineSegment StartX=170 StartY=-40 StartZ=0 EndX=205 EndY=-40 EndZ=0
    g2: LineSegment StartX=205 StartY=-40 StartZ=0 EndX=205 EndY=6 EndZ=0
    g3: LineSegment StartX=205 StartY=6 StartZ=0 EndX=170 EndY=6 EndZ=0
    g4: Circle CenterX=195.8 CenterY=-30 CenterZ=0 NormalX=0 NormalY=0 NormalZ=1 AngleXU=0 Radius=1.375
    g5: Circle CenterX=195.8 CenterY=-4 CenterZ=0 NormalX=0 NormalY=0 NormalZ=1 AngleXU=0 Radius=1.375
    g6: Circle CenterX=176.8 CenterY=-30 CenterZ=0 NormalX=0 NormalY=0 NormalZ=1 AngleXU=0 Radius=1.375
    g7: Circle CenterX=176.8 CenterY=-4 CenterZ=0 NormalX=0 NormalY=0 NormalZ=1 AngleXU=0 Radius=1.375
    g8: Circle CenterX=200 CenterY=-36 CenterZ=0 NormalX=0 NormalY=0 NormalZ=1 AngleXU=0 Radius=1.625
    g9: Circle CenterX=200 CenterY=2 CenterZ=0 NormalX=0 NormalY=0 NormalZ=1 AngleXU=0 Radius=1.625
    g10: Circle CenterX=175 CenterY=2 CenterZ=0 NormalX=0 NormalY=0 NormalZ=1 AngleXU=0 Radius=1.625
    g11: Circle CenterX=175 CenterY=-36 CenterZ=0 NormalX=0 NormalY=0 NormalZ=1 AngleXU=0 Radius=1.625
  constraints (36):
    c: Coincident(g0,g1)
    c: Coincident(g1,g2)
    c: Coincident(g2,g3)
    c: Coincident(g3,g0)
    c: Vertical(g0)
    c: Vertical(g2)
    c: Horizontal(g1)
    c: Horizontal(g3)
    c: DistanceX(g3,g3) = 35
    c: Distance(g0) = 46
    c: Distance(g0,g-2) = 170
    c: Distance(g0,g-1) = 40
    c: Equal(g4,g6)
    c: Equal(g4,g7)
    c: Equal(g4,g5)
    c: Diameter(g4) = 2.75
    c: Distance(g4,g2) = 9.2
    c: Distance(g7,g3) = 10
    c: Distance(g6,g1) = 10
    c: Distance(g8,g2) = 5
    c: Equal(g8,g9)
    c: Diameter(g8) = 3.25
    c: Distance(g11,g1) = 4
    c: Distance(g10,g3) = 4
    c: Distance(g10,g0) = 5
    c: Equal(g10,g11)
    c: Diameter(g10) = 3.25
    c: Horizontal(g9,g10)
    c: Horizontal(g8,g11)
    c: Horizontal(g4,g6)
    c: Horizontal(g7,g5)
    c: DistanceX(g0,g7) = 6.8
    c: Vertical(g6,g7)
    c: Vertical(g11,g10)
    c: Vertical(g8,g9)
    c: Vertical(g5,g4)
FEATURE [Part::Extrusion] Extrude036
  Base = -> Sketch037
  Dir = (0,0,1)
  DirMode = 2
  FaceMakerClass = Part::FaceMakerBullseye
  FaceMakerMode = 3
  LengthFwd = 8
  LengthRev = 0
  Placement = pos=(0,0,-14) rot=(0,0,1;0rad)
  Solid = true
  Symmetric = false
FEATURE [Part::Fillet] Fillet036  label="Holder002"
  Base = -> Extrude036
  EdgeLinks = -> Extrude036 [?Edge1,?Edge2,Edge3,Edge4,?Edge5,Edge6,Edge7,?Edge8,Edge9,Edge10,Edge11,Edge12]
  Edges = 12 edges: [Edge1 r=3,Edge2 r=3,Edge3 r=1,Edge4 r=1,Edge5 r=3,Edge6 r=1,Edge7 r=1,Edge8 r=3,Edge9 r=1,Edge10 r=1,Edge11 r=1,Edge12 r=1]
FEATURE [Part::Cut] Cut052  label="Holder_M3_cut001"
  Base = -> Fillet036
  Refine = true
  Tool = -> Fusion054
FEATURE [App::Part] _51659_8_05358_PUMPE__SW0001  label="Pump"
  Group = -> [Part__Feature533,Part__Feature534,Part__Feature535,Part__Feature536,Part__Feature537]
  Origin = -> Origin092
  Placement = pos=(183,-17,11) rot=(0.57735,0.57735,0.57735;2.0944rad)
FEATURE [App::Part] Part017
  Group = -> [_51659_8_05358_PUMPE__SW0001,Sketch037,Extrude036,Fillet036,Cylinder070,Cylinder071,Cylinder072,Cylinder073,Fusion054,Cut052]
  Origin = -> Origin093
  Placement = pos=(90,144,-10) rot=(0.57735,-0.57735,0.57735;2.0944rad)
FEATURE [Part::Box] Box084  label="Cube054"
  AttacherType = Attacher::AttachEngine3D
  Height = 21
  Length = 24
  Placement = pos=(13.5,16,0) rot=(0,0,1;0rad)
  Width = 4.5
FEATURE [Part::Box] Box085  label="Cube055"
  AttacherType = Attacher::AttachEngine3D
  Height = 21
  Length = 24
  Placement = pos=(13.5,27.5,0) rot=(0,0,1;0rad)
  Width = 4.5
FEATURE [Part::Box] Box086  label="Cube056"
  AttacherType = Attacher::AttachEngine3D
  Height = 21
  Length = 24
  Placement = pos=(13.5,39,0) rot=(0,0,1;0rad)
  Width = 4.5
FEATURE [Part::Box] Box087  label="Cube057"
  AttacherType = Attacher::AttachEngine3D
  Height = 21
  Length = 24
  Placement = pos=(13.5,50.5,0) rot=(0,0,1;0rad)
  Width = 4.5
FEATURE [Part::Box] Box088  label="Cube058"
  AttacherType = Attacher::AttachEngine3D
  Height = 15
  Length = 9
  Placement = pos=(2.5,13,0) rot=(0,0,1;0rad)
  Width = 10
FEATURE [Part::Box] Box089  label="Cube059"
  AttacherType = Attacher::AttachEngine3D
  Height = 15
  Length = 9
  Placement = pos=(2.5,24,0) rot=(0,0,1;0rad)
  Width = 10
FEATURE [Part::Box] Box090  label="Cube060"
  AttacherType = Attacher::AttachEngine3D
  Height = 15
  Length = 9
  Placement = pos=(2.5,35,0) rot=(0,0,1;0rad)
  Width = 10
FEATURE [Part::Box] Box091  label="Cube061"
  AttacherType = Attacher::AttachEngine3D
  Height = 15
  Length = 9
  Placement = pos=(2.5,46,0) rot=(0,0,1;0rad)
  Width = 10
FEATURE [Part::Box] Box092  label="Cube062"
  AttacherType = Attacher::AttachEngine3D
  Height = 51
  Length = 73
  Placement = pos=(-25,-23,-45) rot=(0,0,1;0rad)
  Width = 5
FEATURE [Part::Box] Box093  label="Cube063"
  AttacherType = Attacher::AttachEngine3D
  Height = 5
  Length = 10
  Placement = pos=(-35,-25.5,-45) rot=(0,0,1;0rad)
  Width = 10
FEATURE [Part::Box] Box010  label="Cube064"
  AttacherType = Attacher::AttachEngine3D
  Height = 5
  Length = 10
  Placement = pos=(48,-25.5,-45) rot=(0,0,1;0rad)
  Width = 10
FEATURE [Part::Cylinder] Cylinder086
  Angle = 360
  AttacherType = Attacher::AttachEngine3D
  FirstAngle = 0
  Height = 10
  Placement = pos=(53,-13.5,-53) rot=(0,0,1;0rad)
  Radius = 1.6
  SecondAngle = 0
FEATURE [Part::Cylinder] Cylinder087
  Angle = 360
  AttacherType = Attacher::AttachEngine3D
  FirstAngle = 0
  Height = 10
  Placement = pos=(-30,-13.5,-53) rot=(0,0,1;0rad)
  Radius = 1.6
  SecondAngle = 0
FEATURE [Part::Cylinder] Cylinder088
  Angle = 90
  AttacherType = Attacher::AttachEngine3D
  FirstAngle = 0
  Height = 5
  Placement = pos=(-25,-11,-51) rot=(0,0,1;0rad)
  Radius = 2.5
  SecondAngle = 0
FEATURE [Part::Cylinder] Cylinder089
  Angle = 90
  AttacherType = Attacher::AttachEngine3D
  FirstAngle = 0
  Height = 5
  Placement = pos=(-25,-16,-51) rot=(0,0,1;4.71239rad)
  Radius = 2.5
  SecondAngle = 0
FEATURE [Part::Cylinder] Cylinder090
  Angle = 90
  AttacherType = Attacher::AttachEngine3D
  FirstAngle = 0
  Height = 5
  Placement = pos=(48,-11,-51) rot=(0,0,1;1.5708rad)
  Radius = 2.5
  SecondAngle = 0
FEATURE [Part::Cylinder] Cylinder091
  Angle = 90
  AttacherType = Attacher::AttachEngine3D
  FirstAngle = 0
  Height = 5
  Placement = pos=(48,-16,-51) rot=(0,0,-1;3.14159rad)
  Radius = 2.5
  SecondAngle = 0
FEATURE [Part::Cylinder] Cylinder092
  Angle = 360
  AttacherType = Attacher::AttachEngine3D
  FirstAngle = 0
  Height = 10
  Placement = pos=(33,-17.5,-6) rot=(1,0,0;4.71239rad)
  Radius = 1.1
  SecondAngle = 0
FEATURE [Part::MultiFuse] Fusion067  label="relay'001"
  Shapes = -> [Box084,Box085,Box086,Box087]
FEATURE [Part::MultiFuse] Fusion068  label="inputs001"
  Shapes = -> [Box088,Box089,Box090,Box091]
FEATURE [Part::MultiFuse] Fusion073  label="m3Cyl"
  Refine = true
  Shapes = -> [Cylinder086,Cylinder087]
FEATURE [Part::MultiFuse] Fusion074  label="Base_support001"
  Refine = true
  Shapes = -> [Cylinder088,Cylinder089,Cylinder090,Cylinder091]
FEATURE [App::Part] Part023  label="nano_hold001"
  Origin = -> Origin144
FEATURE [Part::Feature] Part__Feature592  label="Board (1)001"
  shape: bbox 43.18 x 17.78 x 0.805 mm, 251 faces (baked)
FEATURE [Part::Feature] Part__Feature593  label="LSM9DS1TR_LGA-24_3X3P5X1_STM v029"
  Placement = pos=(21.5608,12.1142,0.754) rot=(0,0,1;0rad)
  shape: bbox 0.15 x 0.15 x 0.003 mm, 3 faces (baked)
FEATURE [Part::Feature] Part__Feature594  label="LSM9DS1TR_LGA-24_3X3P5X1_STM v030"
  Placement = pos=(21.5608,12.1142,0.754) rot=(0,0,1;0rad)
  shape: bbox 3.5 x 3 x 1.346 mm, 6 faces (baked)
FEATURE [Part::Feature] Part__Feature595  label="LSM9DS1TR_LGA-24_3X3P5X1_STM v031"
  Placement = pos=(21.5608,12.1142,0.754) rot=(0,0,1;0rad)
  shape: bbox 0.4 x 0.28 x 0.051 mm, 6 faces (baked)
FEATURE [Part::Feature] Part__Feature596  label="LSM9DS1TR_LGA-24_3X3P5X1_STM v032"
  Placement = pos=(21.5608,12.1142,0.754) rot=(0,0,1;0rad)
  shape: bbox 0.4 x 0.28 x 0.051 mm, 6 faces (baked)
FEATURE [Part::Feature] Part__Feature597  label="LSM9DS1TR_LGA-24_3X3P5X1_STM v033"
  Placement = pos=(21.5608,12.1142,0.754) rot=(0,0,1;0rad)
  shape: bbox 0.4 x 0.28 x 0.051 mm, 6 faces (baked)
FEATURE [Part::Feature] Part__Feature598  label="LSM9DS1TR_LGA-24_3X3P5X1_STM v034"
  Placement = pos=(21.5608,12.1142,0.754) rot=(0,0,1;0rad)
  shape: bbox 0.4 x 0.28 x 0.051 mm, 6 faces (baked)
FEATURE [Part::Feature] Part__Feature599  label="LSM9DS1TR_LGA-24_3X3P5X1_STM v035"
  Placement = pos=(21.5608,12.1142,0.754) rot=(0,0,1;0rad)
  shape: bbox 0.28 x 0.4 x 0.051 mm, 6 faces (baked)
FEATURE [Part::Feature] Part__Feature600  label="LSM9DS1TR_LGA-24_3X3P5X1_STM v036"
  Placement = pos=(21.5608,12.1142,0.754) rot=(0,0,1;0rad)
  shape: bbox 0.28 x 0.4 x 0.051 mm, 6 faces (baked)
FEATURE [Part::Feature] Part__Feature601  label="LSM9DS1TR_LGA-24_3X3P5X1_STM v037"
  Placement = pos=(21.5608,12.1142,0.754) rot=(0,0,1;0rad)
  shape: bbox 0.28 x 0.4 x 0.051 mm, 6 faces (baked)
FEATURE [Part::Feature] Part__Feature602  label="LSM9DS1TR_LGA-24_3X3P5X1_STM v038"
  Placement = pos=(21.5608,12.1142,0.754) rot=(0,0,1;0rad)
  shape: bbox 0.28 x 0.4 x 0.051 mm, 6 faces (baked)
FEATURE [Part::Feature] Part__Feature603  label="LSM9DS1TR_LGA-24_3X3P5X1_STM v039"
  Placement = pos=(21.5608,12.1142,0.754) rot=(0,0,1;0rad)
  shape: bbox 0.28 x 0.4 x 0.051 mm, 6 faces (baked)
FEATURE [Part::Feature] Part__Feature604  label="LSM9DS1TR_LGA-24_3X3P5X1_STM v040"
  Placement = pos=(21.5608,12.1142,0.754) rot=(0,0,1;0rad)
  shape: bbox 0.28 x 0.4 x 0.051 mm, 6 faces (baked)
FEATURE [Part::Feature] Part__Feature605  label="LSM9DS1TR_LGA-24_3X3P5X1_STM v041"
  Placement = pos=(21.5608,12.1142,0.754) rot=(0,0,1;0rad)
  shape: bbox 0.28 x 0.4 x 0.051 mm, 6 faces (baked)
FEATURE [Part::Feature] Part__Feature606  label="LSM9DS1TR_LGA-24_3X3P5X1_STM v042"
  Placement = pos=(21.5608,12.1142,0.754) rot=(0,0,1;0rad)
  shape: bbox 0.28 x 0.4 x 0.051 mm, 6 faces (baked)
FEATURE [Part::Feature] Part__Feature607  label="LSM9DS1TR_LGA-24_3X3P5X1_STM v043"
  Placement = pos=(21.5608,12.1142,0.754) rot=(0,0,1;0rad)
  shape: bbox 0.4 x 0.28 x 0.051 mm, 6 faces (baked)
FEATURE [Part::Feature] Part__Feature608  label="LSM9DS1TR_LGA-24_3X3P5X1_STM v044"
  Placement = pos=(21.5608,12.1142,0.754) rot=(0,0,1;0rad)
  shape: bbox 0.4 x 0.28 x 0.051 mm, 6 faces (baked)
FEATURE [Part::Feature] Part__Feature609  label="LSM9DS1TR_LGA-24_3X3P5X1_STM v045"
  Placement = pos=(21.5608,12.1142,0.754) rot=(0,0,1;0rad)
  shape: bbox 0.4 x 0.28 x 0.051 mm, 6 faces (baked)
FEATURE [Part::Feature] Part__Feature610  label="LSM9DS1TR_LGA-24_3X3P5X1_STM v046"
  Placement = pos=(21.5608,12.1142,0.754) rot=(0,0,1;0rad)
  shape: bbox 0.4 x 0.28 x 0.051 mm, 6 faces (baked)
FEATURE [Part::Feature] Part__Feature611  label="LSM9DS1TR_LGA-24_3X3P5X1_STM v047"
  Placement = pos=(21.5608,12.1142,0.754) rot=(0,0,1;0rad)
  shape: bbox 0.28 x 0.4 x 0.051 mm, 6 faces (baked)
FEATURE [Part::Feature] Part__Feature612  label="LSM9DS1TR_LGA-24_3X3P5X1_STM v048"
  Placement = pos=(21.5608,12.1142,0.754) rot=(0,0,1;0rad)
  shape: bbox 0.28 x 0.4 x 0.051 mm, 6 faces (baked)
FEATURE [Part::Feature] Part__Feature613  label="LSM9DS1TR_LGA-24_3X3P5X1_STM v049"
  Placement = pos=(21.5608,12.1142,0.754) rot=(0,0,1;0rad)
  shape: bbox 0.28 x 0.4 x 0.051 mm, 6 faces (baked)
FEATURE [Part::Feature] Part__Feature614  label="LSM9DS1TR_LGA-24_3X3P5X1_STM v050"
  Placement = pos=(21.5608,12.1142,0.754) rot=(0,0,1;0rad)
  shape: bbox 0.28 x 0.4 x 0.051 mm, 6 faces (baked)
FEATURE [Part::Feature] Part__Feature615  label="LSM9DS1TR_LGA-24_3X3P5X1_STM v051"
  Placement = pos=(21.5608,12.1142,0.754) rot=(0,0,1;0rad)
  shape: bbox 0.28 x 0.4 x 0.051 mm, 6 faces (baked)
FEATURE [Part::Feature] Part__Feature616  label="LSM9DS1TR_LGA-24_3X3P5X1_STM v052"
  Placement = pos=(21.5608,12.1142,0.754) rot=(0,0,1;0rad)
  shape: bbox 0.28 x 0.4 x 0.051 mm, 6 faces (baked)
FEATURE [Part::Feature] Part__Feature617  label="LSM9DS1TR_LGA-24_3X3P5X1_STM v053"
  Placement = pos=(21.5608,12.1142,0.754) rot=(0,0,1;0rad)
  shape: bbox 0.28 x 0.4 x 0.051 mm, 6 faces (baked)
FEATURE [Part::Feature] Part__Feature618  label="LSM9DS1TR_LGA-24_3X3P5X1_STM v054"
  Placement = pos=(21.5608,12.1142,0.754) rot=(0,0,1;0rad)
  shape: bbox 0.28 x 0.4 x 0.051 mm, 6 faces (baked)
FEATURE [App::Part] LSM9DS1TR_LGA_24_3X3P5X1_STM_v002  label="LSM9DS1TR_LGA-24_3X3P5X1_STM v028"
  Group = -> [Part__Feature593,Part__Feature594,Part__Feature595,Part__Feature596,Part__Feature597,Part__Feature598,Part__Feature599,Part__Feature600,Part__Feature601,Part__Feature602,Part__Feature603,Part__Feature604,Part__Feature605,Part__Feature606,Part__Feature607,Part__Feature608,Part__Feature609,Part__Feature610,Part__Feature611,Part__Feature612,Part__Feature613,Part__Feature614,Part__Feature615,+3 more]
  Origin = -> Origin111
FEATURE [Part::Feature] Part__Feature619  label="ZX62-AB-5PA (1)001"
  Placement = pos=(-4.98,1.125,5.465) rot=(0,0,1;0rad)
  shape: bbox 5.614 x 2.964 x 8.831 mm, 424 faces (baked)
FEATURE [Part::Feature] Part__Feature620  label="IoT_HSMG-C190 LED v003"
  Placement = pos=(1.9,3.1,0.805) rot=(1,0,0;1.5708rad)
  shape: bbox 1.6 x 0.8 x 0.8 mm, 18 faces (baked)
FEATURE [Part::Feature] Part__Feature621  label="IoT_MPM3610 Step-Down Module v002"
  Placement = pos=(15.675,5.1865,1.605) rot=(0,0.707107,0.707107;3.14159rad)
  shape: bbox 3.3 x 5.15 x 1.65 mm, 330 faces (baked)
FEATURE [Part::Feature] Part__Feature622  label="User Library-arduino_nano_reset core001"
  Placement = pos=(-8.89,0.805,-11.09) rot=(0,0,1;0rad)
  shape: bbox 5.251 x 2.159 x 2.809 mm, 76 faces (baked)
FEATURE [Part::Feature] Part__Feature623  label="User Library-arduino_nano_reset shell001"
  Placement = pos=(-8.89,2.455,-11.09) rot=(0,-1,0;1.5708rad)
  shape: bbox 4 x 1.65 x 3 mm, 71 faces (baked)
FEATURE [App::Part] IoT_Reser_Button_v002  label="IoT_Reser Button v002"
  Group = -> [Part__Feature622,Part__Feature623]
  Origin = -> Origin003
  Placement = pos=(0,0,0) rot=(0.57735,-0.57735,-0.57735;2.0944rad)
FEATURE [Part::Feature] Part__Feature624  label="RC0402FR-071KL RC0402N_YAG v109"
  Placement = pos=(4.8,3.0875,0.805) rot=(0,0,1;0rad)
  shape: bbox 0.458 x 0.494 x 0.697 mm, 6 faces (baked)
FEATURE [Part::Feature] Part__Feature625  label="RC0402FR-071KL RC0402N_YAG v110"
  Placement = pos=(4.8,3.0875,0.805) rot=(0,0,1;0rad)
  shape: bbox 0.304 x 0.508 x 0.711 mm, 6 faces (baked)
FEATURE [Part::Feature] Part__Feature626  label="RC0402FR-071KL RC0402N_YAG v111"
  Placement = pos=(4.8,3.0875,0.805) rot=(0,0,1;0rad)
  shape: bbox 0.304 x 0.508 x 0.711 mm, 6 faces (baked)
FEATURE [Part::Feature] Part__Feature627  label="RC0402FR-071KL RC0402N_YAG v112"
  Placement = pos=(6.25,4.4075,0.805) rot=(0,0,-1;1.5708rad)
  shape: bbox 0.494 x 0.458 x 0.697 mm, 6 faces (baked)
FEATURE [Part::Feature] Part__Feature628  label="RC0402FR-071KL RC0402N_YAG v113"
  Placement = pos=(6.25,4.4075,0.805) rot=(0,0,-1;1.5708rad)
  shape: bbox 0.508 x 0.304 x 0.711 mm, 6 faces (baked)
FEATURE [Part::Feature] Part__Feature629  label="RC0402FR-071KL RC0402N_YAG v114"
  Placement = pos=(6.25,4.4075,0.805) rot=(0,0,-1;1.5708rad)
  shape: bbox 0.508 x 0.304 x 0.711 mm, 6 faces (baked)
FEATURE [Part::Feature] Part__Feature630  label="RC0402FR-071KL RC0402N_YAG v115"
  Placement = pos=(9.8875,5.5375,0.805) rot=(0,0,1;0rad)
  shape: bbox 0.458 x 0.494 x 0.697 mm, 6 faces (baked)
FEATURE [Part::Feature] Part__Feature631  label="RC0402FR-071KL RC0402N_YAG v116"
  Placement = pos=(9.8875,5.5375,0.805) rot=(0,0,1;0rad)
  shape: bbox 0.304 x 0.508 x 0.711 mm, 6 faces (baked)
FEATURE [Part::Feature] Part__Feature632  label="RC0402FR-071KL RC0402N_YAG v117"
  Placement = pos=(9.8875,5.5375,0.805) rot=(0,0,1;0rad)
  shape: bbox 0.304 x 0.508 x 0.711 mm, 6 faces (baked)
FEATURE [Part::Feature] Part__Feature633  label="RC0402FR-071KL RC0402N_YAG v118"
  Placement = pos=(11.27,12.5,0.805) rot=(0,0,1;0rad)
  shape: bbox 0.458 x 0.494 x 0.697 mm, 6 faces (baked)
FEATURE [Part::Feature] Part__Feature634  label="RC0402FR-071KL RC0402N_YAG v119"
  Placement = pos=(11.27,12.5,0.805) rot=(0,0,1;0rad)
  shape: bbox 0.304 x 0.508 x 0.711 mm, 6 faces (baked)
FEATURE [Part::Feature] Part__Feature635  label="RC0402FR-071KL RC0402N_YAG v120"
  Placement = pos=(11.27,12.5,0.805) rot=(0,0,1;0rad)
  shape: bbox 0.304 x 0.508 x 0.711 mm, 6 faces (baked)
FEATURE [Part::Feature] Part__Feature636  label="RC0402FR-071KL RC0402N_YAG v121"
  Placement = pos=(5.4,14.7,0.805) rot=(0,0,1;0rad)
  shape: bbox 0.458 x 0.494 x 0.697 mm, 6 faces (baked)
FEATURE [Part::Feature] Part__Feature637  label="RC0402FR-071KL RC0402N_YAG v122"
  Placement = pos=(5.4,14.7,0.805) rot=(0,0,1;0rad)
  shape: bbox 0.304 x 0.508 x 0.711 mm, 6 faces (baked)
FEATURE [Part::Feature] Part__Feature638  label="RC0402FR-071KL RC0402N_YAG v123"
  Placement = pos=(5.4,14.7,0.805) rot=(0,0,1;0rad)
  shape: bbox 0.304 x 0.508 x 0.711 mm, 6 faces (baked)
FEATURE [Part::Feature] Part__Feature639  label="RC0402FR-071KL RC0402N_YAG v124"
  Placement = pos=(12.225,4.225,0.805) rot=(0,0,1;1.5708rad)
  shape: bbox 0.494 x 0.458 x 0.697 mm, 6 faces (baked)
FEATURE [Part::Feature] Part__Feature640  label="RC0402FR-071KL RC0402N_YAG v125"
  Placement = pos=(12.225,4.225,0.805) rot=(0,0,1;1.5708rad)
  shape: bbox 0.508 x 0.304 x 0.711 mm, 6 faces (baked)
FEATURE [Part::Feature] Part__Feature049  label="RC0402FR-071KL RC0402N_YAG v126"
  Placement = pos=(12.225,4.225,0.805) rot=(0,0,1;1.5708rad)
  shape: bbox 0.508 x 0.304 x 0.711 mm, 6 faces (baked)
FEATURE [Part::Feature] Part__Feature050  label="RC0402FR-071KL RC0402N_YAG v127"
  Placement = pos=(13.1875,4.2375,0.805) rot=(0,0,1;1.5708rad)
  shape: bbox 0.494 x 0.458 x 0.697 mm, 6 faces (baked)
FEATURE [Part::Feature] Part__Feature051  label="RC0402FR-071KL RC0402N_YAG v128"
  Placement = pos=(13.1875,4.2375,0.805) rot=(0,0,1;1.5708rad)
  shape: bbox 0.508 x 0.304 x 0.711 mm, 6 faces (baked)
FEATURE [Part::Feature] Part__Feature052  label="RC0402FR-071KL RC0402N_YAG v129"
  Placement = pos=(13.1875,4.2375,0.805) rot=(0,0,1;1.5708rad)
  shape: bbox 0.508 x 0.304 x 0.711 mm, 6 faces (baked)
FEATURE [Part::Feature] Part__Feature053  label="RC0402FR-071KL RC0402N_YAG v130"
  Placement = pos=(13.85,10.9,0.805) rot=(0,0,-1;1.5708rad)
  shape: bbox 0.494 x 0.458 x 0.697 mm, 6 faces (baked)
FEATURE [Part::Feature] Part__Feature054  label="RC0402FR-071KL RC0402N_YAG v131"
  Placement = pos=(13.85,10.9,0.805) rot=(0,0,-1;1.5708rad)
  shape: bbox 0.508 x 0.304 x 0.711 mm, 6 faces (baked)
FEATURE [Part::Feature] Part__Feature055  label="RC0402FR-071KL RC0402N_YAG v132"
  Placement = pos=(13.85,10.9,0.805) rot=(0,0,-1;1.5708rad)
  shape: bbox 0.508 x 0.304 x 0.711 mm, 6 faces (baked)
FEATURE [Part::Feature] Part__Feature641  label="RC0402FR-071KL RC0402N_YAG v133"
  Placement = pos=(14.8,10.9,0.805) rot=(0,0,-1;1.5708rad)
  shape: bbox 0.494 x 0.458 x 0.697 mm, 6 faces (baked)
FEATURE [Part::Feature] Part__Feature642  label="RC0402FR-071KL RC0402N_YAG v134"
  Placement = pos=(14.8,10.9,0.805) rot=(0,0,-1;1.5708rad)
  shape: bbox 0.508 x 0.304 x 0.711 mm, 6 faces (baked)
FEATURE [Part::Feature] Part__Feature058  label="RC0402FR-071KL RC0402N_YAG v135"
  Placement = pos=(14.8,10.9,0.805) rot=(0,0,-1;1.5708rad)
  shape: bbox 0.508 x 0.304 x 0.711 mm, 6 faces (baked)
FEATURE [Part::Feature] Part__Feature643  label="RC0402FR-071KL RC0402N_YAG v136"
  Placement = pos=(15.55,9.275,0.805) rot=(0,0,1;0rad)
  shape: bbox 0.458 x 0.494 x 0.697 mm, 6 faces (baked)
FEATURE [Part::Feature] Part__Feature644  label="RC0402FR-071KL RC0402N_YAG v137"
  Placement = pos=(15.55,9.275,0.805) rot=(0,0,1;0rad)
  shape: bbox 0.304 x 0.508 x 0.711 mm, 6 faces (baked)
FEATURE [Part::Feature] Part__Feature645  label="RC0402FR-071KL RC0402N_YAG v138"
  Placement = pos=(15.55,9.275,0.805) rot=(0,0,1;0rad)
  shape: bbox 0.304 x 0.508 x 0.711 mm, 6 faces (baked)
FEATURE [Part::Feature] Part__Feature646  label="RC0402FR-071KL RC0402N_YAG v139"
  Placement = pos=(16.525,12.75,0.805) rot=(0,0,-1;1.5708rad)
  shape: bbox 0.494 x 0.458 x 0.697 mm, 6 faces (baked)
FEATURE [Part::Feature] Part__Feature647  label="RC0402FR-071KL RC0402N_YAG v140"
  Placement = pos=(16.525,12.75,0.805) rot=(0,0,-1;1.5708rad)
  shape: bbox 0.508 x 0.304 x 0.711 mm, 6 faces (baked)
FEATURE [Part::Feature] Part__Feature648  label="RC0402FR-071KL RC0402N_YAG v141"
  Placement = pos=(16.525,12.75,0.805) rot=(0,0,-1;1.5708rad)
  shape: bbox 0.508 x 0.304 x 0.711 mm, 6 faces (baked)
FEATURE [Part::Feature] Part__Feature649  label="RC0402FR-071KL RC0402N_YAG v142"
  Placement = pos=(18,13.675,0.805) rot=(0,0,1;0rad)
  shape: bbox 0.458 x 0.494 x 0.697 mm, 6 faces (baked)
FEATURE [Part::Feature] Part__Feature650  label="RC0402FR-071KL RC0402N_YAG v143"
  Placement = pos=(18,13.675,0.805) rot=(0,0,1;0rad)
  shape: bbox 0.304 x 0.508 x 0.711 mm, 6 faces (baked)
FEATURE [Part::Feature] Part__Feature651  label="RC0402FR-071KL RC0402N_YAG v144"
  Placement = pos=(18,13.675,0.805) rot=(0,0,1;0rad)
  shape: bbox 0.304 x 0.508 x 0.711 mm, 6 faces (baked)
FEATURE [Part::Feature] Part__Feature652  label="RC0402FR-071KL RC0402N_YAG v145"
  Placement = pos=(18.475,9.775,0.805) rot=(0,0,1;0rad)
  shape: bbox 0.458 x 0.494 x 0.697 mm, 6 faces (baked)
FEATURE [Part::Feature] Part__Feature653  label="RC0402FR-071KL RC0402N_YAG v146"
  Placement = pos=(18.475,9.775,0.805) rot=(0,0,1;0rad)
  shape: bbox 0.304 x 0.508 x 0.711 mm, 6 faces (baked)
FEATURE [Part::Feature] Part__Feature654  label="RC0402FR-071KL RC0402N_YAG v147"
  Placement = pos=(18.475,9.775,0.805) rot=(0,0,1;0rad)
  shape: bbox 0.304 x 0.508 x 0.711 mm, 6 faces (baked)
FEATURE [Part::Feature] Part__Feature655  label="RC0402FR-071KL RC0402N_YAG v148"
  Placement = pos=(18.45,8.6,0.805) rot=(0,0,1;0rad)
  shape: bbox 0.458 x 0.494 x 0.697 mm, 6 faces (baked)
FEATURE [Part::Feature] Part__Feature656  label="RC0402FR-071KL RC0402N_YAG v149"
  Placement = pos=(18.45,8.6,0.805) rot=(0,0,1;0rad)
  shape: bbox 0.304 x 0.508 x 0.711 mm, 6 faces (baked)
FEATURE [Part::Feature] Part__Feature657  label="RC0402FR-071KL RC0402N_YAG v150"
  Placement = pos=(18.45,8.6,0.805) rot=(0,0,1;0rad)
  shape: bbox 0.304 x 0.508 x 0.711 mm, 6 faces (baked)
FEATURE [Part::Feature] Part__Feature658  label="RC0402FR-071KL RC0402N_YAG v151"
  Placement = pos=(21,6.275,0.805) rot=(0,0,1;0rad)
  shape: bbox 0.458 x 0.494 x 0.697 mm, 6 faces (baked)
FEATURE [Part::Feature] Part__Feature659  label="RC0402FR-071KL RC0402N_YAG v152"
  Placement = pos=(21,6.275,0.805) rot=(0,0,1;0rad)
  shape: bbox 0.304 x 0.508 x 0.711 mm, 6 faces (baked)
FEATURE [Part::Feature] Part__Feature660  label="RC0402FR-071KL RC0402N_YAG v153"
  Placement = pos=(21,6.275,0.805) rot=(0,0,1;0rad)
  shape: bbox 0.304 x 0.508 x 0.711 mm, 6 faces (baked)
FEATURE [Part::Feature] Part__Feature661  label="RC0402FR-071KL RC0402N_YAG v154"
  Placement = pos=(21,5.275,0.805) rot=(0,0,1;0rad)
  shape: bbox 0.458 x 0.494 x 0.697 mm, 6 faces (baked)
FEATURE [Part::Feature] Part__Feature662  label="RC0402FR-071KL RC0402N_YAG v155"
  Placement = pos=(21,5.275,0.805) rot=(0,0,1;0rad)
  shape: bbox 0.304 x 0.508 x 0.711 mm, 6 faces (baked)
FEATURE [Part::Feature] Part__Feature663  label="RC0402FR-071KL RC0402N_YAG v156"
  Placement = pos=(21,5.275,0.805) rot=(0,0,1;0rad)
  shape: bbox 0.304 x 0.508 x 0.711 mm, 6 faces (baked)
FEATURE [Part::Feature] Part__Feature664  label="RC0402FR-071KL RC0402N_YAG v157"
  Placement = pos=(20.405,3.8,0.805) rot=(0,0,-1;1.5708rad)
  shape: bbox 0.494 x 0.458 x 0.697 mm, 6 faces (baked)
FEATURE [Part::Feature] Part__Feature665  label="RC0402FR-071KL RC0402N_YAG v158"
  Placement = pos=(20.405,3.8,0.805) rot=(0,0,-1;1.5708rad)
  shape: bbox 0.508 x 0.304 x 0.711 mm, 6 faces (baked)
FEATURE [Part::Feature] Part__Feature666  label="RC0402FR-071KL RC0402N_YAG v159"
  Placement = pos=(20.405,3.8,0.805) rot=(0,0,-1;1.5708rad)
  shape: bbox 0.508 x 0.304 x 0.711 mm, 6 faces (baked)
FEATURE [Part::Feature] Part__Feature667  label="RC0402FR-071KL RC0402N_YAG v160"
  Placement = pos=(21.395,3.81264,0.805) rot=(0,0,-1;1.5708rad)
  shape: bbox 0.494 x 0.458 x 0.697 mm, 6 faces (baked)
FEATURE [Part::Feature] Part__Feature668  label="RC0402FR-071KL RC0402N_YAG v161"
  Placement = pos=(21.395,3.81264,0.805) rot=(0,0,-1;1.5708rad)
  shape: bbox 0.508 x 0.304 x 0.711 mm, 6 faces (baked)
FEATURE [Part::Feature] Part__Feature669  label="RC0402FR-071KL RC0402N_YAG v162"
  Placement = pos=(21.395,3.81264,0.805) rot=(0,0,-1;1.5708rad)
  shape: bbox 0.508 x 0.304 x 0.711 mm, 6 faces (baked)
FEATURE [Part::Feature] Part__Feature670  label="RC0402FR-071KL RC0402N_YAG v163"
  Placement = pos=(25.075,13.025,0.805) rot=(0,0,-1;1.5708rad)
  shape: bbox 0.494 x 0.458 x 0.697 mm, 6 faces (baked)
FEATURE [Part::Feature] Part__Feature671  label="RC0402FR-071KL RC0402N_YAG v164"
  Placement = pos=(25.075,13.025,0.805) rot=(0,0,-1;1.5708rad)
  shape: bbox 0.508 x 0.304 x 0.711 mm, 6 faces (baked)
FEATURE [Part::Feature] Part__Feature672  label="RC0402FR-071KL RC0402N_YAG v165"
  Placement = pos=(25.075,13.025,0.805) rot=(0,0,-1;1.5708rad)
  shape: bbox 0.508 x 0.304 x 0.711 mm, 6 faces (baked)
FEATURE [Part::Feature] Part__Feature673  label="RC0402FR-071KL RC0402N_YAG v166"
  Placement = pos=(26.7,14.2,0.805) rot=(0,0,1;0rad)
  shape: bbox 0.458 x 0.494 x 0.697 mm, 6 faces (baked)
FEATURE [Part::Feature] Part__Feature674  label="RC0402FR-071KL RC0402N_YAG v167"
  Placement = pos=(26.7,14.2,0.805) rot=(0,0,1;0rad)
  shape: bbox 0.304 x 0.508 x 0.711 mm, 6 faces (baked)
FEATURE [Part::Feature] Part__Feature675  label="RC0402FR-071KL RC0402N_YAG v168"
  Placement = pos=(26.7,14.2,0.805) rot=(0,0,1;0rad)
  shape: bbox 0.304 x 0.508 x 0.711 mm, 6 faces (baked)
FEATURE [Part::Feature] Part__Feature676  label="RC0402FR-071KL RC0402N_YAG v169"
  Placement = pos=(39.625,3.32,0.805) rot=(0,0,1;0rad)
  shape: bbox 0.458 x 0.494 x 0.697 mm, 6 faces (baked)
FEATURE [Part::Feature] Part__Feature677  label="RC0402FR-071KL RC0402N_YAG v170"
  Placement = pos=(39.625,3.32,0.805) rot=(0,0,1;0rad)
  shape: bbox 0.304 x 0.508 x 0.711 mm, 6 faces (baked)
FEATURE [Part::Feature] Part__Feature678  label="RC0402FR-071KL RC0402N_YAG v171"
  Placement = pos=(39.625,3.32,0.805) rot=(0,0,1;0rad)
  shape: bbox 0.304 x 0.508 x 0.711 mm, 6 faces (baked)
FEATURE [Part::Feature] Part__Feature679  label="RC0402FR-071KL RC0402N_YAG v172"
  Placement = pos=(37.675,3.32,0.805) rot=(0,0,1;0rad)
  shape: bbox 0.458 x 0.494 x 0.697 mm, 6 faces (baked)
FEATURE [Part::Feature] Part__Feature680  label="RC0402FR-071KL RC0402N_YAG v173"
  Placement = pos=(37.675,3.32,0.805) rot=(0,0,1;0rad)
  shape: bbox 0.304 x 0.508 x 0.711 mm, 6 faces (baked)
FEATURE [Part::Feature] Part__Feature681  label="RC0402FR-071KL RC0402N_YAG v174"
  Placement = pos=(37.675,3.32,0.805) rot=(0,0,1;0rad)
  shape: bbox 0.304 x 0.508 x 0.711 mm, 6 faces (baked)
FEATURE [Part::Feature] Part__Feature682  label="RC0402FR-071KL RC0402N_YAG v175"
  Placement = pos=(35.7,3.3125,0.805) rot=(0,0,1;0rad)
  shape: bbox 0.458 x 0.494 x 0.697 mm, 6 faces (baked)
FEATURE [Part::Feature] Part__Feature683  label="RC0402FR-071KL RC0402N_YAG v176"
  Placement = pos=(35.7,3.3125,0.805) rot=(0,0,1;0rad)
  shape: bbox 0.304 x 0.508 x 0.711 mm, 6 faces (baked)
FEATURE [Part::Feature] Part__Feature684  label="RC0402FR-071KL RC0402N_YAG v177"
  Placement = pos=(35.7,3.3125,0.805) rot=(0,0,1;0rad)
  shape: bbox 0.304 x 0.508 x 0.711 mm, 6 faces (baked)
FEATURE [Part::Feature] Part__Feature685  label="RC0402FR-071KL RC0402N_YAG v178"
  Placement = pos=(25.4125,3.8125,0.805) rot=(0,0,-1;1.5708rad)
  shape: bbox 0.494 x 0.458 x 0.697 mm, 6 faces (baked)
FEATURE [Part::Feature] Part__Feature686  label="RC0402FR-071KL RC0402N_YAG v179"
  Placement = pos=(25.4125,3.8125,0.805) rot=(0,0,-1;1.5708rad)
  shape: bbox 0.508 x 0.304 x 0.711 mm, 6 faces (baked)
FEATURE [Part::Feature] Part__Feature687  label="RC0402FR-071KL RC0402N_YAG v180"
  Placement = pos=(25.4125,3.8125,0.805) rot=(0,0,-1;1.5708rad)
  shape: bbox 0.508 x 0.304 x 0.711 mm, 6 faces (baked)
FEATURE [Part::Feature] Part__Feature688  label="RC0402FR-071KL RC0402N_YAG v181"
  Placement = pos=(26.8,10.7,0.805) rot=(0,0,1;0rad)
  shape: bbox 0.458 x 0.494 x 0.697 mm, 6 faces (baked)
FEATURE [Part::Feature] Part__Feature689  label="RC0402FR-071KL RC0402N_YAG v182"
  Placement = pos=(26.8,10.7,0.805) rot=(0,0,1;0rad)
  shape: bbox 0.304 x 0.508 x 0.711 mm, 6 faces (baked)
FEATURE [Part::Feature] Part__Feature690  label="RC0402FR-071KL RC0402N_YAG v183"
  Placement = pos=(26.8,10.7,0.805) rot=(0,0,1;0rad)
  shape: bbox 0.304 x 0.508 x 0.711 mm, 6 faces (baked)
FEATURE [Part::Feature] Part__Feature691  label="RC0402FR-071KL RC0402N_YAG v184"
  Placement = pos=(19.9,14.625,0.805) rot=(0,0,1;0rad)
  shape: bbox 0.458 x 0.494 x 0.697 mm, 6 faces (baked)
FEATURE [Part::Feature] Part__Feature692  label="RC0402FR-071KL RC0402N_YAG v185"
  Placement = pos=(19.9,14.625,0.805) rot=(0,0,1;0rad)
  shape: bbox 0.304 x 0.508 x 0.711 mm, 6 faces (baked)
FEATURE [Part::Feature] Part__Feature693  label="RC0402FR-071KL RC0402N_YAG v186"
  Placement = pos=(19.9,14.625,0.805) rot=(0,0,1;0rad)
  shape: bbox 0.304 x 0.508 x 0.711 mm, 6 faces (baked)
FEATURE [Part::Feature] Part__Feature694  label="RC0402FR-071KL RC0402N_YAG v187"
  Placement = pos=(22.2,14.625,0.805) rot=(0,0,1;0rad)
  shape: bbox 0.458 x 0.494 x 0.697 mm, 6 faces (baked)
FEATURE [Part::Feature] Part__Feature695  label="RC0402FR-071KL RC0402N_YAG v188"
  Placement = pos=(22.2,14.625,0.805) rot=(0,0,1;0rad)
  shape: bbox 0.304 x 0.508 x 0.711 mm, 6 faces (baked)
FEATURE [Part::Feature] Part__Feature696  label="RC0402FR-071KL RC0402N_YAG v189"
  Placement = pos=(22.2,14.625,0.805) rot=(0,0,1;0rad)
  shape: bbox 0.304 x 0.508 x 0.711 mm, 6 faces (baked)
FEATURE [Part::Feature] Part__Feature697  label="IoT_HSMG-C190 LED v004"
  Placement = pos=(1.9,14.7,0.805) rot=(1,0,0;1.5708rad)
  shape: bbox 1.6 x 0.8 x 0.8 mm, 18 faces (baked)
FEATURE [Part::Feature] Part__Feature698  label="BLM18EG101TN1D v006"
  Placement = pos=(33.0875,2.8875,1.20467) rot=(0,0,1;0rad)
  shape: bbox 0.4 x 0.65 x 0.8 mm, 18 faces (baked)
FEATURE [Part::Feature] Part__Feature699  label="BLM18EG101TN1D v007"
  Placement = pos=(33.0875,2.8875,1.20467) rot=(0,0,1;0rad)
  shape: bbox 0.4 x 0.65 x 0.8 mm, 18 faces (baked)
FEATURE [Part::Feature] Part__Feature700  label="BLM18EG101TN1D v008"
  Placement = pos=(33.0875,2.8875,1.20467) rot=(0,0,1;0rad)
  shape: bbox 0.8 x 0.6233 x 0.7733 mm, 10 faces (baked)
FEATURE [App::Part] BLM18EG101TN1D_v002  label="BLM18EG101TN1D v005"
  Group = -> [Part__Feature698,Part__Feature699,Part__Feature700]
  Origin = -> Origin135
FEATURE [Part::Feature] Part__Feature701  label="C0805C472KDRACTU v016"
  Placement = pos=(14.1625,13,0.805333) rot=(1,0,0;1.5708rad)
  shape: bbox 0.5 x 1.25 x 1.4 mm, 18 faces (baked)
FEATURE [Part::Feature] Part__Feature702  label="C0805C472KDRACTU v017"
  Placement = pos=(14.1625,13,0.805333) rot=(1,0,0;1.5708rad)
  shape: bbox 0.5 x 1.25 x 1.4 mm, 18 faces (baked)
FEATURE [Part::Feature] Part__Feature703  label="C0805C472KDRACTU v018"
  Placement = pos=(14.1625,13,0.805333) rot=(1,0,0;1.5708rad)
  shape: bbox 1 x 1.217 x 1.367 mm, 10 faces (baked)
FEATURE [App::Part] C0805C472KDRACTU_v006  label="C0805C472KDRACTU v015"
  Group = -> [Part__Feature701,Part__Feature702,Part__Feature703]
  Origin = -> Origin136
FEATURE [Part::Feature] Part__Feature704  label="C0805C472KDRACTU v019"
  Placement = pos=(18.7875,6.0875,0.805333) rot=(0.57735,-0.57735,-0.57735;2.0944rad)
  shape: bbox 1.25 x 0.5 x 1.4 mm, 18 faces (baked)
FEATURE [Part::Feature] Part__Feature705  label="C0805C472KDRACTU v020"
  Placement = pos=(18.7875,6.0875,0.805333) rot=(0.57735,-0.57735,-0.57735;2.0944rad)
  shape: bbox 1.25 x 0.5 x 1.4 mm, 18 faces (baked)
FEATURE [Part::Feature] Part__Feature706  label="C0805C472KDRACTU v021"
  Placement = pos=(18.7875,6.0875,0.805333) rot=(0.57735,-0.57735,-0.57735;2.0944rad)
  shape: bbox 1.217 x 1 x 1.367 mm, 10 faces (baked)
FEATURE [App::Part] C0805C472KDRACTU_v004  label="C0805C472KDRACTU v013"
  Group = -> [Part__Feature704,Part__Feature705,Part__Feature706]
  Origin = -> Origin137
FEATURE [Part::Feature] Part__Feature707  label="PMEG6020AELRX v007"
  Placement = pos=(7.9,12.95,0.805) rot=(1,0,0;1.5708rad)
  shape: bbox 2.6 x 1.7 x 1.1 mm, 15 faces (baked)
FEATURE [Part::Feature] Part__Feature708  label="PMEG6020AELRX v008"
  Placement = pos=(7.9,12.95,0.805) rot=(1,0,0;1.5708rad)
  shape: bbox 0.55 x 1.569 x 0.05 mm, 6 faces (baked)
FEATURE [Part::Feature] Part__Feature709  label="PMEG6020AELRX v009"
  Placement = pos=(7.9,12.95,0.805) rot=(1,0,0;1.5708rad)
  shape: bbox 0.4612 x 0.9 x 0.16 mm, 6 faces (baked)
FEATURE [Part::Feature] Part__Feature710  label="PMEG6020AELRX v010"
  Placement = pos=(7.9,12.95,0.805) rot=(1,0,0;1.5708rad)
  shape: bbox 0.4612 x 0.9 x 0.16 mm, 6 faces (baked)
FEATURE [App::Part] PMEG6020AELRX_v002  label="PMEG6020AELRX v006"
  Group = -> [Part__Feature707,Part__Feature708,Part__Feature709,Part__Feature710]
  Origin = -> Origin138
FEATURE [Part::Feature] Part__Feature711  label="C0805C472KDRACTU v022"
  Placement = pos=(6.8675,6.425,0.805333) rot=(1,0,0;1.5708rad)
  shape: bbox 0.5 x 1.25 x 1.4 mm, 18 faces (baked)
FEATURE [Part::Feature] Part__Feature712  label="C0805C472KDRACTU v023"
  Placement = pos=(6.8675,6.425,0.805333) rot=(1,0,0;1.5708rad)
  shape: bbox 0.5 x 1.25 x 1.4 mm, 18 faces (baked)
FEATURE [Part::Feature] Part__Feature713  label="C0805C472KDRACTU v024"
  Placement = pos=(6.8675,6.425,0.805333) rot=(1,0,0;1.5708rad)
  shape: bbox 1 x 1.217 x 1.367 mm, 10 faces (baked)
FEATURE [App::Part] C0805C472KDRACTU_v005  label="C0805C472KDRACTU v014"
  Group = -> [Part__Feature711,Part__Feature712,Part__Feature713]
  Origin = -> Origin139
FEATURE [Part::Feature] Part__Feature714  label="IoT_PRTR5V0U2X Protection Diode v002"
  Placement = pos=(7.23,9.3,1.455) rot=(1,0,0;1.5708rad)
  shape: bbox 3 x 2.5 x 1.1 mm, 139 faces (baked)
FEATURE [Part::Feature] Part__Feature715  label="NINA-B306-00B-00--3DModel-STEP-56544 v091"
  Placement = pos=(35.642,8.89,0.805) rot=(0.57735,0.57735,0.57735;2.0944rad)
  shape: bbox 0.7 x 0.7 x 0.05 mm, 6 faces (baked)
FEATURE [Part::Feature] Part__Feature716  label="NINA-B306-00B-00--3DModel-STEP-56544 v092"
  Placement = pos=(35.642,8.89,0.805) rot=(0.57735,0.57735,0.57735;2.0944rad)
  shape: bbox 1.15 x 0.7 x 0.05 mm, 6 faces (baked)
FEATURE [Part::Feature] Part__Feature717  label="NINA-B306-00B-00--3DModel-STEP-56544 v093"
  Placement = pos=(35.642,8.89,0.805) rot=(0.57735,0.57735,0.57735;2.0944rad)
  shape: bbox 0.7 x 1.15 x 0.05 mm, 6 faces (baked)
FEATURE [Part::Feature] Part__Feature718  label="NINA-B306-00B-00--3DModel-STEP-56544 v094"
  Placement = pos=(35.642,8.89,0.805) rot=(0.57735,0.57735,0.57735;2.0944rad)
  shape: bbox 1.15 x 0.7 x 0.05 mm, 6 faces (baked)
FEATURE [Part::Feature] Part__Feature719  label="NINA-B306-00B-00--3DModel-STEP-56544 v095"
  Placement = pos=(35.642,8.89,0.805) rot=(0.57735,0.57735,0.57735;2.0944rad)
  shape: bbox 0.7 x 0.7 x 0.05 mm, 6 faces (baked)
FEATURE [Part::Feature] Part__Feature720  label="NINA-B306-00B-00--3DModel-STEP-56544 v096"
  Placement = pos=(35.642,8.89,0.805) rot=(0.57735,0.57735,0.57735;2.0944rad)
  shape: bbox 0.7 x 0.7 x 0.05 mm, 6 faces (baked)
FEATURE [Part::Feature] Part__Feature721  label="NINA-B306-00B-00--3DModel-STEP-56544 v097"
  Placement = pos=(35.642,8.89,0.805) rot=(0.57735,0.57735,0.57735;2.0944rad)
  shape: bbox 0.325 x 0.165 x 0.25 mm, 6 faces (baked)
FEATURE [Part::Feature] Part__Feature722  label="NINA-B306-00B-00--3DModel-STEP-56544 v098"
  Placement = pos=(35.642,8.89,0.805) rot=(0.57735,0.57735,0.57735;2.0944rad)
  shape: bbox 0.7 x 1.15 x 0.05 mm, 6 faces (baked)
FEATURE [Part::Feature] Part__Feature723  label="NINA-B306-00B-00--3DModel-STEP-56544 v099"
  Placement = pos=(35.642,8.89,0.805) rot=(0.57735,0.57735,0.57735;2.0944rad)
  shape: bbox 0.325 x 0.295 x 0.25 mm, 6 faces (baked)
FEATURE [Part::Feature] Part__Feature724  label="NINA-B306-00B-00--3DModel-STEP-56544 v100"
  Placement = pos=(35.642,8.89,0.805) rot=(0.57735,0.57735,0.57735;2.0944rad)
  shape: bbox 0.7 x 0.7 x 0.05 mm, 6 faces (baked)
FEATURE [Part::Feature] Part__Feature725  label="NINA-B306-00B-00--3DModel-STEP-56544 v101"
  Placement = pos=(35.642,8.89,0.805) rot=(0.57735,0.57735,0.57735;2.0944rad)
  shape: bbox 0.7 x 0.7 x 0.05 mm, 6 faces (baked)
FEATURE [Part::Feature] Part__Feature726  label="NINA-B306-00B-00--3DModel-STEP-56544 v102"
  Placement = pos=(35.642,8.89,0.805) rot=(0.57735,0.57735,0.57735;2.0944rad)
  shape: bbox 0.7 x 1.15 x 0.05 mm, 6 faces (baked)
FEATURE [Part::Feature] Part__Feature727  label="NINA-B306-00B-00--3DModel-STEP-56544 v103"
  Placement = pos=(35.642,8.89,0.805) rot=(0.57735,0.57735,0.57735;2.0944rad)
  shape: bbox 0.325 x 0.165 x 0.25 mm, 6 faces (baked)
FEATURE [Part::Feature] Part__Feature728  label="NINA-B306-00B-00--3DModel-STEP-56544 v104"
  Placement = pos=(35.642,8.89,0.805) rot=(0.57735,0.57735,0.57735;2.0944rad)
  shape: bbox 0.7 x 0.7 x 0.05 mm, 6 faces (baked)
FEATURE [Part::Feature] Part__Feature729  label="NINA-B306-00B-00--3DModel-STEP-56544 v105"
  Placement = pos=(35.642,8.89,0.805) rot=(0.57735,0.57735,0.57735;2.0944rad)
  shape: bbox 0.7 x 0.7 x 0.05 mm, 6 faces (baked)
FEATURE [Part::Feature] Part__Feature730  label="NINA-B306-00B-00--3DModel-STEP-56544 v106"
  Placement = pos=(35.642,8.89,0.805) rot=(0.57735,0.57735,0.57735;2.0944rad)
  shape: bbox 0.7 x 0.7 x 0.05 mm, 6 faces (baked)
FEATURE [Part::Feature] Part__Feature731  label="NINA-B306-00B-00--3DModel-STEP-56544 v107"
  Placement = pos=(35.642,8.89,0.805) rot=(0.57735,0.57735,0.57735;2.0944rad)
  shape: bbox 0.7 x 0.7 x 0.05 mm, 6 faces (baked)
FEATURE [Part::Feature] Part__Feature732  label="NINA-B306-00B-00--3DModel-STEP-56544 v108"
  Placement = pos=(35.642,8.89,0.805) rot=(0.57735,0.57735,0.57735;2.0944rad)
  shape: bbox 15 x 10 x 0.9 mm, 361 faces (baked)
FEATURE [Part::Feature] Part__Feature733  label="NINA-B306-00B-00--3DModel-STEP-56544 v109"
  Placement = pos=(35.642,8.89,0.805) rot=(0.57735,0.57735,0.57735;2.0944rad)
  shape: bbox 0.7 x 1.15 x 0.05 mm, 6 faces (baked)
FEATURE [Part::Feature] Part__Feature734  label="NINA-B306-00B-00--3DModel-STEP-56544 v110"
  Placement = pos=(35.642,8.89,0.805) rot=(0.57735,0.57735,0.57735;2.0944rad)
  shape: bbox 1.15 x 0.7 x 0.05 mm, 6 faces (baked)
FEATURE [Part::Feature] Part__Feature735  label="NINA-B306-00B-00--3DModel-STEP-56544 v111"
  Placement = pos=(35.642,8.89,0.805) rot=(0.57735,0.57735,0.57735;2.0944rad)
  shape: bbox 0.7 x 1.15 x 0.05 mm, 6 faces (baked)
FEATURE [Part::Feature] Part__Feature736  label="NINA-B306-00B-00--3DModel-STEP-56544 v112"
  Placement = pos=(35.642,8.89,0.805) rot=(0.57735,0.57735,0.57735;2.0944rad)
  shape: bbox 1.15 x 0.7 x 0.05 mm, 6 faces (baked)
FEATURE [Part::Feature] Part__Feature737  label="NINA-B306-00B-00--3DModel-STEP-56544 v113"
  Placement = pos=(35.642,8.89,0.805) rot=(0.57735,0.57735,0.57735;2.0944rad)
  shape: bbox 0.7 x 0.7 x 0.05 mm, 6 faces (baked)
FEATURE [Part::Feature] Part__Feature738  label="NINA-B306-00B-00--3DModel-STEP-56544 v114"
  Placement = pos=(35.642,8.89,0.805) rot=(0.57735,0.57735,0.57735;2.0944rad)
  shape: bbox 0.7 x 0.7 x 0.05 mm, 6 faces (baked)
FEATURE [Part::Feature] Part__Feature739  label="NINA-B306-00B-00--3DModel-STEP-56544 v115"
  Placement = pos=(35.642,8.89,0.805) rot=(0.57735,0.57735,0.57735;2.0944rad)
  shape: bbox 0.165 x 0.325 x 0.25 mm, 6 faces (baked)
FEATURE [Part::Feature] Part__Feature740  label="NINA-B306-00B-00--3DModel-STEP-56544 v116"
  Placement = pos=(35.642,8.89,0.805) rot=(0.57735,0.57735,0.57735;2.0944rad)
  shape: bbox 0.7 x 0.7 x 0.05 mm, 6 faces (baked)
FEATURE [Part::Feature] Part__Feature741  label="NINA-B306-00B-00--3DModel-STEP-56544 v117"
  Placement = pos=(35.642,8.89,0.805) rot=(0.57735,0.57735,0.57735;2.0944rad)
  shape: bbox 0.295 x 0.325 x 0.25 mm, 6 faces (baked)
FEATURE [Part::Feature] Part__Feature742  label="NINA-B306-00B-00--3DModel-STEP-56544 v118"
  Placement = pos=(35.642,8.89,0.805) rot=(0.57735,0.57735,0.57735;2.0944rad)
  shape: bbox 0.7 x 1.15 x 0.05 mm, 6 faces (baked)
FEATURE [Part::Feature] Part__Feature743  label="NINA-B306-00B-00--3DModel-STEP-56544 v119"
  Placement = pos=(35.642,8.89,0.805) rot=(0.57735,0.57735,0.57735;2.0944rad)
  shape: bbox 0.165 x 0.325 x 0.25 mm, 6 faces (baked)
FEATURE [Part::Feature] Part__Feature744  label="NINA-B306-00B-00--3DModel-STEP-56544 v120"
  Placement = pos=(35.642,8.89,0.805) rot=(0.57735,0.57735,0.57735;2.0944rad)
  shape: bbox 0.7 x 0.7 x 0.05 mm, 6 faces (baked)
FEATURE [Part::Feature] Part__Feature745  label="NINA-B306-00B-00--3DModel-STEP-56544 v121"
  Placement = pos=(35.642,8.89,0.805) rot=(0.57735,0.57735,0.57735;2.0944rad)
  shape: bbox 0.7 x 1.15 x 0.05 mm, 6 faces (baked)
FEATURE [Part::Feature] Part__Feature746  label="NINA-B306-00B-00--3DModel-STEP-56544 v122"
  Placement = pos=(35.642,8.89,0.805) rot=(0.57735,0.57735,0.57735;2.0944rad)
  shape: bbox 0.7 x 0.7 x 0.05 mm, 6 faces (baked)
FEATURE [Part::Feature] Part__Feature747  label="NINA-B306-00B-00--3DModel-STEP-56544 v123"
  Placement = pos=(35.642,8.89,0.805) rot=(0.57735,0.57735,0.57735;2.0944rad)
  shape: bbox 0.7 x 0.7 x 0.05 mm, 6 faces (baked)
FEATURE [Part::Feature] Part__Feature748  label="NINA-B306-00B-00--3DModel-STEP-56544 v124"
  Placement = pos=(35.642,8.89,0.805) rot=(0.57735,0.57735,0.57735;2.0944rad)
  shape: bbox 0.7 x 0.7 x 0.05 mm, 6 faces (baked)
FEATURE [Part::Feature] Part__Feature749  label="NINA-B306-00B-00--3DModel-STEP-56544 v125"
  Placement = pos=(35.642,8.89,0.805) rot=(0.57735,0.57735,0.57735;2.0944rad)
  shape: bbox 0.7 x 1.15 x 0.05 mm, 6 faces (baked)
FEATURE [Part::Feature] Part__Feature750  label="NINA-B306-00B-00--3DModel-STEP-56544 v126"
  Placement = pos=(35.642,8.89,0.805) rot=(0.57735,0.57735,0.57735;2.0944rad)
  shape: bbox 0.7 x 1.15 x 0.05 mm, 6 faces (baked)
FEATURE [Part::Feature] Part__Feature751  label="NINA-B306-00B-00--3DModel-STEP-56544 v127"
  Placement = pos=(35.642,8.89,0.805) rot=(0.57735,0.57735,0.57735;2.0944rad)
  shape: bbox 1.15 x 0.7 x 0.05 mm, 6 faces (baked)
FEATURE [Part::Feature] Part__Feature752  label="NINA-B306-00B-00--3DModel-STEP-56544 v128"
  Placement = pos=(35.642,8.89,0.805) rot=(0.57735,0.57735,0.57735;2.0944rad)
  shape: bbox 0.7 x 0.7 x 0.05 mm, 6 faces (baked)
FEATURE [Part::Feature] Part__Feature753  label="NINA-B306-00B-00--3DModel-STEP-56544 v129"
  Placement = pos=(35.642,8.89,0.805) rot=(0.57735,0.57735,0.57735;2.0944rad)
  shape: bbox 1.15 x 0.7 x 0.05 mm, 6 faces (baked)
FEATURE [Part::Feature] Part__Feature754  label="NINA-B306-00B-00--3DModel-STEP-56544 v130"
  Placement = pos=(35.642,8.89,0.805) rot=(0.57735,0.57735,0.57735;2.0944rad)
  shape: bbox 0.7 x 0.7 x 0.05 mm, 6 faces (baked)
FEATURE [Part::Feature] Part__Feature755  label="NINA-B306-00B-00--3DModel-STEP-56544 v131"
  Placement = pos=(35.642,8.89,0.805) rot=(0.57735,0.57735,0.57735;2.0944rad)
  shape: bbox 0.7 x 0.7 x 0.05 mm, 6 faces (baked)
FEATURE [Part::Feature] Part__Feature756  label="NINA-B306-00B-00--3DModel-STEP-56544 v132"
  Placement = pos=(35.642,8.89,0.805) rot=(0.57735,0.57735,0.57735;2.0944rad)
  shape: bbox 0.325 x 0.165 x 0.25 mm, 6 faces (baked)
FEATURE [Part::Feature] Part__Feature757  label="NINA-B306-00B-00--3DModel-STEP-56544 v133"
  Placement = pos=(35.642,8.89,0.805) rot=(0.57735,0.57735,0.57735;2.0944rad)
  shape: bbox 0.7 x 0.7 x 0.05 mm, 6 faces (baked)
FEATURE [Part::Feature] Part__Feature758  label="NINA-B306-00B-00--3DModel-STEP-56544 v134"
  Placement = pos=(35.642,8.89,0.805) rot=(0.57735,0.57735,0.57735;2.0944rad)
  shape: bbox 0.325 x 0.295 x 0.25 mm, 6 faces (baked)
FEATURE [Part::Feature] Part__Feature759  label="NINA-B306-00B-00--3DModel-STEP-56544 v135"
  Placement = pos=(35.642,8.89,0.805) rot=(0.57735,0.57735,0.57735;2.0944rad)
  shape: bbox 0.7 x 1.15 x 0.05 mm, 6 faces (baked)
FEATURE [Part::Feature] Part__Feature760  label="NINA-B306-00B-00--3DModel-STEP-56544 v136"
  Placement = pos=(35.642,8.89,0.805) rot=(0.57735,0.57735,0.57735;2.0944rad)
  shape: bbox 0.325 x 0.165 x 0.25 mm, 6 faces (baked)
FEATURE [Part::Feature] Part__Feature761  label="NINA-B306-00B-00--3DModel-STEP-56544 v137"
  Placement = pos=(35.642,8.89,0.805) rot=(0.57735,0.57735,0.57735;2.0944rad)
  shape: bbox 0.7 x 0.7 x 0.05 mm, 6 faces (baked)
FEATURE [Part::Feature] Part__Feature762  label="NINA-B306-00B-00--3DModel-STEP-56544 v138"
  Placement = pos=(35.642,8.89,0.805) rot=(0.57735,0.57735,0.57735;2.0944rad)
  shape: bbox 0.7 x 1.15 x 0.05 mm, 6 faces (baked)
FEATURE [Part::Feature] Part__Feature763  label="NINA-B306-00B-00--3DModel-STEP-56544 v139"
  Placement = pos=(35.642,8.89,0.805) rot=(0.57735,0.57735,0.57735;2.0944rad)
  shape: bbox 0.7 x 0.7 x 0.05 mm, 6 faces (baked)
FEATURE [Part::Feature] Part__Feature764  label="NINA-B306-00B-00--3DModel-STEP-56544 v140"
  Placement = pos=(35.642,8.89,0.805) rot=(0.57735,0.57735,0.57735;2.0944rad)
  shape: bbox 0.7 x 0.7 x 0.05 mm, 6 faces (baked)
FEATURE [Part::Feature] Part__Feature765  label="NINA-B306-00B-00--3DModel-STEP-56544 v141"
  Placement = pos=(35.642,8.89,0.805) rot=(0.57735,0.57735,0.57735;2.0944rad)
  shape: bbox 0.7 x 0.7 x 0.05 mm, 6 faces (baked)
FEATURE [Part::Feature] Part__Feature766  label="NINA-B306-00B-00--3DModel-STEP-56544 v142"
  Placement = pos=(35.642,8.89,0.805) rot=(0.57735,0.57735,0.57735;2.0944rad)
  shape: bbox 0.7 x 1.15 x 0.05 mm, 6 faces (baked)
FEATURE [Part::Feature] Part__Feature767  label="NINA-B306-00B-00--3DModel-STEP-56544 v143"
  Placement = pos=(35.642,8.89,0.805) rot=(0.57735,0.57735,0.57735;2.0944rad)
  shape: bbox 0.7 x 1.15 x 0.05 mm, 6 faces (baked)
FEATURE [Part::Feature] Part__Feature768  label="NINA-B306-00B-00--3DModel-STEP-56544 v144"
  Placement = pos=(35.642,8.89,0.805) rot=(0.57735,0.57735,0.57735;2.0944rad)
  shape: bbox 1.15 x 0.7 x 0.05 mm, 6 faces (baked)
FEATURE [Part::Feature] Part__Feature769  label="NINA-B306-00B-00--3DModel-STEP-56544 v145"
  Placement = pos=(35.642,8.89,0.805) rot=(0.57735,0.57735,0.57735;2.0944rad)
  shape: bbox 0.7 x 0.7 x 0.05 mm, 6 faces (baked)
FEATURE [Part::Feature] Part__Feature770  label="NINA-B306-00B-00--3DModel-STEP-56544 v146"
  Placement = pos=(35.642,8.89,0.805) rot=(0.57735,0.57735,0.57735;2.0944rad)
  shape: bbox 0.7 x 0.7 x 0.05 mm, 6 faces (baked)
FEATURE [Part::Feature] Part__Feature771  label="NINA-B306-00B-00--3DModel-STEP-56544 v147"
  Placement = pos=(35.642,8.89,0.805) rot=(0.57735,0.57735,0.57735;2.0944rad)
  shape: bbox 0.7 x 1.15 x 0.05 mm, 6 faces (baked)
FEATURE [Part::Feature] Part__Feature772  label="NINA-B306-00B-00--3DModel-STEP-56544 v148"
  Placement = pos=(35.642,8.89,0.805) rot=(0.57735,0.57735,0.57735;2.0944rad)
  shape: bbox 0.7 x 0.7 x 0.05 mm, 6 faces (baked)
FEATURE [Part::Feature] Part__Feature773  label="NINA-B306-00B-00--3DModel-STEP-56544 v149"
  Placement = pos=(35.642,8.89,0.805) rot=(0.57735,0.57735,0.57735;2.0944rad)
  shape: bbox 0.325 x 0.165 x 0.25 mm, 6 faces (baked)
FEATURE [Part::Feature] Part__Feature774  label="NINA-B306-00B-00--3DModel-STEP-56544 v150"
  Placement = pos=(35.642,8.89,0.805) rot=(0.57735,0.57735,0.57735;2.0944rad)
  shape: bbox 0.7 x 1.15 x 0.05 mm, 6 faces (baked)
FEATURE [Part::Feature] Part__Feature775  label="NINA-B306-00B-00--3DModel-STEP-56544 v151"
  Placement = pos=(35.642,8.89,0.805) rot=(0.57735,0.57735,0.57735;2.0944rad)
  shape: bbox 0.325 x 0.295 x 0.25 mm, 6 faces (baked)
FEATURE [Part::Feature] Part__Feature776  label="NINA-B306-00B-00--3DModel-STEP-56544 v152"
  Placement = pos=(35.642,8.89,0.805) rot=(0.57735,0.57735,0.57735;2.0944rad)
  shape: bbox 0.7 x 0.7 x 0.05 mm, 6 faces (baked)
FEATURE [Part::Feature] Part__Feature777  label="NINA-B306-00B-00--3DModel-STEP-56544 v153"
  Placement = pos=(35.642,8.89,0.805) rot=(0.57735,0.57735,0.57735;2.0944rad)
  shape: bbox 0.7 x 0.7 x 0.05 mm, 6 faces (baked)
FEATURE [Part::Feature] Part__Feature778  label="NINA-B306-00B-00--3DModel-STEP-56544 v154"
  Placement = pos=(35.642,8.89,0.805) rot=(0.57735,0.57735,0.57735;2.0944rad)
  shape: bbox 0.325 x 0.165 x 0.25 mm, 6 faces (baked)
FEATURE [Part::Feature] Part__Feature779  label="NINA-B306-00B-00--3DModel-STEP-56544 v155"
  Placement = pos=(35.642,8.89,0.805) rot=(0.57735,0.57735,0.57735;2.0944rad)
  shape: bbox 0.7 x 0.7 x 0.05 mm, 6 faces (baked)
FEATURE [Part::Feature] Part__Feature780  label="NINA-B306-00B-00--3DModel-STEP-56544 v156"
  Placement = pos=(35.642,8.89,0.805) rot=(0.57735,0.57735,0.57735;2.0944rad)
  shape: bbox 0.7 x 0.7 x 0.05 mm, 6 faces (baked)
FEATURE [Part::Feature] Part__Feature781  label="NINA-B306-00B-00--3DModel-STEP-56544 v157"
  Placement = pos=(35.642,8.89,0.805) rot=(0.57735,0.57735,0.57735;2.0944rad)
  shape: bbox 0.7 x 0.7 x 0.05 mm, 6 faces (baked)
FEATURE [Part::Feature] Part__Feature782  label="NINA-B306-00B-00--3DModel-STEP-56544 v158"
  Placement = pos=(35.642,8.89,0.805) rot=(0.57735,0.57735,0.57735;2.0944rad)
  shape: bbox 0.7 x 1.15 x 0.05 mm, 6 faces (baked)
FEATURE [Part::Feature] Part__Feature783  label="NINA-B306-00B-00--3DModel-STEP-56544 v159"
  Placement = pos=(35.642,8.89,0.805) rot=(0.57735,0.57735,0.57735;2.0944rad)
  shape: bbox 10.65 x 9.8 x 1.73 mm, 51 faces (baked)
FEATURE [Part::Feature] Part__Feature784  label="NINA-B306-00B-00--3DModel-STEP-56544 v160"
  Placement = pos=(35.642,8.89,0.805) rot=(0.57735,0.57735,0.57735;2.0944rad)
  shape: bbox 0.7 x 0.7 x 0.05 mm, 6 faces (baked)
FEATURE [Part::Feature] Part__Feature785  label="NINA-B306-00B-00--3DModel-STEP-56544 v161"
  Placement = pos=(35.642,8.89,0.805) rot=(0.57735,0.57735,0.57735;2.0944rad)
  shape: bbox 1.15 x 0.7 x 0.05 mm, 6 faces (baked)
FEATURE [Part::Feature] Part__Feature786  label="NINA-B306-00B-00--3DModel-STEP-56544 v162"
  Placement = pos=(35.642,8.89,0.805) rot=(0.57735,0.57735,0.57735;2.0944rad)
  shape: bbox 0.7 x 0.7 x 0.05 mm, 6 faces (baked)
FEATURE [Part::Feature] Part__Feature787  label="NINA-B306-00B-00--3DModel-STEP-56544 v163"
  Placement = pos=(35.642,8.89,0.805) rot=(0.57735,0.57735,0.57735;2.0944rad)
  shape: bbox 1.15 x 0.7 x 0.05 mm, 6 faces (baked)
FEATURE [Part::Feature] Part__Feature788  label="NINA-B306-00B-00--3DModel-STEP-56544 v164"
  Placement = pos=(35.642,8.89,0.805) rot=(0.57735,0.57735,0.57735;2.0944rad)
  shape: bbox 0.7 x 1.15 x 0.05 mm, 6 faces (baked)
FEATURE [Part::Feature] Part__Feature789  label="NINA-B306-00B-00--3DModel-STEP-56544 v165"
  Placement = pos=(35.642,8.89,0.805) rot=(0.57735,0.57735,0.57735;2.0944rad)
  shape: bbox 0.7 x 0.7 x 0.05 mm, 6 faces (baked)
FEATURE [Part::Feature] Part__Feature790  label="NINA-B306-00B-00--3DModel-STEP-56544 v166"
  Placement = pos=(35.642,8.89,0.805) rot=(0.57735,0.57735,0.57735;2.0944rad)
  shape: bbox 0.325 x 0.165 x 0.25 mm, 6 faces (baked)
FEATURE [Part::Feature] Part__Feature791  label="NINA-B306-00B-00--3DModel-STEP-56544 v167"
  Placement = pos=(35.642,8.89,0.805) rot=(0.57735,0.57735,0.57735;2.0944rad)
  shape: bbox 0.7 x 1.15 x 0.05 mm, 6 faces (baked)
FEATURE [Part::Feature] Part__Feature792  label="NINA-B306-00B-00--3DModel-STEP-56544 v168"
  Placement = pos=(35.642,8.89,0.805) rot=(0.57735,0.57735,0.57735;2.0944rad)
  shape: bbox 0.7 x 0.7 x 0.05 mm, 6 faces (baked)
FEATURE [Part::Feature] Part__Feature793  label="NINA-B306-00B-00--3DModel-STEP-56544 v169"
  Placement = pos=(35.642,8.89,0.805) rot=(0.57735,0.57735,0.57735;2.0944rad)
  shape: bbox 0.325 x 0.295 x 0.25 mm, 6 faces (baked)
FEATURE [Part::Feature] Part__Feature794  label="NINA-B306-00B-00--3DModel-STEP-56544 v170"
  Placement = pos=(35.642,8.89,0.805) rot=(0.57735,0.57735,0.57735;2.0944rad)
  shape: bbox 0.7 x 0.7 x 0.05 mm, 6 faces (baked)
FEATURE [Part::Feature] Part__Feature795  label="NINA-B306-00B-00--3DModel-STEP-56544 v171"
  Placement = pos=(35.642,8.89,0.805) rot=(0.57735,0.57735,0.57735;2.0944rad)
  shape: bbox 0.7 x 0.7 x 0.05 mm, 6 faces (baked)
FEATURE [Part::Feature] Part__Feature796  label="NINA-B306-00B-00--3DModel-STEP-56544 v172"
  Placement = pos=(35.642,8.89,0.805) rot=(0.57735,0.57735,0.57735;2.0944rad)
  shape: bbox 0.325 x 0.165 x 0.25 mm, 6 faces (baked)
FEATURE [Part::Feature] Part__Feature797  label="NINA-B306-00B-00--3DModel-STEP-56544 v173"
  Placement = pos=(35.642,8.89,0.805) rot=(0.57735,0.57735,0.57735;2.0944rad)
  shape: bbox 0.7 x 0.7 x 0.05 mm, 6 faces (baked)
FEATURE [Part::Feature] Part__Feature798  label="NINA-B306-00B-00--3DModel-STEP-56544 v174"
  Placement = pos=(35.642,8.89,0.805) rot=(0.57735,0.57735,0.57735;2.0944rad)
  shape: bbox 0.7 x 1.15 x 0.05 mm, 6 faces (baked)
FEATURE [Part::Feature] Part__Feature799  label="NINA-B306-00B-00--3DModel-STEP-56544 v175"
  Placement = pos=(35.642,8.89,0.805) rot=(0.57735,0.57735,0.57735;2.0944rad)
  shape: bbox 0.7 x 0.7 x 0.05 mm, 6 faces (baked)
FEATURE [Part::Feature] Part__Feature800  label="NINA-B306-00B-00--3DModel-STEP-56544 v176"
  Placement = pos=(35.642,8.89,0.805) rot=(0.57735,0.57735,0.57735;2.0944rad)
  shape: bbox 0.7 x 1.15 x 0.05 mm, 6 faces (baked)
FEATURE [Part::Feature] Part__Feature801  label="NINA-B306-00B-00--3DModel-STEP-56544 v177"
  Placement = pos=(35.642,8.89,0.805) rot=(0.57735,0.57735,0.57735;2.0944rad)
  shape: bbox 0.7 x 0.7 x 0.05 mm, 6 faces (baked)
FEATURE [Part::Feature] Part__Feature802  label="NINA-B306-00B-00--3DModel-STEP-56544 v178"
  Placement = pos=(35.642,8.89,0.805) rot=(0.57735,0.57735,0.57735;2.0944rad)
  shape: bbox 1.15 x 0.7 x 0.05 mm, 6 faces (baked)
FEATURE [App::Part] NINA_B306_00B_00__3DModel_STEP_56544_v002  label="NINA-B306-00B-00--3DModel-STEP-56544 v090"
  Group = -> [Part__Feature715,Part__Feature716,Part__Feature717,Part__Feature718,Part__Feature719,Part__Feature720,Part__Feature721,Part__Feature722,Part__Feature723,Part__Feature724,Part__Feature725,Part__Feature726,Part__Feature727,Part__Feature728,Part__Feature729,Part__Feature730,Part__Feature731,Part__Feature732,Part__Feature733,Part__Feature734,Part__Feature735,Part__Feature736,Part__Feature737,+65 more]
  Origin = -> Origin140
FEATURE [Part::Feature] Part__Feature803  label="I2C SPLITTER006"
  shape: bbox 8.151 x 3.401 x 4.801 mm, 98 faces (baked)
FEATURE [Part::Feature] Part__Feature804  label="I2C SPLITTER007"
  shape: bbox 0.3504 x 3.865 x 4.2 mm, 18 faces (baked)
FEATURE [Part::Feature] Part__Feature805  label="I2C SPLITTER008"
  shape: bbox 0.3504 x 3.865 x 4.2 mm, 18 faces (baked)
FEATURE [Part::Feature] Part__Feature806  label="I2C SPLITTER009"
  shape: bbox 0.3504 x 3.865 x 4.2 mm, 18 faces (baked)
FEATURE [Part::Feature] Part__Feature807  label="I2C SPLITTER010"
  shape: bbox 0.3504 x 3.865 x 4.2 mm, 18 faces (baked)
FEATURE [Part::MultiFuse] Fusion069  label="i2c001"
  Placement = pos=(17.82,2.2,-0.25) rot=(0,0,1;0rad)
  Shapes = -> [Part__Feature803,Part__Feature804,Part__Feature805,Part__Feature806,Part__Feature807]
FEATURE [App::Part] RC0402FR_071KL_RC0402N_YAG_v028  label="RC0402FR-071KL RC0402N_YAG v190"
  Group = -> [Part__Feature627,Part__Feature628,Part__Feature629]
  Origin = -> Origin115
FEATURE [App::Part] RC0402FR_071KL_RC0402N_YAG_v029  label="RC0402FR-071KL RC0402N_YAG v191"
  Group = -> [Part__Feature630,Part__Feature631,Part__Feature632]
  Origin = -> Origin116
FEATURE [App::Part] RC0402FR_071KL_RC0402N_YAG_v030  label="RC0402FR-071KL RC0402N_YAG v192"
  Group = -> [Part__Feature633,Part__Feature634,Part__Feature635]
  Origin = -> Origin117
FEATURE [App::Part] RC0402FR_071KL_RC0402N_YAG_v031  label="RC0402FR-071KL RC0402N_YAG v193"
  Group = -> [Part__Feature636,Part__Feature637,Part__Feature638]
  Origin = -> Origin118
FEATURE [App::Part] RC0402FR_071KL_RC0402N_YAG_v032  label="RC0402FR-071KL RC0402N_YAG v194"
  Group = -> [Part__Feature639,Part__Feature640,Part__Feature049]
  Origin = -> Origin009
FEATURE [App::Part] RC0402FR_071KL_RC0402N_YAG_v033  label="RC0402FR-071KL RC0402N_YAG v195"
  Group = -> [Part__Feature050,Part__Feature051,Part__Feature052]
  Origin = -> Origin010
FEATURE [App::Part] RC0402FR_071KL_RC0402N_YAG_v034  label="RC0402FR-071KL RC0402N_YAG v196"
  Group = -> [Part__Feature053,Part__Feature054,Part__Feature055]
  Origin = -> Origin011
FEATURE [App::Part] RC0402FR_071KL_RC0402N_YAG_v035  label="RC0402FR-071KL RC0402N_YAG v197"
  Group = -> [Part__Feature641,Part__Feature642,Part__Feature058]
  Origin = -> Origin012
FEATURE [App::Part] RC0402FR_071KL_RC0402N_YAG_v036  label="RC0402FR-071KL RC0402N_YAG v198"
  Group = -> [Part__Feature643,Part__Feature644,Part__Feature645]
  Origin = -> Origin013
FEATURE [App::Part] RC0402FR_071KL_RC0402N_YAG_v037  label="RC0402FR-071KL RC0402N_YAG v199"
  Group = -> [Part__Feature646,Part__Feature647,Part__Feature648]
  Origin = -> Origin014
FEATURE [App::Part] RC0402FR_071KL_RC0402N_YAG_v038  label="RC0402FR-071KL RC0402N_YAG v200"
  Group = -> [Part__Feature649,Part__Feature650,Part__Feature651]
  Origin = -> Origin119
FEATURE [App::Part] RC0402FR_071KL_RC0402N_YAG_v039  label="RC0402FR-071KL RC0402N_YAG v201"
  Group = -> [Part__Feature652,Part__Feature653,Part__Feature654]
  Origin = -> Origin016
FEATURE [App::Part] RC0402FR_071KL_RC0402N_YAG_v040  label="RC0402FR-071KL RC0402N_YAG v202"
  Group = -> [Part__Feature655,Part__Feature656,Part__Feature657]
  Origin = -> Origin120
FEATURE [App::Part] RC0402FR_071KL_RC0402N_YAG_v041  label="RC0402FR-071KL RC0402N_YAG v203"
  Group = -> [Part__Feature658,Part__Feature659,Part__Feature660]
  Origin = -> Origin121
FEATURE [App::Part] RC0402FR_071KL_RC0402N_YAG_v042  label="RC0402FR-071KL RC0402N_YAG v204"
  Group = -> [Part__Feature661,Part__Feature662,Part__Feature663]
  Origin = -> Origin122
FEATURE [App::Part] RC0402FR_071KL_RC0402N_YAG_v043  label="RC0402FR-071KL RC0402N_YAG v205"
  Group = -> [Part__Feature664,Part__Feature665,Part__Feature666]
  Origin = -> Origin123
FEATURE [App::Part] RC0402FR_071KL_RC0402N_YAG_v044  label="RC0402FR-071KL RC0402N_YAG v206"
  Group = -> [Part__Feature667,Part__Feature668,Part__Feature669]
  Origin = -> Origin124
FEATURE [App::Part] RC0402FR_071KL_RC0402N_YAG_v045  label="RC0402FR-071KL RC0402N_YAG v207"
  Group = -> [Part__Feature670,Part__Feature671,Part__Feature672]
  Origin = -> Origin125
FEATURE [App::Part] RC0402FR_071KL_RC0402N_YAG_v046  label="RC0402FR-071KL RC0402N_YAG v208"
  Group = -> [Part__Feature673,Part__Feature674,Part__Feature675]
  Origin = -> Origin126
FEATURE [App::Part] RC0402FR_071KL_RC0402N_YAG_v047  label="RC0402FR-071KL RC0402N_YAG v209"
  Group = -> [Part__Feature676,Part__Feature677,Part__Feature678]
  Origin = -> Origin127
FEATURE [App::Part] RC0402FR_071KL_RC0402N_YAG_v048  label="RC0402FR-071KL RC0402N_YAG v210"
  Group = -> [Part__Feature679,Part__Feature680,Part__Feature681]
  Origin = -> Origin128
FEATURE [App::Part] RC0402FR_071KL_RC0402N_YAG_v049  label="RC0402FR-071KL RC0402N_YAG v211"
  Group = -> [Part__Feature682,Part__Feature683,Part__Feature684]
  Origin = -> Origin129
FEATURE [App::Part] RC0402FR_071KL_RC0402N_YAG_v050  label="RC0402FR-071KL RC0402N_YAG v212"
  Group = -> [Part__Feature685,Part__Feature686,Part__Feature687]
  Origin = -> Origin130
FEATURE [App::Part] RC0402FR_071KL_RC0402N_YAG_v051  label="RC0402FR-071KL RC0402N_YAG v213"
  Group = -> [Part__Feature688,Part__Feature689,Part__Feature690]
  Origin = -> Origin131
FEATURE [App::Part] RC0402FR_071KL_RC0402N_YAG_v052  label="RC0402FR-071KL RC0402N_YAG v214"
  Group = -> [Part__Feature691,Part__Feature692,Part__Feature693]
  Origin = -> Origin132
FEATURE [App::Part] RC0402FR_071KL_RC0402N_YAG_v053  label="RC0402FR-071KL RC0402N_YAG v215"
  Group = -> [Part__Feature694,Part__Feature695,Part__Feature696]
  Origin = -> Origin133
FEATURE [App::Part] RC0402FR_071KL_RC0402N_YAG_v054  label="RC0402FR-071KL RC0402N_YAG v216"
  Group = -> [Part__Feature624,Part__Feature625,Part__Feature626]
  Origin = -> Origin114
FEATURE [App::Part] RC0402FR_071KL001  label="RC0402FR-071KL001"
  Group = -> [RC0402FR_071KL_RC0402N_YAG_v054,RC0402FR_071KL_RC0402N_YAG_v028,RC0402FR_071KL_RC0402N_YAG_v029,RC0402FR_071KL_RC0402N_YAG_v030,RC0402FR_071KL_RC0402N_YAG_v031,RC0402FR_071KL_RC0402N_YAG_v032,RC0402FR_071KL_RC0402N_YAG_v033,RC0402FR_071KL_RC0402N_YAG_v034,RC0402FR_071KL_RC0402N_YAG_v035,RC0402FR_071KL_RC0402N_YAG_v036,RC0402FR_071KL_RC0402N_YAG_v037,RC0402FR_071KL_RC0402N_YAG_v038,+15 more]
  Origin = -> Origin134
FEATURE [Sketcher::SketchObject] Sketch043
  ArcFitTolerance = 1e-06
  FullyConstrained = true
  MakeInternals = false
  sketch-geometry (8):
    g0: LineSegment StartX=-5 StartY=15 StartZ=0 EndX=-5 EndY=-12 EndZ=0
    g1: LineSegment StartX=-5 StartY=-12 StartZ=0 EndX=48 EndY=-12 EndZ=0
    g2: LineSegment StartX=48 StartY=-12 StartZ=0 EndX=48 EndY=15 EndZ=0
    g3: LineSegment StartX=48 StartY=15 StartZ=0 EndX=-5 EndY=15 EndZ=0
    g4: Circle CenterX=1.275 CenterY=8.5 CenterZ=0 NormalX=0 NormalY=0 NormalZ=1 AngleXU=0 Radius=1.1
    g5: Circle CenterX=1.275 CenterY=-6.725 CenterZ=0 NormalX=0 NormalY=0 NormalZ=1 AngleXU=0 Radius=1.1
    g6: Circle CenterX=41.91 CenterY=8.5 CenterZ=0 NormalX=0 NormalY=0 NormalZ=1 AngleXU=0 Radius=1.1
    g7: Circle CenterX=41.91 CenterY=-6.725 CenterZ=0 NormalX=0 NormalY=0 NormalZ=1 AngleXU=0 Radius=1.1
  constraints (24):
    c: Vertical(g0)
    c: Coincident(g1,g0)
    c: Horizontal(g1)
    c: Coincident(g2,g1)
    c: Vertical(g2)
    c: Coincident(g3,g2)
    c: Coincident(g3,g0)
    c: Horizontal(g3)
    c: Distance(g0,g-1) = 12
    c: Distance(g-1,g0) = 5
    c: Distance(g0,g-1) = 15
    c: Distance(g2,g-2) = 48
    c: Equal(g4,g5)
    c: Equal(g4,g6)
    c: Equal(g4,g7)
    c: Diameter(g4) = 2.2
    c: Distance(g4,g-1) = 8.5
    c: Distance(g4,g0) = 6.275
    c: Distance(g5,g0) = 6.275
    c: Distance(g7,g-2) = 41.91
    c: Distance(g6,g-2) = 41.91
    c: Distance(g6,g-1) = 8.5
    c: Distance(g5,g-1) = 6.725
    c: Distance(g7,g-1) = 6.725
FEATURE [Part::Extrusion] Extrude041  label="arduinoHold001"
  Base = -> Sketch043
  Dir = (0,0,1)
  DirMode = 2
  FaceMakerClass = Part::FaceMakerBullseye
  FaceMakerMode = 3
  LengthFwd = 3
  LengthRev = 0
  Reversed = true
  Solid = true
  Symmetric = false
FEATURE [Sketcher::SketchObject] Sketch044
  ArcFitTolerance = 0
  FullyConstrained = true
  MakeInternals = false
  sketch-geometry (29):
    g0: LineSegment StartX=0 StartY=0 StartZ=0 EndX=8 EndY=2e-16 EndZ=0
    g1: LineSegment StartX=12 StartY=0 StartZ=0 EndX=28 EndY=2e-16 EndZ=0
    g2: LineSegment StartX=0 StartY=0 StartZ=0 EndX=-4e-16 EndY=8 EndZ=0
    g3: LineSegment StartX=1e-16 StartY=52 StartZ=0 EndX=0 EndY=60 EndZ=0
    g4: LineSegment StartX=0 StartY=60 StartZ=0 EndX=8 EndY=60 EndZ=0
    g5: LineSegment StartX=12 StartY=60 StartZ=0 EndX=28 EndY=60 EndZ=0
    g6: LineSegment StartX=32 StartY=60 StartZ=0 EndX=40 EndY=60 EndZ=0
    g7: LineSegment StartX=40 StartY=60 StartZ=0 EndX=40 EndY=52 EndZ=0
    g8: LineSegment StartX=40 StartY=48 StartZ=0 EndX=40 EndY=32 EndZ=0
    g9: LineSegment StartX=40 StartY=28 StartZ=0 EndX=40 EndY=12 EndZ=0
    g10: LineSegment StartX=40 StartY=8 StartZ=0 EndX=40 EndY=0 EndZ=0
    g11: LineSegment StartX=40 StartY=0 StartZ=0 EndX=32 EndY=-5e-16 EndZ=0
    g12: LineSegment StartX=-4e-16 StartY=48 StartZ=0 EndX=6e-16 EndY=32 EndZ=0
    g13: LineSegment StartX=-4e-16 StartY=28 StartZ=0 EndX=1e-16 EndY=12 EndZ=0
    g14: ArcOfCircle CenterX=10 CenterY=0 CenterZ=0 NormalX=0 NormalY=0 NormalZ=1 AngleXU=0 Radius=2 StartAngle=0 EndAngle=3.14159
    g15: ArcOfCircle CenterX=30 CenterY=0 CenterZ=0 NormalX=0 NormalY=0 NormalZ=1 AngleXU=0 Radius=2 StartAngle=3.14159 EndAngle=6.28319
    g16: ArcOfCircle CenterX=0 CenterY=10 CenterZ=0 NormalX=0 NormalY=0 NormalZ=1 AngleXU=0 Radius=2 StartAngle=1.5708 EndAngle=4.71239
    g17: ArcOfCircle CenterX=0 CenterY=30 CenterZ=0 NormalX=0 NormalY=0 NormalZ=1 AngleXU=0 Radius=2 StartAngle=4.71239 EndAngle=7.85398
    g18: ArcOfCircle CenterX=0 CenterY=50 CenterZ=0 NormalX=0 NormalY=0 NormalZ=1 AngleXU=0 Radius=2 StartAngle=1.5708 EndAngle=4.71239
    g19: ArcOfCircle CenterX=10 CenterY=60 CenterZ=0 NormalX=0 NormalY=0 NormalZ=1 AngleXU=0 Radius=2 StartAngle=3.14159 EndAngle=6.28319
    g20: ArcOfCircle CenterX=30 CenterY=60 CenterZ=0 NormalX=0 NormalY=0 NormalZ=1 AngleXU=0 Radius=2 StartAngle=4e-16 EndAngle=3.14159
    g21: ArcOfCircle CenterX=40 CenterY=50 CenterZ=0 NormalX=0 NormalY=0 NormalZ=1 AngleXU=0 Radius=2 StartAngle=1.5708 EndAngle=4.71239
    g22: ArcOfCircle CenterX=40 CenterY=30 CenterZ=0 NormalX=0 NormalY=0 NormalZ=1 AngleXU=0 Radius=2 StartAngle=4.71239 EndAngle=7.85398
    g23: ArcOfCircle CenterX=40 CenterY=10 CenterZ=0 NormalX=0 NormalY=0 NormalZ=1 AngleXU=0 Radius=2 StartAngle=1.5708 EndAngle=4.71239
    g24: Circle CenterX=30 CenterY=0 CenterZ=0 NormalX=0 NormalY=0 NormalZ=1 AngleXU=0 Radius=1
    g25: Circle CenterX=40 CenterY=30 CenterZ=0 NormalX=0 NormalY=0 NormalZ=1 AngleXU=0 Radius=1
    g26: Circle CenterX=30 CenterY=60 CenterZ=0 NormalX=0 NormalY=0 NormalZ=1 AngleXU=0 Radius=1
    g27: Circle CenterX=0 CenterY=50 CenterZ=0 NormalX=0 NormalY=0 NormalZ=1 AngleXU=0 Radius=1
    g28: Circle CenterX=0 CenterY=10 CenterZ=0 NormalX=0 NormalY=0 NormalZ=1 AngleXU=0 Radius=1
  constraints (88):
    c: Coincident(g0,g-1)
    c: PointOnObject(g0,g-1)
    c: PointOnObject(g1,g-1)
    c: PointOnObject(g1,g-1)
    c: Coincident(g2,g0)
    c: PointOnObject(g2,g-2)
    c: PointOnObject(g3,g-2)
    c: PointOnObject(g3,g-2)
    c: Coincident(g4,g3)
    c: Horizontal(g4)
    c: Horizontal(g5)
    c: Coincident(g7,g6)
    c: Vertical(g7)
    c: Vertical(g8)
    c: Vertical(g9)
    c: PointOnObject(g10,g-1)
    c: Coincident(g11,g10)
    c: PointOnObject(g11,g-1)
    c: PointOnObject(g12,g-2)
    c: PointOnObject(g12,g-2)
    c: PointOnObject(g13,g-2)
    c: PointOnObject(g13,g-2)
    c: Distance(g0) = 8
    c: Coincident(g14,g0)
    c: Coincident(g14,g1)
    c: Diameter(g14) = 4
    c: Distance(g1) = 16
    c: Coincident(g15,g1)
    c: Coincident(g15,g11)
    c: Diameter(g15) = 4
    c: PointOnObject(g15,g-1)
    c: Distance(g11) = 8
    c: Vertical(g10)
    c: Distance(g2) = 8
    c: Coincident(g16,g2)
    c: Coincident(g16,g13)
    c: PointOnObject(g16,g-2)
    c: Diameter(g16) = 4
    c: Distance(g13) = 16
    c: Distance(g12) = 16
    c: PointOnObject(g14,g-1)
    c: Coincident(g17,g13)
    c: Coincident(g17,g12)
    c: PointOnObject(g17,g-2)
    c: Diameter(g17) = 4
    c: Coincident(g18,g12)
    c: Coincident(g18,g3)
    c: PointOnObject(g18,g-2)
    c: Diameter(g18) = 4
    c: Distance(g3) = 8
    c: Distance(g4) = 8
    c: Coincident(g19,g4)
    c: Coincident(g19,g5)
    c: Distance(g19,g-1) = 60
    c: Diameter(g19) = 4
    c: Distance(g5) = 16
    c: Distance(g3,g5) = 12
    c: Coincident(g20,g5)
    c: Coincident(g20,g6)
    c: Distance(g20,g-1) = 60
    c: Diameter(g20) = 4
    c: Distance(g6,g-1) = 60
    c: Horizontal(g6)
    c: Distance(g6) = 8
    c: Distance(g7) = 8
    c: Coincident(g21,g7)
    c: Coincident(g21,g8)
    c: Distance(g18,g21) = 40
    c: Distance(g8) = 16
    c: Diameter(g21) = 4
    c: Distance(g8,g-2) = 40
    c: Distance(g9) = 16
    c: Distance(g9,g-2) = 40
    c: Coincident(g22,g8)
    c: Coincident(g22,g9)
    c: Diameter(g22) = 4
    c: Distance(g22,g17) = 40
    c: Coincident(g23,g9)
    c: Coincident(g23,g10)
    c: Diameter(g23) = 4
    c: Distance(g16,g23) = 40
    c: Coincident(g24,g15)
    c: Coincident(g25,g22)
    c: Coincident(g26,g20)
    c: Coincident(g27,g18)
    c: Coincident(g28,g16)
    c: Equal(g24, g25-g28) x4
    c: Diameter(g24) = 2
FEATURE [Part::Extrusion] Extrude042
  Base = -> Sketch044
  Dir = (0,0,1)
  DirMode = 2
  FaceMakerClass = Part::FaceMakerBullseye
  FaceMakerMode = 3
  LengthFwd = 1.5
  LengthRev = 0
  Solid = true
  Symmetric = false
FEATURE [App::Part] Part024  label="SSR001"
  Group = -> [Sketch044,Extrude042,Box085,Box084,Box086,Box087,Fusion067,Box090,Box088,Box089,Box091,Fusion068,Part__Feature803,Part__Feature804,Part__Feature806,Part__Feature805,Part__Feature807,Fusion069]
  Origin = -> Origin042
  Placement = pos=(-17,-16,-6) rot=(-0.57735,-0.57735,0.57735;4.18879rad)
FEATURE [Sketcher::SketchObject] Sketch045
  ArcFitTolerance = 0
  FullyConstrained = true
  MakeInternals = false
  sketch-geometry (29):
    g0: LineSegment StartX=0 StartY=0 StartZ=0 EndX=8 EndY=2e-16 EndZ=0
    g1: LineSegment StartX=12 StartY=0 StartZ=0 EndX=28 EndY=2e-16 EndZ=0
    g2: LineSegment StartX=0 StartY=0 StartZ=0 EndX=-4e-16 EndY=8 EndZ=0
    g3: LineSegment StartX=1e-16 StartY=52 StartZ=0 EndX=0 EndY=60 EndZ=0
    g4: LineSegment StartX=0 StartY=60 StartZ=0 EndX=8 EndY=60 EndZ=0
    g5: LineSegment StartX=12 StartY=60 StartZ=0 EndX=28 EndY=60 EndZ=0
    g6: LineSegment StartX=32 StartY=60 StartZ=0 EndX=40 EndY=60 EndZ=0
    g7: LineSegment StartX=40 StartY=60 StartZ=0 EndX=40 EndY=52 EndZ=0
    g8: LineSegment StartX=40 StartY=48 StartZ=0 EndX=40 EndY=32 EndZ=0
    g9: LineSegment StartX=40 StartY=28 StartZ=0 EndX=40 EndY=12 EndZ=0
    g10: LineSegment StartX=40 StartY=8 StartZ=0 EndX=40 EndY=0 EndZ=0
    g11: LineSegment StartX=40 StartY=0 StartZ=0 EndX=32 EndY=-5e-16 EndZ=0
    g12: LineSegment StartX=-4e-16 StartY=48 StartZ=0 EndX=6e-16 EndY=32 EndZ=0
    g13: LineSegment StartX=-4e-16 StartY=28 StartZ=0 EndX=1e-16 EndY=12 EndZ=0
    g14: ArcOfCircle CenterX=10 CenterY=0 CenterZ=0 NormalX=0 NormalY=0 NormalZ=1 AngleXU=0 Radius=2 StartAngle=0 EndAngle=3.14159
    g15: ArcOfCircle CenterX=30 CenterY=0 CenterZ=0 NormalX=0 NormalY=0 NormalZ=1 AngleXU=0 Radius=2 StartAngle=3.14159 EndAngle=6.28319
    g16: ArcOfCircle CenterX=0 CenterY=10 CenterZ=0 NormalX=0 NormalY=0 NormalZ=1 AngleXU=0 Radius=2 StartAngle=1.5708 EndAngle=4.71239
    g17: ArcOfCircle CenterX=0 CenterY=30 CenterZ=0 NormalX=0 NormalY=0 NormalZ=1 AngleXU=0 Radius=2 StartAngle=4.71239 EndAngle=7.85398
    g18: ArcOfCircle CenterX=0 CenterY=50 CenterZ=0 NormalX=0 NormalY=0 NormalZ=1 AngleXU=0 Radius=2 StartAngle=1.5708 EndAngle=4.71239
    g19: ArcOfCircle CenterX=10 CenterY=60 CenterZ=0 NormalX=0 NormalY=0 NormalZ=1 AngleXU=0 Radius=2 StartAngle=3.14159 EndAngle=6.28319
    g20: ArcOfCircle CenterX=30 CenterY=60 CenterZ=0 NormalX=0 NormalY=0 NormalZ=1 AngleXU=0 Radius=2 StartAngle=4e-16 EndAngle=3.14159
    g21: ArcOfCircle CenterX=40 CenterY=50 CenterZ=0 NormalX=0 NormalY=0 NormalZ=1 AngleXU=0 Radius=2 StartAngle=1.5708 EndAngle=4.71239
    g22: ArcOfCircle CenterX=40 CenterY=30 CenterZ=0 NormalX=0 NormalY=0 NormalZ=1 AngleXU=0 Radius=2 StartAngle=4.71239 EndAngle=7.85398
    g23: ArcOfCircle CenterX=40 CenterY=10 CenterZ=0 NormalX=0 NormalY=0 NormalZ=1 AngleXU=0 Radius=2 StartAngle=1.5708 EndAngle=4.71239
    g24: Circle CenterX=30 CenterY=0 CenterZ=0 NormalX=0 NormalY=0 NormalZ=1 AngleXU=0 Radius=1
    g25: Circle CenterX=40 CenterY=30 CenterZ=0 NormalX=0 NormalY=0 NormalZ=1 AngleXU=0 Radius=1
    g26: Circle CenterX=30 CenterY=60 CenterZ=0 NormalX=0 NormalY=0 NormalZ=1 AngleXU=0 Radius=1
    g27: Circle CenterX=0 CenterY=50 CenterZ=0 NormalX=0 NormalY=0 NormalZ=1 AngleXU=0 Radius=1
    g28: Circle CenterX=0 CenterY=10 CenterZ=0 NormalX=0 NormalY=0 NormalZ=1 AngleXU=0 Radius=1
  constraints (88):
    c: Coincident(g0,g-1)
    c: PointOnObject(g0,g-1)
    c: PointOnObject(g1,g-1)
    c: PointOnObject(g1,g-1)
    c: Coincident(g2,g0)
    c: PointOnObject(g2,g-2)
    c: PointOnObject(g3,g-2)
    c: PointOnObject(g3,g-2)
    c: Coincident(g4,g3)
    c: Horizontal(g4)
    c: Horizontal(g5)
    c: Coincident(g7,g6)
    c: Vertical(g7)
    c: Vertical(g8)
    c: Vertical(g9)
    c: PointOnObject(g10,g-1)
    c: Coincident(g11,g10)
    c: PointOnObject(g11,g-1)
    c: PointOnObject(g12,g-2)
    c: PointOnObject(g12,g-2)
    c: PointOnObject(g13,g-2)
    c: PointOnObject(g13,g-2)
    c: Distance(g0) = 8
    c: Coincident(g14,g0)
    c: Coincident(g14,g1)
    c: Diameter(g14) = 4
    c: Distance(g1) = 16
    c: Coincident(g15,g1)
    c: Coincident(g15,g11)
    c: Diameter(g15) = 4
    c: PointOnObject(g15,g-1)
    c: Distance(g11) = 8
    c: Vertical(g10)
    c: Distance(g2) = 8
    c: Coincident(g16,g2)
    c: Coincident(g16,g13)
    c: PointOnObject(g16,g-2)
    c: Diameter(g16) = 4
    c: Distance(g13) = 16
    c: Distance(g12) = 16
    c: PointOnObject(g14,g-1)
    c: Coincident(g17,g13)
    c: Coincident(g17,g12)
    c: PointOnObject(g17,g-2)
    c: Diameter(g17) = 4
    c: Coincident(g18,g12)
    c: Coincident(g18,g3)
    c: PointOnObject(g18,g-2)
    c: Diameter(g18) = 4
    c: Distance(g3) = 8
    c: Distance(g4) = 8
    c: Coincident(g19,g4)
    c: Coincident(g19,g5)
    c: Distance(g19,g-1) = 60
    c: Diameter(g19) = 4
    c: Distance(g5) = 16
    c: Distance(g3,g5) = 12
    c: Coincident(g20,g5)
    c: Coincident(g20,g6)
    c: Distance(g20,g-1) = 60
    c: Diameter(g20) = 4
    c: Distance(g6,g-1) = 60
    c: Horizontal(g6)
    c: Distance(g6) = 8
    c: Distance(g7) = 8
    c: Coincident(g21,g7)
    c: Coincident(g21,g8)
    c: Distance(g18,g21) = 40
    c: Distance(g8) = 16
    c: Diameter(g21) = 4
    c: Distance(g8,g-2) = 40
    c: Distance(g9) = 16
    c: Distance(g9,g-2) = 40
    c: Coincident(g22,g8)
    c: Coincident(g22,g9)
    c: Diameter(g22) = 4
    c: Distance(g22,g17) = 40
    c: Coincident(g23,g9)
    c: Coincident(g23,g10)
    c: Diameter(g23) = 4
    c: Distance(g16,g23) = 40
    c: Coincident(g24,g15)
    c: Coincident(g25,g22)
    c: Coincident(g26,g20)
    c: Coincident(g27,g18)
    c: Coincident(g28,g16)
    c: Equal(g24, g25-g28) x4
    c: Diameter(g24) = 2
FEATURE [Part::Extrusion] Extrude043
  Base = -> Sketch045
  Dir = (0,0,1)
  DirMode = 2
  FaceMakerClass = Part::FaceMakerBullseye
  FaceMakerMode = 3
  LengthFwd = 5
  LengthRev = 0
  Placement = pos=(-17,-18,0) rot=(-0.57735,-0.57735,0.57735;4.18879rad)
  Solid = true
  Symmetric = false
FEATURE [Sketcher::SketchObject] Sketch046
  ArcFitTolerance = 0
  FullyConstrained = true
  MakeInternals = false
  sketch-geometry (29):
    g0: LineSegment StartX=0 StartY=0 StartZ=0 EndX=8 EndY=2e-16 EndZ=0
    g1: LineSegment StartX=12 StartY=0 StartZ=0 EndX=28 EndY=2e-16 EndZ=0
    g2: LineSegment StartX=0 StartY=0 StartZ=0 EndX=-4e-16 EndY=8 EndZ=0
    g3: LineSegment StartX=1e-16 StartY=52 StartZ=0 EndX=0 EndY=60 EndZ=0
    g4: LineSegment StartX=0 StartY=60 StartZ=0 EndX=8 EndY=60 EndZ=0
    g5: LineSegment StartX=12 StartY=60 StartZ=0 EndX=28 EndY=60 EndZ=0
    g6: LineSegment StartX=32 StartY=60 StartZ=0 EndX=40 EndY=60 EndZ=0
    g7: LineSegment StartX=40 StartY=60 StartZ=0 EndX=40 EndY=52 EndZ=0
    g8: LineSegment StartX=40 StartY=48 StartZ=0 EndX=40 EndY=32 EndZ=0
    g9: LineSegment StartX=40 StartY=28 StartZ=0 EndX=40 EndY=12 EndZ=0
    g10: LineSegment StartX=40 StartY=8 StartZ=0 EndX=40 EndY=0 EndZ=0
    g11: LineSegment StartX=40 StartY=0 StartZ=0 EndX=32 EndY=-5e-16 EndZ=0
    g12: LineSegment StartX=-4e-16 StartY=48 StartZ=0 EndX=6e-16 EndY=32 EndZ=0
    g13: LineSegment StartX=-4e-16 StartY=28 StartZ=0 EndX=1e-16 EndY=12 EndZ=0
    g14: ArcOfCircle CenterX=10 CenterY=0 CenterZ=0 NormalX=0 NormalY=0 NormalZ=1 AngleXU=0 Radius=2 StartAngle=0 EndAngle=3.14159
    g15: ArcOfCircle CenterX=30 CenterY=0 CenterZ=0 NormalX=0 NormalY=0 NormalZ=1 AngleXU=0 Radius=2 StartAngle=3.14159 EndAngle=6.28319
    g16: ArcOfCircle CenterX=0 CenterY=10 CenterZ=0 NormalX=0 NormalY=0 NormalZ=1 AngleXU=0 Radius=2 StartAngle=1.5708 EndAngle=4.71239
    g17: ArcOfCircle CenterX=0 CenterY=30 CenterZ=0 NormalX=0 NormalY=0 NormalZ=1 AngleXU=0 Radius=2 StartAngle=4.71239 EndAngle=7.85398
    g18: ArcOfCircle CenterX=0 CenterY=50 CenterZ=0 NormalX=0 NormalY=0 NormalZ=1 AngleXU=0 Radius=2 StartAngle=1.5708 EndAngle=4.71239
    g19: ArcOfCircle CenterX=10 CenterY=60 CenterZ=0 NormalX=0 NormalY=0 NormalZ=1 AngleXU=0 Radius=2 StartAngle=3.14159 EndAngle=6.28319
    g20: ArcOfCircle CenterX=30 CenterY=60 CenterZ=0 NormalX=0 NormalY=0 NormalZ=1 AngleXU=0 Radius=2 StartAngle=4e-16 EndAngle=3.14159
    g21: ArcOfCircle CenterX=40 CenterY=50 CenterZ=0 NormalX=0 NormalY=0 NormalZ=1 AngleXU=0 Radius=2 StartAngle=1.5708 EndAngle=4.71239
    g22: ArcOfCircle CenterX=40 CenterY=30 CenterZ=0 NormalX=0 NormalY=0 NormalZ=1 AngleXU=0 Radius=2 StartAngle=4.71239 EndAngle=7.85398
    g23: ArcOfCircle CenterX=40 CenterY=10 CenterZ=0 NormalX=0 NormalY=0 NormalZ=1 AngleXU=0 Radius=2 StartAngle=1.5708 EndAngle=4.71239
    g24: Circle CenterX=30 CenterY=0 CenterZ=0 NormalX=0 NormalY=0 NormalZ=1 AngleXU=0 Radius=1
    g25: Circle CenterX=40 CenterY=30 CenterZ=0 NormalX=0 NormalY=0 NormalZ=1 AngleXU=0 Radius=1
    g26: Circle CenterX=30 CenterY=60 CenterZ=0 NormalX=0 NormalY=0 NormalZ=1 AngleXU=0 Radius=1
    g27: Circle CenterX=0 CenterY=50 CenterZ=0 NormalX=0 NormalY=0 NormalZ=1 AngleXU=0 Radius=1
    g28: Circle CenterX=0 CenterY=10 CenterZ=0 NormalX=0 NormalY=0 NormalZ=1 AngleXU=0 Radius=1
  constraints (88):
    c: Coincident(g0,g-1)
    c: PointOnObject(g0,g-1)
    c: PointOnObject(g1,g-1)
    c: PointOnObject(g1,g-1)
    c: Coincident(g2,g0)
    c: PointOnObject(g2,g-2)
    c: PointOnObject(g3,g-2)
    c: PointOnObject(g3,g-2)
    c: Coincident(g4,g3)
    c: Horizontal(g4)
    c: Horizontal(g5)
    c: Coincident(g7,g6)
    c: Vertical(g7)
    c: Vertical(g8)
    c: Vertical(g9)
    c: PointOnObject(g10,g-1)
    c: Coincident(g11,g10)
    c: PointOnObject(g11,g-1)
    c: PointOnObject(g12,g-2)
    c: PointOnObject(g12,g-2)
    c: PointOnObject(g13,g-2)
    c: PointOnObject(g13,g-2)
    c: Distance(g0) = 8
    c: Coincident(g14,g0)
    c: Coincident(g14,g1)
    c: Diameter(g14) = 4
    c: Distance(g1) = 16
    c: Coincident(g15,g1)
    c: Coincident(g15,g11)
    c: Diameter(g15) = 4
    c: PointOnObject(g15,g-1)
    c: Distance(g11) = 8
    c: Vertical(g10)
    c: Distance(g2) = 8
    c: Coincident(g16,g2)
    c: Coincident(g16,g13)
    c: PointOnObject(g16,g-2)
    c: Diameter(g16) = 4
    c: Distance(g13) = 16
    c: Distance(g12) = 16
    c: PointOnObject(g14,g-1)
    c: Coincident(g17,g13)
    c: Coincident(g17,g12)
    c: PointOnObject(g17,g-2)
    c: Diameter(g17) = 4
    c: Coincident(g18,g12)
    c: Coincident(g18,g3)
    c: PointOnObject(g18,g-2)
    c: Diameter(g18) = 4
    c: Distance(g3) = 8
    c: Distance(g4) = 8
    c: Coincident(g19,g4)
    c: Coincident(g19,g5)
    c: Distance(g19,g-1) = 60
    c: Diameter(g19) = 4
    c: Distance(g5) = 16
    c: Distance(g3,g5) = 12
    c: Coincident(g20,g5)
    c: Coincident(g20,g6)
    c: Distance(g20,g-1) = 60
    c: Diameter(g20) = 4
    c: Distance(g6,g-1) = 60
    c: Horizontal(g6)
    c: Distance(g6) = 8
    c: Distance(g7) = 8
    c: Coincident(g21,g7)
    c: Coincident(g21,g8)
    c: Distance(g18,g21) = 40
    c: Distance(g8) = 16
    c: Diameter(g21) = 4
    c: Distance(g8,g-2) = 40
    c: Distance(g9) = 16
    c: Distance(g9,g-2) = 40
    c: Coincident(g22,g8)
    c: Coincident(g22,g9)
    c: Diameter(g22) = 4
    c: Distance(g22,g17) = 40
    c: Coincident(g23,g9)
    c: Coincident(g23,g10)
    c: Diameter(g23) = 4
    c: Distance(g16,g23) = 40
    c: Coincident(g24,g15)
    c: Coincident(g25,g22)
    c: Coincident(g26,g20)
    c: Coincident(g27,g18)
    c: Coincident(g28,g16)
    c: Equal(g24, g25-g28) x4
    c: Diameter(g24) = 2
FEATURE [Part::Extrusion] Extrude044
  Base = -> Sketch046
  Dir = (0,0,1)
  DirMode = 2
  FaceMakerClass = Part::FaceMakerBullseye
  FaceMakerMode = 3
  LengthFwd = 5
  LengthRev = 0
  Placement = pos=(-17,-18,0) rot=(-0.57735,-0.57735,0.57735;4.18879rad)
  Solid = true
  Symmetric = false
FEATURE [Part::Cut] Cut059  label="base_cut001"
  Base = -> Box092
  Refine = true
  Tool = -> Extrude044
FEATURE [Part::MultiFuse] Fusion070
  Refine = true
  Shapes = -> [Cut059,Box093,Box010]
FEATURE [Part::MultiFuse] Fusion071  label="ssrHold001"
  Placement = pos=(0,7,-6) rot=(0,0,1;0rad)
  Refine = true
  Shapes = -> [Extrude043,Fusion070]
FEATURE [Part::MultiFuse] Fusion072  label="fusedHold001"
  Refine = true
  Shapes = -> [Extrude041,Fusion071]
FEATURE [Part::Cut] Cut060  label="ssr_nano_hold001"
  Base = -> Fusion072
  Refine = true
  Tool = -> Fusion073
FEATURE [Part::MultiFuse] Fusion075  label="SSR_Nano001"
  Refine = true
  Shapes = -> [Cut060,Fusion074]
FEATURE [Part::Fillet] Fillet039
  Base = -> Fusion075
  EdgeLinks = -> Fusion075 [Edge1,Edge2,Edge3,Edge4,Edge5,Edge7,Edge8,Edge9,Edge15,Edge16,Edge17,Edge18,Edge19,Edge21,Edge22,Edge23,Edge28,Edge29,Edge32,Edge33,Edge34,Edge36,Edge37]
  Edges = 23 edges: [Edge1 r=1,Edge2 r=2,Edge3 r=1,Edge4 r=1,Edge5 r=1,Edge7 r=2,Edge8 r=3,Edge9 r=1,Edge15 r=1,Edge16 r=1,Edge17 r=1,Edge18 r=3,Edge19 r=1,Edge21 r=1,Edge22 r=1,Edge23 r=1,Edge28 r=1,Edge29 r=1,Edge32 r=1,Edge33 r=1,Edge34 r=1,Edge36 r=1,Edge37 r=1]
FEATURE [Sketcher::SketchObject] Sketch047
  ArcFitTolerance = 0
  FullyConstrained = true
  MakeInternals = false
  sketch-geometry (24):
    g0: LineSegment StartX=0 StartY=0 StartZ=0 EndX=8 EndY=2e-16 EndZ=0
    g1: LineSegment StartX=12 StartY=0 StartZ=0 EndX=28 EndY=2e-16 EndZ=0
    g2: LineSegment StartX=0 StartY=0 StartZ=0 EndX=-4e-16 EndY=8 EndZ=0
    g3: LineSegment StartX=1e-16 StartY=52 StartZ=0 EndX=0 EndY=60 EndZ=0
    g4: LineSegment StartX=0 StartY=60 StartZ=0 EndX=8 EndY=60 EndZ=0
    g5: LineSegment StartX=12 StartY=60 StartZ=0 EndX=28 EndY=60 EndZ=0
    g6: LineSegment StartX=32 StartY=60 StartZ=0 EndX=40 EndY=60 EndZ=0
    g7: LineSegment StartX=40 StartY=60 StartZ=0 EndX=40 EndY=52 EndZ=0
    g8: LineSegment StartX=40 StartY=48 StartZ=0 EndX=40 EndY=32 EndZ=0
    g9: LineSegment StartX=40 StartY=28 StartZ=0 EndX=40 EndY=12 EndZ=0
    g10: LineSegment StartX=40 StartY=8 StartZ=0 EndX=40 EndY=0 EndZ=0
    g11: LineSegment StartX=40 StartY=0 StartZ=0 EndX=32 EndY=-5e-16 EndZ=0
    g12: LineSegment StartX=-4e-16 StartY=48 StartZ=0 EndX=6e-16 EndY=32 EndZ=0
    g13: LineSegment StartX=-4e-16 StartY=28 StartZ=0 EndX=1e-16 EndY=12 EndZ=0
    g14: ArcOfCircle CenterX=10 CenterY=0 CenterZ=0 NormalX=0 NormalY=0 NormalZ=1 AngleXU=0 Radius=2 StartAngle=0 EndAngle=3.14159
    g15: ArcOfCircle CenterX=30 CenterY=0 CenterZ=0 NormalX=0 NormalY=0 NormalZ=1 AngleXU=0 Radius=2 StartAngle=3.14159 EndAngle=6.28319
    g16: ArcOfCircle CenterX=0 CenterY=10 CenterZ=0 NormalX=0 NormalY=0 NormalZ=1 AngleXU=0 Radius=2 StartAngle=1.5708 EndAngle=4.71239
    g17: ArcOfCircle CenterX=0 CenterY=30 CenterZ=0 NormalX=0 NormalY=0 NormalZ=1 AngleXU=0 Radius=2 StartAngle=4.71239 EndAngle=7.85398
    g18: ArcOfCircle CenterX=0 CenterY=50 CenterZ=0 NormalX=0 NormalY=0 NormalZ=1 AngleXU=0 Radius=2 StartAngle=1.5708 EndAngle=4.71239
    g19: ArcOfCircle CenterX=10 CenterY=60 CenterZ=0 NormalX=0 NormalY=0 NormalZ=1 AngleXU=0 Radius=2 StartAngle=3.14159 EndAngle=6.28319
    g20: ArcOfCircle CenterX=30 CenterY=60 CenterZ=0 NormalX=0 NormalY=0 NormalZ=1 AngleXU=0 Radius=2 StartAngle=4e-16 EndAngle=3.14159
    g21: ArcOfCircle CenterX=40 CenterY=50 CenterZ=0 NormalX=0 NormalY=0 NormalZ=1 AngleXU=0 Radius=2 StartAngle=1.5708 EndAngle=4.71239
    g22: ArcOfCircle CenterX=40 CenterY=30 CenterZ=0 NormalX=0 NormalY=0 NormalZ=1 AngleXU=0 Radius=2 StartAngle=4.71239 EndAngle=7.85398
    g23: ArcOfCircle CenterX=40 CenterY=10 CenterZ=0 NormalX=0 NormalY=0 NormalZ=1 AngleXU=0 Radius=2 StartAngle=1.5708 EndAngle=4.71239
  constraints (81):
    c: Coincident(g0,g-1)
    c: PointOnObject(g0,g-1)
    c: PointOnObject(g1,g-1)
    c: PointOnObject(g1,g-1)
    c: Coincident(g2,g0)
    c: PointOnObject(g2,g-2)
    c: PointOnObject(g3,g-2)
    c: PointOnObject(g3,g-2)
    c: Coincident(g4,g3)
    c: Horizontal(g4)
    c: Horizontal(g5)
    c: Coincident(g7,g6)
    c: Vertical(g7)
    c: Vertical(g8)
    c: Vertical(g9)
    c: PointOnObject(g10,g-1)
    c: Coincident(g11,g10)
    c: PointOnObject(g11,g-1)
    c: PointOnObject(g12,g-2)
    c: PointOnObject(g12,g-2)
    c: PointOnObject(g13,g-2)
    c: PointOnObject(g13,g-2)
    c: Distance(g0) = 8
    c: Coincident(g14,g0)
    c: Coincident(g14,g1)
    c: Diameter(g14) = 4
    c: Distance(g1) = 16
    c: Coincident(g15,g1)
    c: Coincident(g15,g11)
    c: Diameter(g15) = 4
    c: PointOnObject(g15,g-1)
    c: Distance(g11) = 8
    c: Vertical(g10)
    c: Distance(g2) = 8
    c: Coincident(g16,g2)
    c: Coincident(g16,g13)
    c: PointOnObject(g16,g-2)
    c: Diameter(g16) = 4
    c: Distance(g13) = 16
    c: Distance(g12) = 16
    c: PointOnObject(g14,g-1)
    c: Coincident(g17,g13)
    c: Coincident(g17,g12)
    c: PointOnObject(g17,g-2)
    c: Diameter(g17) = 4
    c: Coincident(g18,g12)
    c: Coincident(g18,g3)
    c: PointOnObject(g18,g-2)
    c: Diameter(g18) = 4
    c: Distance(g3) = 8
    c: Distance(g4) = 8
    c: Coincident(g19,g4)
    c: Coincident(g19,g5)
    c: Distance(g19,g-1) = 60
    c: Diameter(g19) = 4
    c: Distance(g5) = 16
    c: Distance(g3,g5) = 12
    c: Coincident(g20,g5)
    c: Coincident(g20,g6)
    c: Distance(g20,g-1) = 60
    c: Diameter(g20) = 4
    c: Distance(g6,g-1) = 60
    c: Horizontal(g6)
    c: Distance(g6) = 8
    c: Distance(g7) = 8
    c: Coincident(g21,g7)
    c: Coincident(g21,g8)
    c: Distance(g18,g21) = 40
    c: Distance(g8) = 16
    c: Diameter(g21) = 4
    c: Distance(g8,g-2) = 40
    c: Distance(g9) = 16
    c: Distance(g9,g-2) = 40
    c: Coincident(g22,g8)
    c: Coincident(g22,g9)
    c: Diameter(g22) = 4
    c: Distance(g22,g17) = 40
    c: Coincident(g23,g9)
    c: Coincident(g23,g10)
    c: Diameter(g23) = 4
    c: Distance(g16,g23) = 40
FEATURE [Part::Extrusion] Extrude045
  Base = -> Sketch047
  Dir = (0,0,1)
  DirMode = 2
  FaceMakerClass = Part::FaceMakerBullseye
  FaceMakerMode = 3
  LengthFwd = 5
  LengthRev = 0
  Placement = pos=(-17,-11,-6) rot=(-0.57735,-0.57735,0.57735;4.18879rad)
  Solid = true
  Symmetric = false
FEATURE [Part::Cut] Cut061  label="Base_cut001"
  Base = -> Fillet039
  Refine = true
  Tool = -> Extrude045
FEATURE [Sketcher::SketchObject] Sketch048
  ArcFitTolerance = 0
  FullyConstrained = true
  MakeInternals = false
  sketch-geometry (29):
    g0: LineSegment StartX=0 StartY=0 StartZ=0 EndX=8 EndY=2e-16 EndZ=0
    g1: LineSegment StartX=12 StartY=0 StartZ=0 EndX=28 EndY=2e-16 EndZ=0
    g2: LineSegment StartX=0 StartY=0 StartZ=0 EndX=-4e-16 EndY=8 EndZ=0
    g3: LineSegment StartX=1e-16 StartY=52 StartZ=0 EndX=0 EndY=60 EndZ=0
    g4: LineSegment StartX=0 StartY=60 StartZ=0 EndX=8 EndY=60 EndZ=0
    g5: LineSegment StartX=12 StartY=60 StartZ=0 EndX=28 EndY=60 EndZ=0
    g6: LineSegment StartX=32 StartY=60 StartZ=0 EndX=40 EndY=60 EndZ=0
    g7: LineSegment StartX=40 StartY=60 StartZ=0 EndX=40 EndY=52 EndZ=0
    g8: LineSegment StartX=40 StartY=48 StartZ=0 EndX=40 EndY=32 EndZ=0
    g9: LineSegment StartX=40 StartY=28 StartZ=0 EndX=40 EndY=12 EndZ=0
    g10: LineSegment StartX=40 StartY=8 StartZ=0 EndX=40 EndY=0 EndZ=0
    g11: LineSegment StartX=40 StartY=0 StartZ=0 EndX=32 EndY=-5e-16 EndZ=0
    g12: LineSegment StartX=-4e-16 StartY=48 StartZ=0 EndX=6e-16 EndY=32 EndZ=0
    g13: LineSegment StartX=-4e-16 StartY=28 StartZ=0 EndX=1e-16 EndY=12 EndZ=0
    g14: ArcOfCircle CenterX=10 CenterY=0 CenterZ=0 NormalX=0 NormalY=0 NormalZ=1 AngleXU=0 Radius=2 StartAngle=0 EndAngle=3.14159
    g15: ArcOfCircle CenterX=30 CenterY=0 CenterZ=0 NormalX=0 NormalY=0 NormalZ=1 AngleXU=0 Radius=2 StartAngle=3.14159 EndAngle=6.28319
    g16: ArcOfCircle CenterX=0 CenterY=10 CenterZ=0 NormalX=0 NormalY=0 NormalZ=1 AngleXU=0 Radius=2 StartAngle=1.5708 EndAngle=4.71239
    g17: ArcOfCircle CenterX=0 CenterY=30 CenterZ=0 NormalX=0 NormalY=0 NormalZ=1 AngleXU=0 Radius=2 StartAngle=4.71239 EndAngle=7.85398
    g18: ArcOfCircle CenterX=0 CenterY=50 CenterZ=0 NormalX=0 NormalY=0 NormalZ=1 AngleXU=0 Radius=2 StartAngle=1.5708 EndAngle=4.71239
    g19: ArcOfCircle CenterX=10 CenterY=60 CenterZ=0 NormalX=0 NormalY=0 NormalZ=1 AngleXU=0 Radius=2 StartAngle=3.14159 EndAngle=6.28319
    g20: ArcOfCircle CenterX=30 CenterY=60 CenterZ=0 NormalX=0 NormalY=0 NormalZ=1 AngleXU=0 Radius=2 StartAngle=4e-16 EndAngle=3.14159
    g21: ArcOfCircle CenterX=40 CenterY=50 CenterZ=0 NormalX=0 NormalY=0 NormalZ=1 AngleXU=0 Radius=2 StartAngle=1.5708 EndAngle=4.71239
    g22: ArcOfCircle CenterX=40 CenterY=30 CenterZ=0 NormalX=0 NormalY=0 NormalZ=1 AngleXU=0 Radius=2 StartAngle=4.71239 EndAngle=7.85398
    g23: ArcOfCircle CenterX=40 CenterY=10 CenterZ=0 NormalX=0 NormalY=0 NormalZ=1 AngleXU=0 Radius=2 StartAngle=1.5708 EndAngle=4.71239
    g24: Circle CenterX=30 CenterY=0 CenterZ=0 NormalX=0 NormalY=0 NormalZ=1 AngleXU=0 Radius=1.1
    g25: Circle CenterX=40 CenterY=30 CenterZ=0 NormalX=0 NormalY=0 NormalZ=1 AngleXU=0 Radius=1.1
    g26: Circle CenterX=30 CenterY=60 CenterZ=0 NormalX=0 NormalY=0 NormalZ=1 AngleXU=0 Radius=1.1
    g27: Circle CenterX=0 CenterY=50 CenterZ=0 NormalX=0 NormalY=0 NormalZ=1 AngleXU=0 Radius=1.1
    g28: Circle CenterX=0 CenterY=10 CenterZ=0 NormalX=0 NormalY=0 NormalZ=1 AngleXU=0 Radius=1.1
  constraints (88):
    c: Coincident(g0,g-1)
    c: PointOnObject(g0,g-1)
    c: PointOnObject(g1,g-1)
    c: PointOnObject(g1,g-1)
    c: Coincident(g2,g0)
    c: PointOnObject(g2,g-2)
    c: PointOnObject(g3,g-2)
    c: PointOnObject(g3,g-2)
    c: Coincident(g4,g3)
    c: Horizontal(g4)
    c: Horizontal(g5)
    c: Coincident(g7,g6)
    c: Vertical(g7)
    c: Vertical(g8)
    c: Vertical(g9)
    c: PointOnObject(g10,g-1)
    c: Coincident(g11,g10)
    c: PointOnObject(g11,g-1)
    c: PointOnObject(g12,g-2)
    c: PointOnObject(g12,g-2)
    c: PointOnObject(g13,g-2)
    c: PointOnObject(g13,g-2)
    c: Distance(g0) = 8
    c: Coincident(g14,g0)
    c: Coincident(g14,g1)
    c: Diameter(g14) = 4
    c: Distance(g1) = 16
    c: Coincident(g15,g1)
    c: Coincident(g15,g11)
    c: Diameter(g15) = 4
    c: PointOnObject(g15,g-1)
    c: Distance(g11) = 8
    c: Vertical(g10)
    c: Distance(g2) = 8
    c: Coincident(g16,g2)
    c: Coincident(g16,g13)
    c: PointOnObject(g16,g-2)
    c: Diameter(g16) = 4
    c: Distance(g13) = 16
    c: Distance(g12) = 16
    c: PointOnObject(g14,g-1)
    c: Coincident(g17,g13)
    c: Coincident(g17,g12)
    c: PointOnObject(g17,g-2)
    c: Diameter(g17) = 4
    c: Coincident(g18,g12)
    c: Coincident(g18,g3)
    c: PointOnObject(g18,g-2)
    c: Diameter(g18) = 4
    c: Distance(g3) = 8
    c: Distance(g4) = 8
    c: Coincident(g19,g4)
    c: Coincident(g19,g5)
    c: Distance(g19,g-1) = 60
    c: Diameter(g19) = 4
    c: Distance(g5) = 16
    c: Distance(g3,g5) = 12
    c: Coincident(g20,g5)
    c: Coincident(g20,g6)
    c: Distance(g20,g-1) = 60
    c: Diameter(g20) = 4
    c: Distance(g6,g-1) = 60
    c: Horizontal(g6)
    c: Distance(g6) = 8
    c: Distance(g7) = 8
    c: Coincident(g21,g7)
    c: Coincident(g21,g8)
    c: Distance(g18,g21) = 40
    c: Distance(g8) = 16
    c: Diameter(g21) = 4
    c: Distance(g8,g-2) = 40
    c: Distance(g9) = 16
    c: Distance(g9,g-2) = 40
    c: Coincident(g22,g8)
    c: Coincident(g22,g9)
    c: Diameter(g22) = 4
    c: Distance(g22,g17) = 40
    c: Coincident(g23,g9)
    c: Coincident(g23,g10)
    c: Diameter(g23) = 4
    c: Distance(g16,g23) = 40
    c: Coincident(g24,g15)
    c: Coincident(g25,g22)
    c: Coincident(g26,g20)
    c: Coincident(g27,g18)
    c: Coincident(g28,g16)
    c: Equal(g24, g25-g28) x4
    c: Diameter(g24) = 2.2
FEATURE [Part::Extrusion] Extrude046
  Base = -> Sketch048
  Dir = (0,0,1)
  DirMode = 2
  FaceMakerClass = Part::FaceMakerBullseye
  FaceMakerMode = 3
  LengthFwd = 5
  LengthRev = 0
  Placement = pos=(-17,-11,-6) rot=(-0.57735,-0.57735,0.57735;4.18879rad)
  Solid = true
  Symmetric = false
FEATURE [Part::MultiFuse] Fusion076  label="Arduino_SSR_Hold001"
  Refine = true
  Shapes = -> [Cut061,Extrude046]
FEATURE [Part::Cut] Cut062  label="arduinoNano33Holder001"
  Base = -> Fusion076
  Tool = -> Cylinder092
FEATURE [App::Part] _069940101  label="6850961001"
  Group = -> [Part__Feature619]
  Origin = -> Origin112
FEATURE [App::Part] zx62_ab_5pa_31__v002  label="zx62-ab-5pa_31_ v002"
  Group = -> [_069940101]
  Origin = -> Origin113
  Placement = pos=(0,0,0) rot=(0,0.707107,0.707107;3.14159rad)
FEATURE [App::Part] _DComponents001  label="3DComponents001"
  Group = -> [LSM9DS1TR_LGA_24_3X3P5X1_STM_v002,zx62_ab_5pa_31__v002,Part__Feature620,Part__Feature621,IoT_Reser_Button_v002,RC0402FR_071KL001,Part__Feature697,BLM18EG101TN1D_v002,C0805C472KDRACTU_v006,C0805C472KDRACTU_v004,PMEG6020AELRX_v002,C0805C472KDRACTU_v005,Part__Feature714,NINA_B306_00B_00__3DModel_STEP_56544_v002]
  Origin = -> Origin141
FEATURE [App::Part] NANO33BLE_V2_0_v002  label="NANO33BLE_V2.0 v002"
  Group = -> [Part__Feature592,_DComponents001]
  Origin = -> Origin142
FEATURE [App::Part] Nano33BLE_v008  label="Nano33BLE v008"
  Group = -> [NANO33BLE_V2_0_v002]
  Origin = -> Origin143
  Placement = pos=(0,-8,0) rot=(0,0,1;0rad)
FEATURE [Part::Compound] Compound009  label="arduinoNano33"
  Links = -> [Cut062,Part024,Part023,Nano33BLE_v008,Origin144]
  Placement = pos=(85,105,0) rot=(0.57735,-0.57735,0.57735;2.0944rad)
FEATURE [Part::Fillet] Fillet034
  Base = -> Fusion051
  EdgeLinks = -> Fusion051 [Edge1,Edge2,Edge3,Edge4,Edge5,Edge7,Edge8,Edge9,Edge15,Edge16,Edge17,Edge18,Edge19,Edge21,Edge22,Edge23,Edge28,Edge29,Edge32,Edge33,Edge34,Edge36,Edge37]
  Edges = 23 edges: [Edge1 r=1,Edge2 r=2,Edge3 r=1,Edge4 r=1,Edge5 r=1,Edge7 r=2,Edge8 r=3,Edge9 r=1,Edge15 r=1,Edge16 r=1,Edge17 r=1,Edge18 r=3,Edge19 r=1,Edge21 r=1,Edge22 r=1,Edge23 r=1,Edge28 r=1,Edge29 r=1,Edge32 r=1,Edge33 r=1,Edge34 r=1,Edge36 r=1,Edge37 r=1]
FEATURE [Part::Extrusion] Extrude033
  Base = -> Sketch034
  Dir = (0,0,1)
  DirMode = 2
  FaceMakerClass = Part::FaceMakerBullseye
  FaceMakerMode = 3
  LengthFwd = 5
  LengthRev = 0
  Placement = pos=(-17,-11,-6) rot=(-0.57735,-0.57735,0.57735;4.18879rad)
  Solid = true
  Symmetric = false
FEATURE [Part::Cut] Cut049  label="Base_cut"
  Base = -> Fillet034
  Refine = true
  Tool = -> Extrude033
FEATURE [Sketcher::SketchObject] Sketch035
  ArcFitTolerance = 0
  FullyConstrained = true
  MakeInternals = false
  sketch-geometry (29):
    g0: LineSegment StartX=0 StartY=0 StartZ=0 EndX=8 EndY=2e-16 EndZ=0
    g1: LineSegment StartX=12 StartY=0 StartZ=0 EndX=28 EndY=2e-16 EndZ=0
    g2: LineSegment StartX=0 StartY=0 StartZ=0 EndX=-4e-16 EndY=8 EndZ=0
    g3: LineSegment StartX=1e-16 StartY=52 StartZ=0 EndX=0 EndY=60 EndZ=0
    g4: LineSegment StartX=0 StartY=60 StartZ=0 EndX=8 EndY=60 EndZ=0
    g5: LineSegment StartX=12 StartY=60 StartZ=0 EndX=28 EndY=60 EndZ=0
    g6: LineSegment StartX=32 StartY=60 StartZ=0 EndX=40 EndY=60 EndZ=0
    g7: LineSegment StartX=40 StartY=60 StartZ=0 EndX=40 EndY=52 EndZ=0
    g8: LineSegment StartX=40 StartY=48 StartZ=0 EndX=40 EndY=32 EndZ=0
    g9: LineSegment StartX=40 StartY=28 StartZ=0 EndX=40 EndY=12 EndZ=0
    g10: LineSegment StartX=40 StartY=8 StartZ=0 EndX=40 EndY=0 EndZ=0
    g11: LineSegment StartX=40 StartY=0 StartZ=0 EndX=32 EndY=-5e-16 EndZ=0
    g12: LineSegment StartX=-4e-16 StartY=48 StartZ=0 EndX=6e-16 EndY=32 EndZ=0
    g13: LineSegment StartX=-4e-16 StartY=28 StartZ=0 EndX=1e-16 EndY=12 EndZ=0
    g14: ArcOfCircle CenterX=10 CenterY=0 CenterZ=0 NormalX=0 NormalY=0 NormalZ=1 AngleXU=0 Radius=2 StartAngle=0 EndAngle=3.14159
    g15: ArcOfCircle CenterX=30 CenterY=0 CenterZ=0 NormalX=0 NormalY=0 NormalZ=1 AngleXU=0 Radius=2 StartAngle=3.14159 EndAngle=6.28319
    g16: ArcOfCircle CenterX=0 CenterY=10 CenterZ=0 NormalX=0 NormalY=0 NormalZ=1 AngleXU=0 Radius=2 StartAngle=1.5708 EndAngle=4.71239
    g17: ArcOfCircle CenterX=0 CenterY=30 CenterZ=0 NormalX=0 NormalY=0 NormalZ=1 AngleXU=0 Radius=2 StartAngle=4.71239 EndAngle=7.85398
    g18: ArcOfCircle CenterX=0 CenterY=50 CenterZ=0 NormalX=0 NormalY=0 NormalZ=1 AngleXU=0 Radius=2 StartAngle=1.5708 EndAngle=4.71239
    g19: ArcOfCircle CenterX=10 CenterY=60 CenterZ=0 NormalX=0 NormalY=0 NormalZ=1 AngleXU=0 Radius=2 StartAngle=3.14159 EndAngle=6.28319
    g20: ArcOfCircle CenterX=30 CenterY=60 CenterZ=0 NormalX=0 NormalY=0 NormalZ=1 AngleXU=0 Radius=2 StartAngle=4e-16 EndAngle=3.14159
    g21: ArcOfCircle CenterX=40 CenterY=50 CenterZ=0 NormalX=0 NormalY=0 NormalZ=1 AngleXU=0 Radius=2 StartAngle=1.5708 EndAngle=4.71239
    g22: ArcOfCircle CenterX=40 CenterY=30 CenterZ=0 NormalX=0 NormalY=0 NormalZ=1 AngleXU=0 Radius=2 StartAngle=4.71239 EndAngle=7.85398
    g23: ArcOfCircle CenterX=40 CenterY=10 CenterZ=0 NormalX=0 NormalY=0 NormalZ=1 AngleXU=0 Radius=2 StartAngle=1.5708 EndAngle=4.71239
    g24: Circle CenterX=30 CenterY=0 CenterZ=0 NormalX=0 NormalY=0 NormalZ=1 AngleXU=0 Radius=1
    g25: Circle CenterX=40 CenterY=30 CenterZ=0 NormalX=0 NormalY=0 NormalZ=1 AngleXU=0 Radius=1
    g26: Circle CenterX=30 CenterY=60 CenterZ=0 NormalX=0 NormalY=0 NormalZ=1 AngleXU=0 Radius=1
    g27: Circle CenterX=0 CenterY=50 CenterZ=0 NormalX=0 NormalY=0 NormalZ=1 AngleXU=0 Radius=1
    g28: Circle CenterX=0 CenterY=10 CenterZ=0 NormalX=0 NormalY=0 NormalZ=1 AngleXU=0 Radius=1
  constraints (88):
    c: Coincident(g0,g-1)
    c: PointOnObject(g0,g-1)
    c: PointOnObject(g1,g-1)
    c: PointOnObject(g1,g-1)
    c: Coincident(g2,g0)
    c: PointOnObject(g2,g-2)
    c: PointOnObject(g3,g-2)
    c: PointOnObject(g3,g-2)
    c: Coincident(g4,g3)
    c: Horizontal(g4)
    c: Horizontal(g5)
    c: Coincident(g7,g6)
    c: Vertical(g7)
    c: Vertical(g8)
    c: Vertical(g9)
    c: PointOnObject(g10,g-1)
    c: Coincident(g11,g10)
    c: PointOnObject(g11,g-1)
    c: PointOnObject(g12,g-2)
    c: PointOnObject(g12,g-2)
    c: PointOnObject(g13,g-2)
    c: PointOnObject(g13,g-2)
    c: Distance(g0) = 8
    c: Coincident(g14,g0)
    c: Coincident(g14,g1)
    c: Diameter(g14) = 4
    c: Distance(g1) = 16
    c: Coincident(g15,g1)
    c: Coincident(g15,g11)
    c: Diameter(g15) = 4
    c: PointOnObject(g15,g-1)
    c: Distance(g11) = 8
    c: Vertical(g10)
    c: Distance(g2) = 8
    c: Coincident(g16,g2)
    c: Coincident(g16,g13)
    c: PointOnObject(g16,g-2)
    c: Diameter(g16) = 4
    c: Distance(g13) = 16
    c: Distance(g12) = 16
    c: PointOnObject(g14,g-1)
    c: Coincident(g17,g13)
    c: Coincident(g17,g12)
    c: PointOnObject(g17,g-2)
    c: Diameter(g17) = 4
    c: Coincident(g18,g12)
    c: Coincident(g18,g3)
    c: PointOnObject(g18,g-2)
    c: Diameter(g18) = 4
    c: Distance(g3) = 8
    c: Distance(g4) = 8
    c: Coincident(g19,g4)
    c: Coincident(g19,g5)
    c: Distance(g19,g-1) = 60
    c: Diameter(g19) = 4
    c: Distance(g5) = 16
    c: Distance(g3,g5) = 12
    c: Coincident(g20,g5)
    c: Coincident(g20,g6)
    c: Distance(g20,g-1) = 60
    c: Diameter(g20) = 4
    c: Distance(g6,g-1) = 60
    c: Horizontal(g6)
    c: Distance(g6) = 8
    c: Distance(g7) = 8
    c: Coincident(g21,g7)
    c: Coincident(g21,g8)
    c: Distance(g18,g21) = 40
    c: Distance(g8) = 16
    c: Diameter(g21) = 4
    c: Distance(g8,g-2) = 40
    c: Distance(g9) = 16
    c: Distance(g9,g-2) = 40
    c: Coincident(g22,g8)
    c: Coincident(g22,g9)
    c: Diameter(g22) = 4
    c: Distance(g22,g17) = 40
    c: Coincident(g23,g9)
    c: Coincident(g23,g10)
    c: Diameter(g23) = 4
    c: Distance(g16,g23) = 40
    c: Coincident(g24,g15)
    c: Coincident(g25,g22)
    c: Coincident(g26,g20)
    c: Coincident(g27,g18)
    c: Coincident(g28,g16)
    c: Equal(g24, g25-g28) x4
    c: Diameter(g24) = 2
FEATURE [Part::Extrusion] Extrude034
  Base = -> Sketch035
  Dir = (0,0,1)
  DirMode = 2
  FaceMakerClass = Part::FaceMakerBullseye
  FaceMakerMode = 3
  LengthFwd = 5
  LengthRev = 0
  Placement = pos=(-17,-11,-6) rot=(-0.57735,-0.57735,0.57735;4.18879rad)
  Solid = true
  Symmetric = false
FEATURE [Part::MultiFuse] Fusion052  label="Arduino_SSR_Hold"
  Refine = true
  Shapes = -> [Cut049,Extrude034]
FEATURE [Part::Box] Box094  label="PCB"
  AttacherType = Attacher::AttachEngine3D
  Height = 107
  Length = 1.5
  Width = 42
FEATURE [Part::Box] Box095  label="Cube065"
  AttacherType = Attacher::AttachEngine3D
  Height = 7
  Length = 10
  Placement = pos=(-10,3.75,8) rot=(0,0,1;0rad)
  Width = 0.5
FEATURE [Part::Box] Box096  label="Cube066"
  AttacherType = Attacher::AttachEngine3D
  Height = 7
  Length = 10
  Placement = pos=(-10,10.75,8) rot=(0,0,1;0rad)
  Width = 0.5
FEATURE [Part::Box] Box097  label="Cube067"
  AttacherType = Attacher::AttachEngine3D
  Height = 7
  Length = 10
  Placement = pos=(-10,3.75,92) rot=(0,0,1;0rad)
  Width = 0.5
FEATURE [Part::Box] Box098  label="Cube068"
  AttacherType = Attacher::AttachEngine3D
  Height = 7
  Length = 10
  Placement = pos=(-10,10.75,92) rot=(0,0,1;0rad)
  Width = 0.5
FEATURE [Part::Box] Box099  label="baseMOunt"
  AttacherType = Attacher::AttachEngine3D
  Height = 64
  Length = 6
  Placement = pos=(106.75,-4,-12) rot=(0,0,1;0rad)
  Width = 21
FEATURE [Part::Box] Box100  label="Cube069"
  AttacherType = Attacher::AttachEngine3D
  Height = 8.9
  Length = 8.2
  Placement = pos=(3.8,15,53.1) rot=(0,0,1;0rad)
  Width = 7
FEATURE [Part::Box] Box101  label="baseMOunt001"
  AttacherType = Attacher::AttachEngine3D
  Height = 23
  Length = 6
  Placement = pos=(106.75,0,9.5) rot=(0,0,1;0rad)
  Width = 17
FEATURE [Part::Box] Box102  label="Cube070"
  AttacherType = Attacher::AttachEngine3D
  Height = 21
  Length = 2
  Placement = pos=(12,15,53.1) rot=(0,0,1;0rad)
  Width = 7
FEATURE [Part::Box] Box103  label="Cube071"
  AttacherType = Attacher::AttachEngine3D
  Height = 4
  Length = 15
  Placement = pos=(66.5,-0.9,22.75) rot=(0,0,1;0rad)
  Width = 6
FEATURE [Part::Cut] Cut064  label="BaseMount"
  Base = -> Box099
  Placement = pos=(0,-10,0) rot=(0,0,1;0rad)
  Refine = true
  Tool = -> Box101
FEATURE [Part::Cylinder] Cylinder093  label="Tube013"
  Angle = 360
  AttacherType = Attacher::AttachEngine3D
  FirstAngle = 0
  Height = 67
  Placement = pos=(-7.5,7.5,20) rot=(0,0,1;0rad)
  Radius = 5
  SecondAngle = 0
FEATURE [Part::Cylinder] Cylinder094  label="cap1"
  Angle = 360
  AttacherType = Attacher::AttachEngine3D
  FirstAngle = 0
  Height = 9.82
  Placement = pos=(-1.15e-14,27,45) rot=(0,1,0;4.71239rad)
  Radius = 5.93
  SecondAngle = 0
FEATURE [Part::Cylinder] Cylinder095  label="cap2"
  Angle = 360
  AttacherType = Attacher::AttachEngine3D
  FirstAngle = 0
  Height = 11.56
  Placement = pos=(-1.15e-14,35.52,75) rot=(0,1,0;4.71239rad)
  Radius = 4.175
  SecondAngle = 0
FEATURE [Part::Cylinder] Cylinder096  label="Tube001"
  Angle = 360
  AttacherType = Attacher::AttachEngine3D
  FirstAngle = 0
  Height = 6.35
  Placement = pos=(-7.5,7.5,9.65) rot=(0,0,1;0rad)
  Radius = 3
  SecondAngle = 0
FEATURE [Part::Cylinder] Cylinder097  label="Tube002"
  Angle = 360
  AttacherType = Attacher::AttachEngine3D
  FirstAngle = 0
  Height = 6.35
  Placement = pos=(-7.5,7.5,9.65) rot=(0,0,1;0rad)
  Radius = 3
  SecondAngle = 0
FEATURE [Part::Cylinder] Cylinder098
  Angle = 360
  AttacherType = Attacher::AttachEngine3D
  FirstAngle = 0
  Height = 10
  Placement = pos=(5,3,3) rot=(0,1,0;4.71239rad)
  Radius = 1.6
  SecondAngle = 0
FEATURE [Part::Cylinder] Cylinder099
  Angle = 360
  AttacherType = Attacher::AttachEngine3D
  FirstAngle = 0
  Height = 10
  Placement = pos=(5,39,3) rot=(0,1,0;4.71239rad)
  Radius = 1.6
  SecondAngle = 0
FEATURE [Part::Cylinder] Cylinder100
  Angle = 360
  AttacherType = Attacher::AttachEngine3D
  FirstAngle = 0
  Height = 10
  Placement = pos=(5,3,104) rot=(0,1,0;4.71239rad)
  Radius = 1.6
  SecondAngle = 0
FEATURE [Part::Cylinder] Cylinder101
  Angle = 360
  AttacherType = Attacher::AttachEngine3D
  FirstAngle = 0
  Height = 10
  Placement = pos=(5,39,104) rot=(0,1,0;4.71239rad)
  Radius = 1.6
  SecondAngle = 0
FEATURE [Part::Cylinder] Cylinder102
  Angle = 360
  AttacherType = Attacher::AttachEngine3D
  FirstAngle = 0
  Height = 10
  Placement = pos=(114,6.5,-6) rot=(0,1,0;4.71239rad)
  Radius = 1.6
  SecondAngle = 0
FEATURE [Part::Cylinder] Cylinder103
  Angle = 360
  AttacherType = Attacher::AttachEngine3D
  FirstAngle = 0
  Height = 10
  Placement = pos=(114,6.5,46) rot=(0,1,0;4.71239rad)
  Radius = 1.6
  SecondAngle = 0
FEATURE [Part::Cylinder] Cylinder104
  Angle = 360
  AttacherType = Attacher::AttachEngine3D
  FirstAngle = 0
  Height = 21
  Placement = pos=(7,18.5,71) rot=(0,1,0;1.5708rad)
  Radius = 1.1
  SecondAngle = 0
FEATURE [Part::Cut] Cut068
  Base = -> Box102
  Refine = true
  Tool = -> Cylinder104
FEATURE [Part::MultiFuse] Fusion080  label="bottom_tubehold"
  Refine = true
  Shapes = -> [Box095,Box096]
FEATURE [Part::MultiFuse] Fusion081  label="top_tubehold"
  Refine = true
  Shapes = -> [Box097,Box098]
FEATURE [Part::MultiFuse] Fusion082  label="m3_cyl003"
  Refine = true
  Shapes = -> [Cylinder098,Cylinder099,Cylinder100,Cylinder101]
FEATURE [Part::Cut] Cut063  label="PCB_m3cut"
  Base = -> Box094
  Refine = true
  Tool = -> Fusion082
FEATURE [Part::Fillet] Fillet041  label="pcb"
  Base = -> Cut063
  EdgeLinks = -> Cut063 [Edge9,Edge12,Edge14]
  Edges = 3 edges r=3: [Edge9,Edge12,Edge14]
FEATURE [Part::MultiFuse] Fusion086  label="m3Cyl003"
  Placement = pos=(0,-10,0) rot=(0,0,1;0rad)
  Refine = true
  Shapes = -> [Cylinder102,Cylinder103]
FEATURE [Part::MultiFuse] Fusion088  label="Cap"
  Refine = true
  Shapes = -> [Box100,Cut068]
FEATURE [Part::Feature] Part__Feature808  label="pins"
  Placement = pos=(7.37732,-14.6706,0.356181) rot=(-1,0,0;1.5708rad)
  shape: bbox 0.64 x 0.64 x 8.5 mm, 12 faces (baked)
FEATURE [Part::Feature] Part__Feature809  label="pins001"
  Placement = pos=(7.37732,-14.6706,0.356181) rot=(-1,0,0;1.5708rad)
  shape: bbox 0.64 x 0.64 x 8.5 mm, 12 faces (baked)
FEATURE [Part::Feature] Part__Feature810  label="pins002"
  Placement = pos=(7.37732,-14.6706,0.356181) rot=(-1,0,0;1.5708rad)
  shape: bbox 0.64 x 0.64 x 8.5 mm, 12 faces (baked)
FEATURE [Part::Feature] Part__Feature811  label="SOLID"
  shape: bbox 9.98 x 5.7 x 7 mm, 38 faces (baked)
FEATURE [Part::Feature] Part__Feature812  label="BOSS-EXTRUDE14_2_"
  Placement = pos=(-3.0192,1.09628,5.395) rot=(0,0,1;0rad)
  shape: bbox 0.6 x 1 x 0.3 mm, 6 faces (baked)
FEATURE [Part::Feature] Part__Feature813  label="BOSS-EXTRUDE14_11_"
  Placement = pos=(-3.0192,1.09628,5.395) rot=(0,0,1;0rad)
  shape: bbox 0.3 x 1 x 0.3 mm, 6 faces (baked)
FEATURE [Part::Feature] Part__Feature814  label="BOSS-EXTRUDE7_7_"
  Placement = pos=(-3.0192,1.09628,5.395) rot=(0,0,1;0rad)
  shape: bbox 0.3 x 3.784 x 0.75 mm, 6 faces (baked)
FEATURE [Part::Feature] Part__Feature815  label="BOSS-EXTRUDE14_9_"
  Placement = pos=(-3.0192,1.09628,5.395) rot=(0,0,1;0rad)
  shape: bbox 0.3 x 1 x 0.3 mm, 6 faces (baked)
FEATURE [Part::Feature] Part__Feature816  label="switch"
  Placement = pos=(-2,36,30) rot=(-0.57735,0.57735,0.57735;2.0944rad)
  shape: bbox 3.5 x 9.656 x 8.5 mm, 169 faces (baked)
FEATURE [Part::Feature] Part__Feature817  label="BOSS-EXTRUDE14_8_"
  Placement = pos=(-3.0192,1.09628,5.395) rot=(0,0,1;0rad)
  shape: bbox 0.6 x 1 x 0.3 mm, 6 faces (baked)
FEATURE [Part::Feature] Part__Feature818  label="BOSS-EXTRUDE7_4_"
  Placement = pos=(-3.0192,1.09628,5.395) rot=(0,0,1;0rad)
  shape: bbox 0.3 x 3.784 x 0.75 mm, 6 faces (baked)
FEATURE [Part::Feature] Part__Feature819  label="BOSS-EXTRUDE7_3_"
  Placement = pos=(-3.0192,1.09628,5.395) rot=(0,0,1;0rad)
  shape: bbox 0.3 x 3.784 x 0.75 mm, 6 faces (baked)
FEATURE [Part::Feature] Part__Feature820  label="BOSS-EXTRUDE14_4_"
  Placement = pos=(-3.0192,1.09628,5.395) rot=(0,0,1;0rad)
  shape: bbox 0.3 x 1 x 0.3 mm, 6 faces (baked)
FEATURE [Part::Feature] Part__Feature821  label="BOSS-EXTRUDE14_3_"
  Placement = pos=(-3.0192,1.09628,5.395) rot=(0,0,1;0rad)
  shape: bbox 0.3 x 1 x 0.3 mm, 6 faces (baked)
FEATURE [Part::Feature] Part__Feature822  label="BOSS-EXTRUDE14_7_"
  Placement = pos=(-3.0192,1.09628,5.395) rot=(0,0,1;0rad)
  shape: bbox 0.6 x 1 x 0.3 mm, 6 faces (baked)
FEATURE [Part::Feature] Part__Feature823  label="MIRROR2"
  Placement = pos=(-3.0192,1.09628,5.395) rot=(0,0,1;0rad)
  shape: bbox 6.7 x 4.6 x 0.7 mm, 26 faces (baked)
FEATURE [Part::Feature] Part__Feature824  label="BOSS-EXTRUDE14_5_"
  Placement = pos=(-3.0192,1.09628,5.395) rot=(0,0,1;0rad)
  shape: bbox 0.3 x 1 x 0.3 mm, 6 faces (baked)
FEATURE [Part::Feature] Part__Feature825  label="BOSS-EXTRUDE14_12_"
  Placement = pos=(-3.0192,1.09628,5.395) rot=(0,0,1;0rad)
  shape: bbox 0.3 x 1 x 0.3 mm, 6 faces (baked)
FEATURE [Part::Feature] Part__Feature826  label="BOSS-EXTRUDE7_8_"
  Placement = pos=(-3.0192,1.09628,5.395) rot=(0,0,1;0rad)
  shape: bbox 0.3 x 3.784 x 0.75 mm, 6 faces (baked)
FEATURE [Part::Feature] Part__Feature827  label="BOSS-EXTRUDE7_1_"
  Placement = pos=(-3.0192,1.09628,5.395) rot=(0,0,1;0rad)
  shape: bbox 0.3 x 3.784 x 0.75 mm, 6 faces (baked)
FEATURE [Part::Feature] Part__Feature828  label="BOSS-EXTRUDE14_10_"
  Placement = pos=(-3.0192,1.09628,5.395) rot=(0,0,1;0rad)
  shape: bbox 0.3 x 1 x 0.3 mm, 6 faces (baked)
FEATURE [Part::Feature] Part__Feature829  label="BOSS-EXTRUDE7_9_"
  Placement = pos=(-3.0192,1.09628,5.395) rot=(0,0,1;0rad)
  shape: bbox 0.3 x 3.784 x 0.75 mm, 6 faces (baked)
FEATURE [Part::Feature] Part__Feature830  label="BOSS-EXTRUDE14_6_"
  Placement = pos=(-3.0192,1.09628,5.395) rot=(0,0,1;0rad)
  shape: bbox 0.6 x 1 x 0.3 mm, 6 faces (baked)
FEATURE [Part::Feature] Part__Feature831  label="CHAMFER9"
  Placement = pos=(-3.0192,1.09628,5.395) rot=(0,0,1;0rad)
  shape: bbox 8.94 x 7.3 x 4.2 mm, 103 faces (baked)
FEATURE [Part::Feature] Part__Feature832  label="BOSS-EXTRUDE14_1_"
  Placement = pos=(-3.0192,1.09628,5.395) rot=(0,0,1;0rad)
  shape: bbox 0.3 x 1 x 0.3 mm, 6 faces (baked)
FEATURE [Part::Feature] Part__Feature833  label="BOSS-EXTRUDE7_6_"
  Placement = pos=(-3.0192,1.09628,5.395) rot=(0,0,1;0rad)
  shape: bbox 0.3 x 3.784 x 0.75 mm, 6 faces (baked)
FEATURE [Part::Feature] Part__Feature834  label="BOSS-EXTRUDE7_2_"
  Placement = pos=(-3.0192,1.09628,5.395) rot=(0,0,1;0rad)
  shape: bbox 0.3 x 3.784 x 0.75 mm, 6 faces (baked)
FEATURE [Part::Feature] Part__Feature835  label="CUT-EXTRUDE5"
  Placement = pos=(-3.0192,1.09628,5.395) rot=(0,0,1;0rad)
  shape: bbox 8.867 x 2 x 3.668 mm, 129 faces (baked)
FEATURE [Part::Feature] Part__Feature836  label="BOSS-EXTRUDE7_5_"
  Placement = pos=(-3.0192,1.09628,5.395) rot=(0,0,1;0rad)
  shape: bbox 0.3 x 3.784 x 0.75 mm, 6 faces (baked)
FEATURE [Part::Feature] Part__Feature837  label="Shield"
  shape: bbox 10.6 x 2.7 x 12.6 mm, 38 faces (baked)
FEATURE [Part::Feature] Part__Feature838  label="Body008"
  Placement = pos=(0,0,0.1) rot=(0,0,1;0rad)
  shape: bbox 2.6 x 1.6 x 0.6302 mm, 6 faces (baked)
FEATURE [Part::Feature] Part__Feature839  label="Pins"
  shape: bbox 0.4402 x 0.4402 x 0.1002 mm, 6 faces (baked)
FEATURE [Part::Feature] Part__Feature840  label="Pins001"
  shape: bbox 0.44 x 0.44 x 0.1 mm, 6 faces (baked)
FEATURE [Part::Feature] Part__Feature841  label="Pins002"
  shape: bbox 0.44 x 0.44 x 0.1 mm, 6 faces (baked)
FEATURE [Part::Feature] Part__Feature842  label="Pins003"
  shape: bbox 0.44 x 0.44 x 0.1 mm, 6 faces (baked)
FEATURE [Part::Feature] Part__Feature843  label="Body009"
  Placement = pos=(0,0,0.1) rot=(0,0,1;0rad)
  shape: bbox 2.6 x 1.6 x 0.6302 mm, 6 faces (baked)
FEATURE [Part::Feature] Part__Feature844  label="Pins005"
  shape: bbox 0.44 x 0.44 x 0.1 mm, 6 faces (baked)
FEATURE [Part::Feature] Part__Feature845  label="Pins006"
  shape: bbox 0.44 x 0.44 x 0.1 mm, 6 faces (baked)
FEATURE [Part::Feature] Part__Feature846  label="Pins007"
  shape: bbox 0.4402 x 0.4402 x 0.1002 mm, 6 faces (baked)
FEATURE [Part::Feature] Part__Feature847  label="Pins008"
  shape: bbox 0.44 x 0.44 x 0.1 mm, 6 faces (baked)
FEATURE [Part::Feature] Part__Feature848  label="U.FL-R-SMT-1_10_ v1"
  Placement = pos=(-6.95174,1,-10.8381) rot=(-1,0,0;1.5708rad)
  shape: bbox 3.002 x 1.252 x 3.102 mm, 67 faces (baked)
FEATURE [Part::Feature] Part__Feature849  label="SOLID001"
  shape: bbox 20.96 x 1.25 x 17.78 mm, 345 faces (baked)
FEATURE [Part::Feature] Part__Feature850  label="1_Male_Pin_2.54_mm"
  Placement = pos=(3.87631,2.25619,11.0637) rot=(0,0,1;0rad)
  shape: bbox 2.54 x 11.1 x 2.4 mm, 32 faces (baked)
FEATURE [Part::Feature] Part__Feature851  label="1_Male_Pin_2.54_mm001"
  Placement = pos=(1.33631,2.25619,11.0637) rot=(0,0,1;0rad)
  shape: bbox 2.54 x 11.1 x 2.4 mm, 32 faces (baked)
FEATURE [Part::Feature] Part__Feature852  label="1_Male_Pin_2.54_mm002"
  Placement = pos=(-1.20369,2.25619,11.0637) rot=(0,0,1;0rad)
  shape: bbox 2.54 x 11.1 x 2.4 mm, 32 faces (baked)
FEATURE [Part::Feature] Part__Feature853  label="1_Male_Pin_2.54_mm003"
  Placement = pos=(-3.74369,2.25619,11.0637) rot=(0,0,1;0rad)
  shape: bbox 2.54 x 11.1 x 2.4 mm, 32 faces (baked)
FEATURE [Part::Feature] Part__Feature854  label="1_Male_Pin_2.54_mm004"
  Placement = pos=(-6.28369,2.25619,11.0637) rot=(0,0,1;0rad)
  shape: bbox 2.54 x 11.1 x 2.4 mm, 32 faces (baked)
FEATURE [Part::Feature] Part__Feature855  label="1_Male_Pin_2.54_mm005"
  Placement = pos=(-8.82369,2.25619,11.0637) rot=(0,0,1;0rad)
  shape: bbox 2.54 x 11.1 x 2.4 mm, 32 faces (baked)
FEATURE [Part::Feature] Part__Feature856  label="1_Male_Pin_2.54_mm006"
  Placement = pos=(-11.3637,2.25619,11.0637) rot=(0,0,1;0rad)
  shape: bbox 2.54 x 11.1 x 2.4 mm, 32 faces (baked)
FEATURE [Part::Feature] Part__Feature857  label="1_Male_Pin_2.54_mm007"
  Placement = pos=(3.87631,2.25619,11.0637) rot=(0,0,1;0rad)
  shape: bbox 2.54 x 11.1 x 2.4 mm, 32 faces (baked)
FEATURE [Part::Feature] Part__Feature858  label="1_Male_Pin_2.54_mm008"
  Placement = pos=(1.33631,2.25619,11.0637) rot=(0,0,1;0rad)
  shape: bbox 2.54 x 11.1 x 2.4 mm, 32 faces (baked)
FEATURE [Part::Feature] Part__Feature859  label="1_Male_Pin_2.54_mm009"
  Placement = pos=(-1.20369,2.25619,11.0637) rot=(0,0,1;0rad)
  shape: bbox 2.54 x 11.1 x 2.4 mm, 32 faces (baked)
FEATURE [Part::Feature] Part__Feature860  label="1_Male_Pin_2.54_mm010"
  Placement = pos=(-3.74369,2.25619,11.0637) rot=(0,0,1;0rad)
  shape: bbox 2.54 x 11.1 x 2.4 mm, 32 faces (baked)
FEATURE [Part::Feature] Part__Feature861  label="1_Male_Pin_2.54_mm011"
  Placement = pos=(-6.28369,2.25619,11.0637) rot=(0,0,1;0rad)
  shape: bbox 2.54 x 11.1 x 2.4 mm, 32 faces (baked)
FEATURE [Part::Feature] Part__Feature862  label="1_Male_Pin_2.54_mm012"
  Placement = pos=(-8.82369,2.25619,11.0637) rot=(0,0,1;0rad)
  shape: bbox 2.54 x 11.1 x 2.4 mm, 32 faces (baked)
FEATURE [Part::Feature] Part__Feature863  label="1_Male_Pin_2.54_mm013"
  Placement = pos=(-11.3637,2.25619,11.0637) rot=(0,0,1;0rad)
  shape: bbox 2.54 x 11.1 x 2.4 mm, 32 faces (baked)
FEATURE [Part::Feature] Part__Feature056  label="2069940100003"
  shape: bbox 15.41 x 6.405 x 0.215 mm, 9 faces (baked)
FEATURE [Part::Feature] Part__Feature057  label="2069940100001001"
  shape: bbox 101.4 x 3.017 x 2.167 mm, 204 faces (baked)
FEATURE [Part::Feature] Part__Feature864  label="USB C -C0046"
  Placement = pos=(6.7,20.1,32) rot=(-0.57735,0.57735,0.57735;2.0944rad)
  shape: bbox 6.63 x 11.9 x 40.53 mm, 28 faces (baked)
FEATURE [App::Part] Pins  label="Pins004"
  Group = -> [Part__Feature839,Part__Feature840,Part__Feature841,Part__Feature842]
  Origin = -> Origin151
FEATURE [App::Part] Pins001  label="Pins009"
  Group = -> [Part__Feature844,Part__Feature845,Part__Feature846,Part__Feature847]
  Origin = -> Origin153
FEATURE [App::Part] SKTAAAE010_v002  label="SKTAAAE010 v002"
  Group = -> [Part__Feature843,Pins001]
  Origin = -> Origin154
  Placement = pos=(10.6911,1,-0.186818) rot=(-1,0,0;1.5708rad)
FEATURE [App::Part] SKTAAAE010_v1  label="SKTAAAE010 v1"
  Group = -> [Part__Feature838,Pins]
  Origin = -> Origin152
  Placement = pos=(10.7092,1,-12.0449) rot=(-1,0,0;1.5708rad)
FEATURE [Sketcher::SketchObject] Sketch049
  ArcFitTolerance = 1e-06
  FullyConstrained = true
  MakeInternals = false
  Placement = pos=(0,0,0) rot=(0.57735,0.57735,0.57735;2.0944rad)
  sketch-geometry (8):
    g0: LineSegment StartX=0 StartY=0 StartZ=0 EndX=106.75 EndY=0 EndZ=0
    g1: LineSegment StartX=106.75 StartY=0 StartZ=0 EndX=106.75 EndY=41.75 EndZ=0
    g2: LineSegment StartX=106.75 StartY=41.75 StartZ=0 EndX=0 EndY=41.75 EndZ=0
    g3: LineSegment StartX=0 StartY=41.75 StartZ=0 EndX=0 EndY=0 EndZ=0
    g4: Circle CenterX=3 CenterY=3 CenterZ=0 NormalX=0 NormalY=0 NormalZ=1 AngleXU=0 Radius=1.625
    g5: Circle CenterX=3 CenterY=38.75 CenterZ=0 NormalX=0 NormalY=0 NormalZ=1 AngleXU=0 Radius=1.625
    g6: Circle CenterX=103.75 CenterY=38.75 CenterZ=0 NormalX=0 NormalY=0 NormalZ=1 AngleXU=0 Radius=1.625
    g7: Circle CenterX=103.75 CenterY=3 CenterZ=0 NormalX=0 NormalY=0 NormalZ=1 AngleXU=0 Radius=1.625
  constraints (23):
    c: Coincident(g0,g1)
    c: Coincident(g1,g2)
    c: Coincident(g2,g3)
    c: Coincident(g3,g0)
    c: Horizontal(g0)
    c: Horizontal(g2)
    c: Vertical(g1)
    c: Vertical(g3)
    c: Coincident(g0,g-1)
    c: Distance(g3) = 41.75
    c: Distance(g0) = 106.75
    c: Distance(g4,g0) = 3
    c: Distance(g4,g-2) = 3
    c: Distance(g5,g-2) = 3
    c: Distance(g5,g-1) = 38.75
    c: Distance(g7,g-2) = 103.75
    c: Distance(g7,g-1) = 3
    c: Distance(g6,g-2) = 103.75
    c: Distance(g6,g-1) = 38.75
    c: Equal(g4,g5)
    c: Equal(g4,g6)
    c: Equal(g4,g7)
    c: Diameter(g4) = 3.25
FEATURE [Part::Extrusion] Extrude047  label="Bottom004"
  Base = -> Sketch049
  Dir = (1,0,0)
  DirMode = 2
  FaceMakerClass = Part::FaceMakerBullseye
  FaceMakerMode = 3
  LengthFwd = 8
  LengthRev = 0
  Placement = pos=(0,4,0) rot=(0,0,1;4.71239rad)
  Solid = true
  Symmetric = false
FEATURE [Part::MultiFuse] Fusion085  label="Mount"
  Refine = true
  Shapes = -> [Cut064,Extrude047]
FEATURE [Part::Cut] Cut065  label="Mount_m3Cut"
  Base = -> Fusion085
  Refine = true
  Tool = -> Fusion086
FEATURE [Sketcher::SketchObject] Sketch050
  ArcFitTolerance = 1e-06
  FullyConstrained = true
  MakeInternals = false
  Placement = pos=(0,0,0) rot=(0.57735,0.57735,0.57735;2.0944rad)
  sketch-geometry (12):
    g0: LineSegment StartX=106.25 StartY=0 StartZ=0 EndX=106.25 EndY=41.75 EndZ=0
    g1: LineSegment StartX=106.25 StartY=41.75 StartZ=0 EndX=0 EndY=41.75 EndZ=0
    g2: LineSegment StartX=3.8e-15 StartY=41.75 StartZ=0 EndX=3.8e-15 EndY=0 EndZ=0
    g3: Circle CenterX=3 CenterY=3 CenterZ=0 NormalX=0 NormalY=0 NormalZ=1 AngleXU=0 Radius=1.625
    g4: Circle CenterX=3 CenterY=38.75 CenterZ=0 NormalX=0 NormalY=0 NormalZ=1 AngleXU=0 Radius=1.625
    g5: Circle CenterX=103.75 CenterY=38.75 CenterZ=0 NormalX=0 NormalY=0 NormalZ=1 AngleXU=0 Radius=1.625
    g6: Circle CenterX=103.75 CenterY=3 CenterZ=0 NormalX=0 NormalY=0 NormalZ=1 AngleXU=0 Radius=1.625
    g7: LineSegment StartX=3.8e-15 StartY=0 StartZ=0 EndX=18.25 EndY=0 EndZ=0
    g8: LineSegment StartX=18.25 StartY=0 StartZ=0 EndX=18.25 EndY=15 EndZ=0
    g9: LineSegment StartX=18.25 StartY=15 StartZ=0 EndX=88 EndY=15 EndZ=0
    g10: LineSegment StartX=88 StartY=15 StartZ=0 EndX=88 EndY=0 EndZ=0
    g11: LineSegment StartX=88 StartY=0 StartZ=0 EndX=106.25 EndY=0 EndZ=0
  constraints (36):
    c: Coincident(g0,g1)
    c: Coincident(g1,g2)
    c: Horizontal(g1)
    c: Vertical(g0)
    c: Vertical(g2)
    c: Distance(g2) = 41.75
    c: Distance(g3,g-2) = 3
    c: Distance(g4,g-2) = 3
    c: Distance(g4,g-1) = 38.75
    c: Distance(g6,g-2) = 103.75
    c: Distance(g6,g-1) = 3
    c: Distance(g5,g-2) = 103.75
    c: Distance(g5,g-1) = 38.75
    c: Equal(g3,g4)
    c: Equal(g3,g5)
    c: Equal(g3,g6)
    c: Diameter(g3) = 3.25
    c: Coincident(g7,g2)
    c: PointOnObject(g7,g-1)
    c: Horizontal(g7)
    c: Coincident(g8,g7)
    c: Vertical(g8)
    c: Coincident(g9,g8)
    c: Horizontal(g9)
    c: Coincident(g10,g9)
    c: PointOnObject(g10,g-1)
    c: Vertical(g10)
    c: Coincident(g11,g10)
    c: Coincident(g11,g0)
    c: Horizontal(g11)
    c: Distance(g7) = 18.25
    c: Distance(g3,g-1) = 3
    c: Distance(g8) = 15
    c: Distance(g11) = 18.25
    c: Distance(g0,g-2) = 106.25
    c: Distance(g1) = 106.25
FEATURE [Part::Extrusion] Extrude048  label="Top001"
  Base = -> Sketch050
  Dir = (1,0,0)
  DirMode = 2
  FaceMakerClass = Part::FaceMakerBullseye
  FaceMakerMode = 3
  LengthFwd = 4
  LengthRev = 0
  Placement = pos=(0,-15,0) rot=(0,0,1;4.71239rad)
  Solid = true
  Symmetric = false
FEATURE [Sketcher::SketchObject] Sketch051
  ArcFitTolerance = 1e-06
  FullyConstrained = true
  MakeInternals = false
  Placement = pos=(0,0,0) rot=(0.57735,0.57735,0.57735;2.0944rad)
  sketch-geometry (8):
    g0: Circle CenterX=3 CenterY=3 CenterZ=0 NormalX=0 NormalY=0 NormalZ=1 AngleXU=0 Radius=1.625
    g1: Circle CenterX=3 CenterY=38.75 CenterZ=0 NormalX=0 NormalY=0 NormalZ=1 AngleXU=0 Radius=1.625
    g2: Circle CenterX=103.75 CenterY=38.75 CenterZ=0 NormalX=0 NormalY=0 NormalZ=1 AngleXU=0 Radius=1.625
    g3: Circle CenterX=103.75 CenterY=3 CenterZ=0 NormalX=0 NormalY=0 NormalZ=1 AngleXU=0 Radius=1.625
    g4: Circle CenterX=3 CenterY=38.75 CenterZ=0 NormalX=0 NormalY=0 NormalZ=1 AngleXU=0 Radius=2.875
    g5: Circle CenterX=3 CenterY=3 CenterZ=0 NormalX=0 NormalY=0 NormalZ=1 AngleXU=0 Radius=2.875
    g6: Circle CenterX=103.75 CenterY=3 CenterZ=0 NormalX=0 NormalY=0 NormalZ=1 AngleXU=0 Radius=2.875
    g7: Circle CenterX=103.75 CenterY=38.75 CenterZ=0 NormalX=0 NormalY=0 NormalZ=1 AngleXU=0 Radius=2.875
  constraints (20):
    c: Distance(g0,g-2) = 3
    c: Distance(g1,g-2) = 3
    c: Distance(g1,g-1) = 38.75
    c: Distance(g3,g-2) = 103.75
    c: Distance(g3,g-1) = 3
    c: Distance(g2,g-2) = 103.75
    c: Distance(g2,g-1) = 38.75
    c: Equal(g0,g1)
    c: Equal(g0,g2)
    c: Equal(g0,g3)
    c: Diameter(g0) = 3.25
    c: Distance(g0,g-1) = 3
    c: Coincident(g4,g1)
    c: Coincident(g5,g0)
    c: Coincident(g6,g3)
    c: Coincident(g7,g2)
    c: Diameter(g7) = 5.75
    c: Diameter(g6) = 5.75
    c: Diameter(g5) = 5.75
    c: Diameter(g4) = 5.75
FEATURE [Part::Extrusion] Extrude049  label="spacer001"
  Base = -> Sketch051
  Dir = (1,0,0)
  DirMode = 2
  FaceMakerClass = Part::FaceMakerBullseye
  FaceMakerMode = 3
  LengthFwd = 13
  LengthRev = 0
  Placement = pos=(0,-2,0) rot=(0,0,1;4.71239rad)
  Solid = true
  Symmetric = false
FEATURE [Part::MultiFuse] Fusion077  label="topSpacer001"
  Refine = true
  Shapes = -> [Extrude048,Extrude049]
FEATURE [Part::Fillet] Fillet040  label="top_fillet001"
  Base = -> Fusion077
  EdgeLinks = -> Fusion077 [Edge1,Edge2,Edge9,Edge12,Edge37,Edge38,Edge39,Edge40]
  Edges = 8 edges r=1: [Edge1,Edge2,Edge9,Edge12,Edge37,Edge38,Edge39,Edge40]
FEATURE [App::Part] Part  label="GeigerTop001"
  Group = -> [Extrude048,Extrude049,Sketch051,Sketch050,Fusion077,Fillet040]
  Origin = -> Origin145
  Placement = pos=(-3,0,0) rot=(-0.57735,-0.57735,-0.57735;2.0944rad)
FEATURE [Sketcher::SketchObject] Sketch052
  ArcFitTolerance = 1e-06
  FullyConstrained = true
  MakeInternals = false
  Placement = pos=(0,0,0) rot=(0.57735,0.57735,0.57735;2.0944rad)
  sketch-geometry (4):
    g0: LineSegment StartX=14.5491 StartY=71.8507 StartZ=0 EndX=14.5491 EndY=52.2908 EndZ=0
    g1: LineSegment StartX=14.5491 StartY=52.2908 StartZ=0 EndX=22.4289 EndY=52.2908 EndZ=0
    g2: LineSegment StartX=22.4289 StartY=71.8507 StartZ=0 EndX=22.4289 EndY=52.2908 EndZ=0
    g3: LineSegment StartX=14.5491 StartY=71.8507 StartZ=0 EndX=22.4289 EndY=71.8507 EndZ=0
  constraints (11):
    c: Vertical(g0)
    c: Coincident(g1,g0)
    c: Horizontal(g1)
    c: Block(g1)
    c: Coincident(g2,g1)
    c: Vertical(g2)
    c: Coincident(g3,g0)
    c: Coincident(g3,g2)
    c: Horizontal(g3)
    c: Distance(g1) = 7.87986
    c: Block(g0)
FEATURE [App::Part] Part003  label="ESP_Cap"
  Group = -> [Sketch052,Box100,Box102,Cut068,Cylinder104,Fusion088]
  Origin = -> Origin159
FEATURE [Sketcher::SketchObject] Sketch053
  ArcFitTolerance = 1e-06
  FullyConstrained = true
  MakeInternals = false
  Placement = pos=(0,0,0) rot=(0.57735,0.57735,0.57735;2.0944rad)
  sketch-geometry (12):
    g0: LineSegment StartX=10.25 StartY=66.5 StartZ=0 EndX=10.25 EndY=43.25 EndZ=0
    g1: LineSegment StartX=30 StartY=43.25 StartZ=0 EndX=30 EndY=66.5 EndZ=0
    g2: LineSegment StartX=30 StartY=66.5 StartZ=0 EndX=10.25 EndY=66.5 EndZ=0
    g3: LineSegment StartX=10.25 StartY=43.25 StartZ=0 EndX=12.9 EndY=43.25 EndZ=0
    g4: LineSegment StartX=12.9 StartY=43.25 StartZ=0 EndX=12.9 EndY=20.25 EndZ=0
    g5: LineSegment StartX=12.9 StartY=20.25 StartZ=0 EndX=16.15 EndY=20.25 EndZ=0
    g6: LineSegment StartX=16.15 StartY=20.25 StartZ=0 EndX=16.15 EndY=15.25 EndZ=0
    g7: LineSegment StartX=16.15 StartY=15.25 StartZ=0 EndX=24.15 EndY=15.25 EndZ=0
    g8: LineSegment StartX=24.15 StartY=15.25 StartZ=0 EndX=24.15 EndY=20.25 EndZ=0
    g9: LineSegment StartX=24.15 StartY=20.25 StartZ=0 EndX=27.4 EndY=20.25 EndZ=0
    g10: LineSegment StartX=27.4 StartY=20.25 StartZ=0 EndX=27.4 EndY=43.25 EndZ=0
    g11: LineSegment StartX=27.4 StartY=43.25 StartZ=0 EndX=30 EndY=43.25 EndZ=0
  constraints (36):
    c: Coincident(g1,g2)
    c: Coincident(g2,g0)
    c: Vertical(g0)
    c: Vertical(g1)
    c: Horizontal(g2)
    c: Coincident(g3,g0)
    c: Horizontal(g3)
    c: Coincident(g4,g3)
    c: Vertical(g4)
    c: Coincident(g5,g4)
    c: Horizontal(g5)
    c: Coincident(g6,g5)
    c: Vertical(g6)
    c: Coincident(g7,g6)
    c: Horizontal(g7)
    c: Coincident(g8,g7)
    c: Vertical(g8)
    c: Coincident(g9,g8)
    c: Horizontal(g9)
    c: Coincident(g10,g9)
    c: Vertical(g10)
    c: Coincident(g11,g10)
    c: Coincident(g11,g1)
    c: Horizontal(g11)
    c: Distance(g4) = 23
    c: Distance(g4,g-1) = 20.25
    c: Distance(g5) = 3.25
    c: Distance(g6) = 5
    c: Distance(g7) = 8
    c: Distance(g6,g-2) = 16.15
    c: Distance(g8) = 5
    c: Distance(g9) = 3.25
    c: Distance(g10) = 23
    c: Distance(g0,g-2) = 10.25
    c: Distance(g0) = 23.25
    c: Distance(g2) = 19.75
FEATURE [Part::Extrusion] Extrude050
  Base = -> Sketch053
  Dir = (1,0,0)
  DirMode = 2
  FaceMakerClass = Part::FaceMakerBullseye
  FaceMakerMode = 3
  LengthFwd = 5
  LengthRev = 0
  Placement = pos=(0,4,40.25) rot=(-0.57735,0.57735,-0.57735;2.0944rad)
  Solid = true
  Symmetric = false
FEATURE [Part::Cut] Cut066  label="ESP_cut"
  Base = -> Cut065
  Refine = true
  Tool = -> Extrude050
FEATURE [Part::Cut] Cut067  label="LoRa_Cut"
  Base = -> Cut066
  Refine = true
  Tool = -> Box103
FEATURE [Part::Sphere] Sphere
  Angle1 = -90
  Angle2 = 90
  Angle3 = 180
  AttacherType = Attacher::AttachEngine3D
  Placement = pos=(-7.5,7.5,20) rot=(1,0,0;4.71239rad)
  Radius = 5
FEATURE [Part::Sphere] Sphere001
  Angle1 = -90
  Angle2 = 90
  Angle3 = 180
  AttacherType = Attacher::AttachEngine3D
  Placement = pos=(-7.5,7.5,87) rot=(-1,0,0;4.71239rad)
  Radius = 5
FEATURE [Part::Sphere] Sphere002
  Angle1 = -90
  Angle2 = 90
  Angle3 = 180
  AttacherType = Attacher::AttachEngine3D
  Placement = pos=(-7.5,7.5,9.65) rot=(1,0,0;4.71239rad)
  Radius = 3
FEATURE [Part::MultiFuse] Fusion078  label="bottomend"
  Refine = true
  Shapes = -> [Cylinder096,Sphere002]
FEATURE [Part::Sphere] Sphere003
  Angle1 = -90
  Angle2 = 90
  Angle3 = 180
  AttacherType = Attacher::AttachEngine3D
  Placement = pos=(-7.5,7.5,9.65) rot=(1,0,0;4.71239rad)
  Radius = 3
FEATURE [Part::MultiFuse] Fusion079  label="topend"
  Placement = pos=(0,15,107) rot=(1,0,0;3.14159rad)
  Refine = true
  Shapes = -> [Cylinder097,Sphere003]
FEATURE [Part::MultiFuse] Fusion083  label="Tube003"
  Refine = true
  Shapes = -> [Cylinder093,Sphere,Sphere001,Fusion078,Fusion079,Fusion080,Fusion081]
FEATURE [Part::FeaturePython] Tube003  label="Tube007"  # WARN: FeaturePython — macro-defined, semantics opaque (R4)
  AttacherType = Attacher::AttachEngine3D
  Height = 12
  InnerRadius = 1.5
  OuterRadius = 4
  Placement = pos=(71,12,18.5) rot=(0.57735,0.57735,-0.57735;2.0944rad)
FEATURE [Part::MultiFuse] Fusion087  label="Bottom001"
  Refine = true
  Shapes = -> [Tube003,Cut067]
FEATURE [App::Part] Part001  label="GeigerBottom001"
  Group = -> [Cut065,Sketch053,Fusion085,Fusion086,Cut064,Extrude047,Tube003,Sketch049,Box099,Box101,Cylinder102,Cylinder103,Extrude050,Cut066,Cut067,Box103,Fusion087]
  Origin = -> Origin001
  Placement = pos=(0,0,0) rot=(-0.57735,-0.57735,-0.57735;2.0944rad)
FEATURE [App::Part] USB_TYPE_C_PORT__1_  label="USB TYPE C PORT (1)"
  Group = -> [Part__Feature817,Part__Feature818,Part__Feature819,Part__Feature820,Part__Feature812,Part__Feature813,Part__Feature814,Part__Feature815,Part__Feature821,Part__Feature822,Part__Feature823,Part__Feature824,Part__Feature825,Part__Feature826,Part__Feature827,Part__Feature828,Part__Feature829,Part__Feature830,Part__Feature831,Part__Feature832,Part__Feature833,Part__Feature834,Part__Feature835,+1 more]
  Origin = -> Origin149
  Placement = pos=(-3.0192,1.09628,5.395) rot=(0,0,1;0rad)
FEATURE [App::Part] USB_TYPE_C_PORT  label="USB TYPE C PORT"
  Group = -> [USB_TYPE_C_PORT__1_]
  Origin = -> Origin150
  Placement = pos=(4.31609,13.395,-12.1571) rot=(0.57735,0.57735,-0.57735;2.0944rad)
FEATURE [App::Part] Seeed_Studio_XIAO_ESP32_S3__Sense_  label="Seeed Studio XIAO-ESP32-S3 (Sense)"
  Group = -> [USB_TYPE_C_PORT,Part__Feature837,SKTAAAE010_v1,SKTAAAE010_v002,Part__Feature848,Part__Feature849]
  Origin = -> Origin155
FEATURE [App::Part] XIAO_ESP32S3_v2  label="XIAO-ESP32S3 v2"
  Group = -> [Seeed_Studio_XIAO_ESP32_S3__Sense_]
  Origin = -> Origin156
  Placement = pos=(2.2,14,57) rot=(-0.57735,-0.57735,0.57735;4.18879rad)
FEATURE [App::Part] _069940102  label="2069940100002001"
  Group = -> [Part__Feature056,Part__Feature057]
  Origin = -> Origin015
  Placement = pos=(4,25.75,157.5) rot=(0.707107,0,0.707107;3.14159rad)
FEATURE [App::Part] _x_Male_Pin_2_54_mm  label="7x_Male_Pin_2.54_mm"
  Group = -> [Part__Feature850,Part__Feature851,Part__Feature852,Part__Feature853,Part__Feature854,Part__Feature855,Part__Feature856]
  Origin = -> Origin157
  Placement = pos=(-2.05,23.87,51.85) rot=(-0.57735,-0.57735,0.57735;4.18879rad)
FEATURE [App::Part] _x_Male_Pin_2_54_mm001  label="7x_Male_Pin_2.54_mm001"
  Group = -> [Part__Feature857,Part__Feature858,Part__Feature859,Part__Feature860,Part__Feature861,Part__Feature862,Part__Feature863]
  Origin = -> Origin158
  Placement = pos=(-2.05,39.12,51.85) rot=(-0.57735,-0.57735,0.57735;4.18879rad)
FEATURE [Part::MultiFuse] Fusion084  label="ESP"
  Placement = pos=(-1.4,0,0) rot=(0,0,1;0rad)
  Refine = true
  Shapes = -> [XIAO_ESP32S3_v2,_x_Male_Pin_2_54_mm,_x_Male_Pin_2_54_mm001,_069940102]
FEATURE [App::Part] Part025  label="ESP001"
  Group = -> [XIAO_ESP32S3_v2,_x_Male_Pin_2_54_mm,_x_Male_Pin_2_54_mm001,_069940102,Fusion084,Part__Feature864]
  Origin = -> Origin160
FEATURE [App::Part] pins  label="pins003"
  Group = -> [Part__Feature808,Part__Feature809,Part__Feature810]
  Origin = -> Origin147
FEATURE [App::Part] __pin_RMC_v0  label="3 pin RMC v0"
  Group = -> [pins,Part__Feature811]
  Origin = -> Origin148
  Placement = pos=(-3,12.25,7) rot=(0,0,1;4.71239rad)
FEATURE [App::Part] Part002  label="Radiation"
  Group = -> [Part__Feature816,Cylinder094,Cylinder095,Fusion082,Cylinder099,Cylinder100,Cylinder098,Cylinder101,Box094,Cut063,Sphere001,Sphere002,Cylinder093,Fusion079,Fusion078,Fusion081,Fusion080,Cylinder097,Cylinder096,Sphere003,Sphere,Box096,Box095,Box098,Box097,Fusion083,Fillet041,__pin_RMC_v0]
  Origin = -> Origin146
  Placement = pos=(-5.5,0,0) rot=(0,0,1;0rad)
FEATURE [Part::Compound] Compound010  label="Geiger"
  Links = -> [Part025,Part003,Part002,Part001,Part]
  Placement = pos=(-145,45,160) rot=(1,0,0;4.71239rad)
